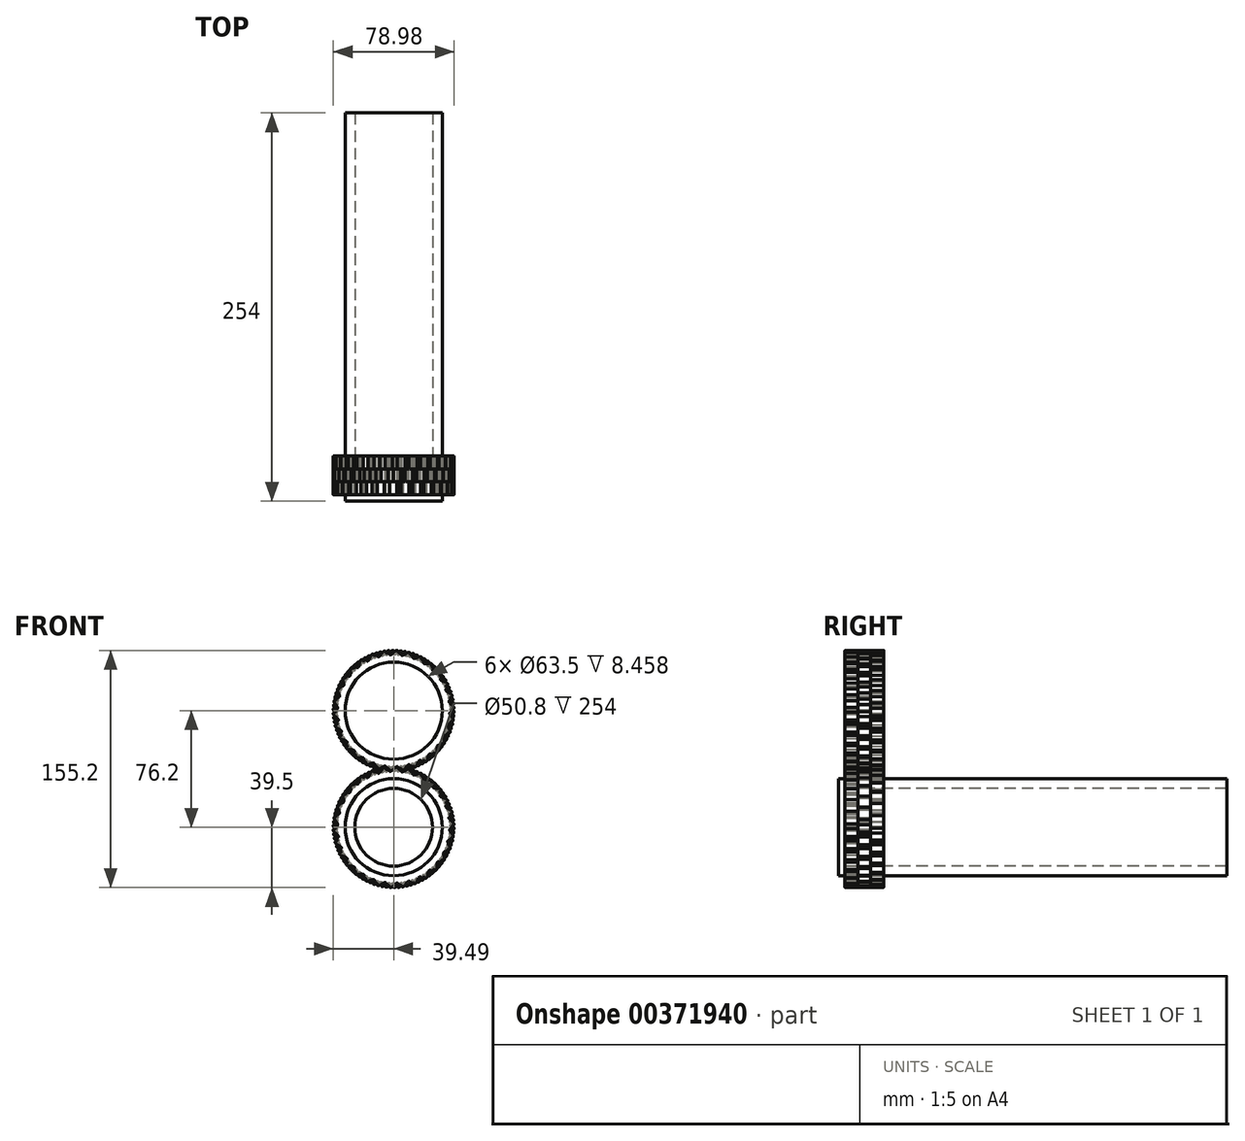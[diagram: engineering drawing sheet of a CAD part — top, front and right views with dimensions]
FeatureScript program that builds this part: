
annotation { "Feature Type Name" : "Feature", "Feature Type Description" : "" }
export const myFeature = defineFeature(function(context is Context, id is Id, definition is map)
    precondition{}
    {
        {
            var Q0;
            Q0=qCreatedBy(makeId("Front.planeOp"),FACE);
            var sketch = newSketch(context, id + "F0", { "sketchPlane" : qUnion([Q0])});
            skCircle(sketch, "E0", {"center": v(0, 0) * mm, "radius": 31.75 * mm});
            skCircle(sketch, "E1", {"center": v(0, 0) * mm, "radius": 25.4 * mm});
            skCircle(sketch, "E2", {"center": v(0, 0) * mm, "radius": 38.1 * mm});
            skPoint(sketch, "E3.middle", {"position": v(0, 38.1) * mm});
            skArc(sketch, "E4", {"start": v(-2.86, 36.42) * mm, "mid": v(-1.27, 36.98) * mm, "end": v(0, 38.1) * mm});
            skLineSegment(sketch, "E5", {"start": v(2.86, 39.78) * mm, "end": v(2.86, 38) * mm});
            skLineSegment(sketch, "E6", {"start": v(-2.86, 36.42) * mm, "end": v(-2.86, 38) * mm});
            skLineSegment(sketch, "E7.1.0", {"start": v(-10.37, 35.03) * mm, "end": v(-10.7, 36.57) * mm});
            skArc(sketch, "E7.1.1", {"start": v(-10.37, 35.03) * mm, "mid": v(-8.93, 35.91) * mm, "end": v(-7.92, 37.27) * mm});
            skArc(sketch, "E7.1.2", {"start": v(-5.48, 39.5) * mm, "mid": v(-6.92, 38.62) * mm, "end": v(-7.92, 37.27) * mm});
            skLineSegment(sketch, "E7.1.3", {"start": v(-5.48, 39.5) * mm, "end": v(-5.1, 37.76) * mm});
            skLineSegment(sketch, "E7.2.0", {"start": v(-17.42, 32.1) * mm, "end": v(-18.06, 33.55) * mm});
            skArc(sketch, "E7.2.1", {"start": v(-17.42, 32.1) * mm, "mid": v(-16.2, 33.27) * mm, "end": v(-15.5, 34.8) * mm});
            skArc(sketch, "E7.2.2", {"start": v(-13.57, 37.5) * mm, "mid": v(-14.8, 36.34) * mm, "end": v(-15.5, 34.8) * mm});
            skLineSegment(sketch, "E7.2.3", {"start": v(-13.57, 37.5) * mm, "end": v(-12.84, 35.87) * mm});
            skLineSegment(sketch, "E7.3.0", {"start": v(-23.72, 27.78) * mm, "end": v(-24.64, 29.06) * mm});
            skArc(sketch, "E7.3.1", {"start": v(-23.72, 27.78) * mm, "mid": v(-22.76, 29.18) * mm, "end": v(-22.4, 30.82) * mm});
            skArc(sketch, "E7.3.2", {"start": v(-21.07, 33.86) * mm, "mid": v(-22.03, 32.47) * mm, "end": v(-22.4, 30.82) * mm});
            skLineSegment(sketch, "E7.3.3", {"start": v(-21.07, 33.86) * mm, "end": v(-20.02, 32.42) * mm});
            skLineSegment(sketch, "E7.4.0", {"start": v(-28.98, 22.24) * mm, "end": v(-30.15, 23.3) * mm});
            skArc(sketch, "E7.4.1", {"start": v(-28.98, 22.24) * mm, "mid": v(-28.33, 23.8) * mm, "end": v(-28.31, 25.5) * mm});
            skArc(sketch, "E7.4.2", {"start": v(-27.65, 28.74) * mm, "mid": v(-28.3, 27.18) * mm, "end": v(-28.31, 25.5) * mm});
            skLineSegment(sketch, "E7.4.3", {"start": v(-27.65, 28.74) * mm, "end": v(-26.32, 27.55) * mm});
            skLineSegment(sketch, "E7.5.0", {"start": v(-32.97, 15.73) * mm, "end": v(-34.33, 16.52) * mm});
            skArc(sketch, "E7.5.1", {"start": v(-32.97, 15.73) * mm, "mid": v(-32.66, 17.4) * mm, "end": v(-33, 19.05) * mm});
            skArc(sketch, "E7.5.2", {"start": v(-33.02, 22.37) * mm, "mid": v(-33.33, 20.7) * mm, "end": v(-33, 19.05) * mm});
            skLineSegment(sketch, "E7.5.3", {"start": v(-33.02, 22.37) * mm, "end": v(-31.47, 21.47) * mm});
            skLineSegment(sketch, "E7.6.0", {"start": v(-35.52, 8.54) * mm, "end": v(-37.02, 9.02) * mm});
            skArc(sketch, "E7.6.1", {"start": v(-35.52, 8.54) * mm, "mid": v(-35.56, 10.22) * mm, "end": v(-36.24, 11.77) * mm});
            skArc(sketch, "E7.6.2", {"start": v(-36.95, 15.01) * mm, "mid": v(-36.9, 13.32) * mm, "end": v(-36.24, 11.77) * mm});
            skLineSegment(sketch, "E7.6.3", {"start": v(-36.95, 15.01) * mm, "end": v(-35.25, 14.46) * mm});
            skLineSegment(sketch, "E7.7.0", {"start": v(-36.52, 0.96) * mm, "end": v(-38.08, 1.13) * mm});
            skArc(sketch, "E7.7.1", {"start": v(-36.52, 0.96) * mm, "mid": v(-36.91, 2.6) * mm, "end": v(-37.9, 3.98) * mm});
            skArc(sketch, "E7.7.2", {"start": v(-39.27, 7) * mm, "mid": v(-38.87, 5.36) * mm, "end": v(-37.9, 3.98) * mm});
            skLineSegment(sketch, "E7.7.3", {"start": v(-39.27, 7) * mm, "end": v(-37.49, 6.81) * mm});
            skLineSegment(sketch, "E7.8.0", {"start": v(-35.92, -6.65) * mm, "end": v(-37.49, -6.81) * mm});
            skArc(sketch, "E7.8.1", {"start": v(-35.92, -6.65) * mm, "mid": v(-36.65, -5.13) * mm, "end": v(-37.9, -3.98) * mm});
            skArc(sketch, "E7.8.2", {"start": v(-39.86, -1.32) * mm, "mid": v(-39.13, -2.84) * mm, "end": v(-37.9, -3.98) * mm});
            skLineSegment(sketch, "E7.8.3", {"start": v(-39.86, -1.32) * mm, "end": v(-38.08, -1.13) * mm});
            skLineSegment(sketch, "E7.9.0", {"start": v(-33.75, -13.97) * mm, "end": v(-35.25, -14.46) * mm});
            skArc(sketch, "E7.9.1", {"start": v(-33.75, -13.97) * mm, "mid": v(-34.78, -12.63) * mm, "end": v(-36.24, -11.77) * mm});
            skArc(sketch, "E7.9.2", {"start": v(-38.72, -9.58) * mm, "mid": v(-37.69, -10.91) * mm, "end": v(-36.24, -11.77) * mm});
            skLineSegment(sketch, "E7.9.3", {"start": v(-38.72, -9.58) * mm, "end": v(-37.02, -9.02) * mm});
            skLineSegment(sketch, "E7.10.0", {"start": v(-30.11, -20.68) * mm, "end": v(-31.47, -21.47) * mm});
            skArc(sketch, "E7.10.1", {"start": v(-30.11, -20.68) * mm, "mid": v(-31.4, -19.59) * mm, "end": v(-33, -19.05) * mm});
            skArc(sketch, "E7.10.2", {"start": v(-35.88, -17.42) * mm, "mid": v(-34.6, -18.51) * mm, "end": v(-33, -19.05) * mm});
            skLineSegment(sketch, "E7.10.3", {"start": v(-35.88, -17.42) * mm, "end": v(-34.33, -16.52) * mm});
            skLineSegment(sketch, "E7.11.0", {"start": v(-25.15, -26.5) * mm, "end": v(-26.32, -27.55) * mm});
            skArc(sketch, "E7.11.1", {"start": v(-25.15, -26.5) * mm, "mid": v(-26.64, -25.69) * mm, "end": v(-28.31, -25.5) * mm});
            skArc(sketch, "E7.11.2", {"start": v(-31.48, -24.5) * mm, "mid": v(-30, -25.3) * mm, "end": v(-28.31, -25.5) * mm});
            skLineSegment(sketch, "E7.11.3", {"start": v(-31.48, -24.5) * mm, "end": v(-30.15, -23.3) * mm});
            skLineSegment(sketch, "E7.12.0", {"start": v(-19.1, -31.14) * mm, "end": v(-20.02, -32.42) * mm});
            skArc(sketch, "E7.12.1", {"start": v(-19.1, -31.14) * mm, "mid": v(-20.71, -30.66) * mm, "end": v(-22.4, -30.82) * mm});
            skArc(sketch, "E7.12.2", {"start": v(-25.7, -30.5) * mm, "mid": v(-24.08, -30.98) * mm, "end": v(-22.4, -30.82) * mm});
            skLineSegment(sketch, "E7.12.3", {"start": v(-25.7, -30.5) * mm, "end": v(-24.64, -29.06) * mm});
            skLineSegment(sketch, "E7.13.0", {"start": v(-12.2, -34.43) * mm, "end": v(-12.84, -35.87) * mm});
            skArc(sketch, "E7.13.1", {"start": v(-12.2, -34.43) * mm, "mid": v(-13.89, -34.3) * mm, "end": v(-15.5, -34.8) * mm});
            skArc(sketch, "E7.13.2", {"start": v(-18.8, -35.18) * mm, "mid": v(-17.1, -35.31) * mm, "end": v(-15.5, -34.8) * mm});
            skLineSegment(sketch, "E7.13.3", {"start": v(-18.8, -35.18) * mm, "end": v(-18.06, -33.55) * mm});
            skLineSegment(sketch, "E7.14.0", {"start": v(-4.78, -36.22) * mm, "end": v(-5.1, -37.76) * mm});
            skArc(sketch, "E7.14.1", {"start": v(-4.78, -36.22) * mm, "mid": v(-6.45, -36.44) * mm, "end": v(-7.92, -37.27) * mm});
            skArc(sketch, "E7.14.2", {"start": v(-11.07, -38.32) * mm, "mid": v(-9.4, -38.1) * mm, "end": v(-7.92, -37.27) * mm});
            skLineSegment(sketch, "E7.14.3", {"start": v(-11.07, -38.32) * mm, "end": v(-10.7, -36.57) * mm});
            skLineSegment(sketch, "E7.15.0", {"start": v(2.86, -36.42) * mm, "end": v(2.86, -38) * mm});
            skArc(sketch, "E7.15.1", {"start": v(2.86, -36.42) * mm, "mid": v(1.27, -36.98) * mm, "end": v(0, -38.1) * mm});
            skArc(sketch, "E7.15.2", {"start": v(-2.86, -39.78) * mm, "mid": v(-1.27, -39.22) * mm, "end": v(0, -38.1) * mm});
            skLineSegment(sketch, "E7.15.3", {"start": v(-2.86, -39.78) * mm, "end": v(-2.86, -38) * mm});
            skLineSegment(sketch, "E7.16.0", {"start": v(10.37, -35.03) * mm, "end": v(10.7, -36.57) * mm});
            skArc(sketch, "E7.16.1", {"start": v(10.37, -35.03) * mm, "mid": v(8.93, -35.91) * mm, "end": v(7.92, -37.27) * mm});
            skArc(sketch, "E7.16.2", {"start": v(5.48, -39.5) * mm, "mid": v(6.92, -38.62) * mm, "end": v(7.92, -37.27) * mm});
            skLineSegment(sketch, "E7.16.3", {"start": v(5.48, -39.5) * mm, "end": v(5.1, -37.76) * mm});
            skLineSegment(sketch, "E7.17.0", {"start": v(17.42, -32.1) * mm, "end": v(18.06, -33.55) * mm});
            skArc(sketch, "E7.17.1", {"start": v(17.42, -32.1) * mm, "mid": v(16.2, -33.27) * mm, "end": v(15.5, -34.8) * mm});
            skArc(sketch, "E7.17.2", {"start": v(13.57, -37.5) * mm, "mid": v(14.8, -36.34) * mm, "end": v(15.5, -34.8) * mm});
            skLineSegment(sketch, "E7.17.3", {"start": v(13.57, -37.5) * mm, "end": v(12.84, -35.87) * mm});
            skLineSegment(sketch, "E7.18.0", {"start": v(23.72, -27.78) * mm, "end": v(24.64, -29.06) * mm});
            skArc(sketch, "E7.18.1", {"start": v(23.72, -27.78) * mm, "mid": v(22.76, -29.18) * mm, "end": v(22.4, -30.82) * mm});
            skArc(sketch, "E7.18.2", {"start": v(21.07, -33.86) * mm, "mid": v(22.03, -32.47) * mm, "end": v(22.4, -30.82) * mm});
            skLineSegment(sketch, "E7.18.3", {"start": v(21.07, -33.86) * mm, "end": v(20.02, -32.42) * mm});
            skLineSegment(sketch, "E7.19.0", {"start": v(28.98, -22.24) * mm, "end": v(30.15, -23.3) * mm});
            skArc(sketch, "E7.19.1", {"start": v(28.98, -22.24) * mm, "mid": v(28.33, -23.8) * mm, "end": v(28.31, -25.5) * mm});
            skArc(sketch, "E7.19.2", {"start": v(27.65, -28.74) * mm, "mid": v(28.3, -27.18) * mm, "end": v(28.31, -25.5) * mm});
            skLineSegment(sketch, "E7.19.3", {"start": v(27.65, -28.74) * mm, "end": v(26.32, -27.55) * mm});
            skLineSegment(sketch, "E7.20.0", {"start": v(32.97, -15.73) * mm, "end": v(34.33, -16.52) * mm});
            skArc(sketch, "E7.20.1", {"start": v(32.97, -15.73) * mm, "mid": v(32.66, -17.4) * mm, "end": v(33, -19.05) * mm});
            skArc(sketch, "E7.20.2", {"start": v(33.02, -22.37) * mm, "mid": v(33.33, -20.7) * mm, "end": v(33, -19.05) * mm});
            skLineSegment(sketch, "E7.20.3", {"start": v(33.02, -22.37) * mm, "end": v(31.47, -21.47) * mm});
            skLineSegment(sketch, "E7.21.0", {"start": v(35.52, -8.54) * mm, "end": v(37.02, -9.02) * mm});
            skArc(sketch, "E7.21.1", {"start": v(35.52, -8.54) * mm, "mid": v(35.56, -10.22) * mm, "end": v(36.24, -11.77) * mm});
            skArc(sketch, "E7.21.2", {"start": v(36.95, -15.01) * mm, "mid": v(36.9, -13.32) * mm, "end": v(36.24, -11.77) * mm});
            skLineSegment(sketch, "E7.21.3", {"start": v(36.95, -15.01) * mm, "end": v(35.25, -14.46) * mm});
            skLineSegment(sketch, "E7.22.0", {"start": v(36.52, -0.96) * mm, "end": v(38.08, -1.13) * mm});
            skArc(sketch, "E7.22.1", {"start": v(36.52, -0.96) * mm, "mid": v(36.91, -2.6) * mm, "end": v(37.9, -3.98) * mm});
            skArc(sketch, "E7.22.2", {"start": v(39.27, -7) * mm, "mid": v(38.87, -5.36) * mm, "end": v(37.9, -3.98) * mm});
            skLineSegment(sketch, "E7.22.3", {"start": v(39.27, -7) * mm, "end": v(37.49, -6.81) * mm});
            skLineSegment(sketch, "E7.23.0", {"start": v(35.92, 6.65) * mm, "end": v(37.49, 6.81) * mm});
            skArc(sketch, "E7.23.1", {"start": v(35.92, 6.65) * mm, "mid": v(36.65, 5.13) * mm, "end": v(37.9, 3.98) * mm});
            skArc(sketch, "E7.23.2", {"start": v(39.86, 1.32) * mm, "mid": v(39.13, 2.84) * mm, "end": v(37.9, 3.98) * mm});
            skLineSegment(sketch, "E7.23.3", {"start": v(39.86, 1.32) * mm, "end": v(38.08, 1.13) * mm});
            skLineSegment(sketch, "E7.24.0", {"start": v(33.75, 13.97) * mm, "end": v(35.25, 14.46) * mm});
            skArc(sketch, "E7.24.1", {"start": v(33.75, 13.97) * mm, "mid": v(34.78, 12.63) * mm, "end": v(36.24, 11.77) * mm});
            skArc(sketch, "E7.24.2", {"start": v(38.72, 9.58) * mm, "mid": v(37.69, 10.91) * mm, "end": v(36.24, 11.77) * mm});
            skLineSegment(sketch, "E7.24.3", {"start": v(38.72, 9.58) * mm, "end": v(37.02, 9.02) * mm});
            skLineSegment(sketch, "E7.25.0", {"start": v(30.11, 20.68) * mm, "end": v(31.47, 21.47) * mm});
            skArc(sketch, "E7.25.1", {"start": v(30.11, 20.68) * mm, "mid": v(31.4, 19.59) * mm, "end": v(33, 19.05) * mm});
            skArc(sketch, "E7.25.2", {"start": v(35.88, 17.42) * mm, "mid": v(34.6, 18.51) * mm, "end": v(33, 19.05) * mm});
            skLineSegment(sketch, "E7.25.3", {"start": v(35.88, 17.42) * mm, "end": v(34.33, 16.52) * mm});
            skLineSegment(sketch, "E7.26.0", {"start": v(25.15, 26.5) * mm, "end": v(26.32, 27.55) * mm});
            skArc(sketch, "E7.26.1", {"start": v(25.15, 26.5) * mm, "mid": v(26.64, 25.69) * mm, "end": v(28.31, 25.5) * mm});
            skArc(sketch, "E7.26.2", {"start": v(31.48, 24.5) * mm, "mid": v(30, 25.3) * mm, "end": v(28.31, 25.5) * mm});
            skLineSegment(sketch, "E7.26.3", {"start": v(31.48, 24.5) * mm, "end": v(30.15, 23.3) * mm});
            skLineSegment(sketch, "E7.27.0", {"start": v(19.1, 31.14) * mm, "end": v(20.02, 32.42) * mm});
            skArc(sketch, "E7.27.1", {"start": v(19.1, 31.14) * mm, "mid": v(20.71, 30.66) * mm, "end": v(22.4, 30.82) * mm});
            skArc(sketch, "E7.27.2", {"start": v(25.7, 30.5) * mm, "mid": v(24.08, 30.98) * mm, "end": v(22.4, 30.82) * mm});
            skLineSegment(sketch, "E7.27.3", {"start": v(25.7, 30.5) * mm, "end": v(24.64, 29.06) * mm});
            skLineSegment(sketch, "E7.28.0", {"start": v(12.2, 34.43) * mm, "end": v(12.84, 35.87) * mm});
            skArc(sketch, "E7.28.1", {"start": v(12.2, 34.43) * mm, "mid": v(13.89, 34.3) * mm, "end": v(15.5, 34.8) * mm});
            skArc(sketch, "E7.28.2", {"start": v(18.8, 35.18) * mm, "mid": v(17.1, 35.31) * mm, "end": v(15.5, 34.8) * mm});
            skLineSegment(sketch, "E7.28.3", {"start": v(18.8, 35.18) * mm, "end": v(18.06, 33.55) * mm});
            skLineSegment(sketch, "E7.29.0", {"start": v(4.78, 36.22) * mm, "end": v(5.1, 37.76) * mm});
            skArc(sketch, "E7.29.1", {"start": v(4.78, 36.22) * mm, "mid": v(6.45, 36.44) * mm, "end": v(7.92, 37.27) * mm});
            skArc(sketch, "E7.29.2", {"start": v(11.07, 38.32) * mm, "mid": v(9.4, 38.1) * mm, "end": v(7.92, 37.27) * mm});
            skLineSegment(sketch, "E7.29.3", {"start": v(11.07, 38.32) * mm, "end": v(10.7, 36.57) * mm});
            skArc(sketch, "E8", {"start": v(1.88, 39.36) * mm, "mid": v(1.43, 39.2) * mm, "end": v(1, 38.97) * mm});
            skArc(sketch, "E9", {"start": v(2.86, 39.43) * mm, "mid": v(2.36, 39.46) * mm, "end": v(1.88, 39.36) * mm});
            skArc(sketch, "E10", {"start": v(1, 38.97) * mm, "mid": v(0.46, 38.58) * mm, "end": v(0, 38.1) * mm});
            skArc(sketch, "E11.1.0", {"start": v(-5.4, 39.17) * mm, "mid": v(-5.9, 39.1) * mm, "end": v(-6.34, 38.9) * mm});
            skArc(sketch, "E11.1.1", {"start": v(-6.34, 38.9) * mm, "mid": v(-6.75, 38.63) * mm, "end": v(-7.13, 38.33) * mm});
            skArc(sketch, "E11.1.2", {"start": v(-7.13, 38.33) * mm, "mid": v(-7.58, 37.84) * mm, "end": v(-7.92, 37.27) * mm});
            skArc(sketch, "E11.2.0", {"start": v(-13.43, 37.19) * mm, "mid": v(-13.9, 37.01) * mm, "end": v(-14.29, 36.72) * mm});
            skArc(sketch, "E11.2.1", {"start": v(-14.29, 36.72) * mm, "mid": v(-14.64, 36.39) * mm, "end": v(-14.94, 36.01) * mm});
            skArc(sketch, "E11.2.2", {"start": v(-14.94, 36.01) * mm, "mid": v(-15.28, 35.43) * mm, "end": v(-15.5, 34.8) * mm});
            skArc(sketch, "E11.3.0", {"start": v(-20.87, 33.58) * mm, "mid": v(-21.28, 33.32) * mm, "end": v(-21.61, 32.95) * mm});
            skArc(sketch, "E11.3.1", {"start": v(-21.61, 32.95) * mm, "mid": v(-21.88, 32.55) * mm, "end": v(-22.1, 32.12) * mm});
            skArc(sketch, "E11.3.2", {"start": v(-22.1, 32.12) * mm, "mid": v(-22.3, 31.48) * mm, "end": v(-22.4, 30.82) * mm});
            skArc(sketch, "E11.4.0", {"start": v(-27.4, 28.51) * mm, "mid": v(-27.74, 28.16) * mm, "end": v(-28, 27.74) * mm});
            skArc(sketch, "E11.4.1", {"start": v(-28, 27.74) * mm, "mid": v(-28.17, 27.29) * mm, "end": v(-28.3, 26.82) * mm});
            skArc(sketch, "E11.4.2", {"start": v(-28.3, 26.82) * mm, "mid": v(-28.37, 26.16) * mm, "end": v(-28.31, 25.5) * mm});
            skArc(sketch, "E11.5.0", {"start": v(-32.72, 22.2) * mm, "mid": v(-33, 21.78) * mm, "end": v(-33.15, 21.3) * mm});
            skArc(sketch, "E11.5.1", {"start": v(-33.15, 21.3) * mm, "mid": v(-33.23, 20.83) * mm, "end": v(-33.25, 20.35) * mm});
            skArc(sketch, "E11.5.2", {"start": v(-33.25, 20.35) * mm, "mid": v(-33.19, 19.69) * mm, "end": v(-33, 19.05) * mm});
            skArc(sketch, "E11.6.0", {"start": v(-36.62, 14.9) * mm, "mid": v(-36.8, 14.44) * mm, "end": v(-36.85, 13.95) * mm});
            skArc(sketch, "E11.6.1", {"start": v(-36.85, 13.95) * mm, "mid": v(-36.84, 13.47) * mm, "end": v(-36.76, 13) * mm});
            skArc(sketch, "E11.6.2", {"start": v(-36.76, 13) * mm, "mid": v(-36.55, 12.36) * mm, "end": v(-36.24, 11.77) * mm});
            skArc(sketch, "E11.7.0", {"start": v(-38.92, 6.96) * mm, "mid": v(-39, 6.48) * mm, "end": v(-38.95, 5.99) * mm});
            skArc(sketch, "E11.7.1", {"start": v(-38.95, 5.99) * mm, "mid": v(-38.83, 5.52) * mm, "end": v(-38.66, 5.06) * mm});
            skArc(sketch, "E11.7.2", {"start": v(-38.66, 5.06) * mm, "mid": v(-38.33, 4.49) * mm, "end": v(-37.9, 3.98) * mm});
            skArc(sketch, "E11.8.0", {"start": v(-39.52, -1.28) * mm, "mid": v(-39.5, -1.77) * mm, "end": v(-39.34, -2.24) * mm});
            skArc(sketch, "E11.8.1", {"start": v(-39.34, -2.24) * mm, "mid": v(-39.13, -2.68) * mm, "end": v(-38.87, -3.08) * mm});
            skArc(sketch, "E11.8.2", {"start": v(-38.87, -3.08) * mm, "mid": v(-38.42, -3.58) * mm, "end": v(-37.9, -3.98) * mm});
            skArc(sketch, "E11.9.0", {"start": v(-38.39, -9.47) * mm, "mid": v(-38.26, -9.95) * mm, "end": v(-38.01, -10.37) * mm});
            skArc(sketch, "E11.9.1", {"start": v(-38.01, -10.37) * mm, "mid": v(-37.72, -10.75) * mm, "end": v(-37.37, -11.1) * mm});
            skArc(sketch, "E11.9.2", {"start": v(-37.37, -11.1) * mm, "mid": v(-36.84, -11.49) * mm, "end": v(-36.24, -11.77) * mm});
            skArc(sketch, "E11.10.0", {"start": v(-35.58, -17.24) * mm, "mid": v(-35.36, -17.68) * mm, "end": v(-35.03, -18.05) * mm});
            skArc(sketch, "E11.10.1", {"start": v(-35.03, -18.05) * mm, "mid": v(-34.66, -18.36) * mm, "end": v(-34.25, -18.62) * mm});
            skArc(sketch, "E11.10.2", {"start": v(-34.25, -18.62) * mm, "mid": v(-33.64, -18.9) * mm, "end": v(-33, -19.05) * mm});
            skArc(sketch, "E11.11.0", {"start": v(-31.22, -24.26) * mm, "mid": v(-30.9, -24.65) * mm, "end": v(-30.5, -24.94) * mm});
            skArc(sketch, "E11.11.1", {"start": v(-30.5, -24.94) * mm, "mid": v(-30.08, -25.17) * mm, "end": v(-29.63, -25.34) * mm});
            skArc(sketch, "E11.11.2", {"start": v(-29.63, -25.34) * mm, "mid": v(-28.98, -25.48) * mm, "end": v(-28.31, -25.5) * mm});
            skArc(sketch, "E11.12.0", {"start": v(-25.5, -30.22) * mm, "mid": v(-25.1, -30.54) * mm, "end": v(-24.66, -30.74) * mm});
            skArc(sketch, "E11.12.1", {"start": v(-24.66, -30.74) * mm, "mid": v(-24.2, -30.87) * mm, "end": v(-23.71, -30.95) * mm});
            skArc(sketch, "E11.12.2", {"start": v(-23.71, -30.95) * mm, "mid": v(-23.05, -30.95) * mm, "end": v(-22.4, -30.82) * mm});
            skArc(sketch, "E11.13.0", {"start": v(-18.65, -34.86) * mm, "mid": v(-18.21, -35.09) * mm, "end": v(-17.73, -35.2) * mm});
            skArc(sketch, "E11.13.1", {"start": v(-17.73, -35.2) * mm, "mid": v(-17.25, -35.23) * mm, "end": v(-16.76, -35.2) * mm});
            skArc(sketch, "E11.13.2", {"start": v(-16.76, -35.2) * mm, "mid": v(-16.11, -35.06) * mm, "end": v(-15.5, -34.8) * mm});
            skArc(sketch, "E11.14.0", {"start": v(-11, -37.98) * mm, "mid": v(-10.52, -38.1) * mm, "end": v(-10.02, -38.1) * mm});
            skArc(sketch, "E11.14.1", {"start": v(-10.02, -38.1) * mm, "mid": v(-9.55, -38.04) * mm, "end": v(-9.08, -37.92) * mm});
            skArc(sketch, "E11.14.2", {"start": v(-9.08, -37.92) * mm, "mid": v(-8.47, -37.65) * mm, "end": v(-7.92, -37.27) * mm});
            skArc(sketch, "E11.15.0", {"start": v(-2.86, -39.43) * mm, "mid": v(-2.36, -39.46) * mm, "end": v(-1.88, -39.36) * mm});
            skArc(sketch, "E11.15.1", {"start": v(-1.88, -39.36) * mm, "mid": v(-1.43, -39.2) * mm, "end": v(-1, -38.97) * mm});
            skArc(sketch, "E11.15.2", {"start": v(-1, -38.97) * mm, "mid": v(-0.46, -38.58) * mm, "end": v(0, -38.1) * mm});
            skArc(sketch, "E11.16.0", {"start": v(5.4, -39.17) * mm, "mid": v(5.9, -39.1) * mm, "end": v(6.34, -38.9) * mm});
            skArc(sketch, "E11.16.1", {"start": v(6.34, -38.9) * mm, "mid": v(6.75, -38.63) * mm, "end": v(7.13, -38.33) * mm});
            skArc(sketch, "E11.16.2", {"start": v(7.13, -38.33) * mm, "mid": v(7.58, -37.84) * mm, "end": v(7.92, -37.27) * mm});
            skArc(sketch, "E11.17.0", {"start": v(13.43, -37.19) * mm, "mid": v(13.9, -37.01) * mm, "end": v(14.29, -36.72) * mm});
            skArc(sketch, "E11.17.1", {"start": v(14.29, -36.72) * mm, "mid": v(14.64, -36.39) * mm, "end": v(14.94, -36.01) * mm});
            skArc(sketch, "E11.17.2", {"start": v(14.94, -36.01) * mm, "mid": v(15.28, -35.43) * mm, "end": v(15.5, -34.8) * mm});
            skArc(sketch, "E11.18.0", {"start": v(20.87, -33.58) * mm, "mid": v(21.28, -33.32) * mm, "end": v(21.61, -32.95) * mm});
            skArc(sketch, "E11.18.1", {"start": v(21.61, -32.95) * mm, "mid": v(21.88, -32.55) * mm, "end": v(22.1, -32.12) * mm});
            skArc(sketch, "E11.18.2", {"start": v(22.1, -32.12) * mm, "mid": v(22.3, -31.48) * mm, "end": v(22.4, -30.82) * mm});
            skArc(sketch, "E11.19.0", {"start": v(27.4, -28.51) * mm, "mid": v(27.74, -28.16) * mm, "end": v(28, -27.74) * mm});
            skArc(sketch, "E11.19.1", {"start": v(28, -27.74) * mm, "mid": v(28.17, -27.29) * mm, "end": v(28.3, -26.82) * mm});
            skArc(sketch, "E11.19.2", {"start": v(28.3, -26.82) * mm, "mid": v(28.37, -26.16) * mm, "end": v(28.31, -25.5) * mm});
            skArc(sketch, "E11.20.0", {"start": v(32.72, -22.2) * mm, "mid": v(33, -21.78) * mm, "end": v(33.15, -21.3) * mm});
            skArc(sketch, "E11.20.1", {"start": v(33.15, -21.3) * mm, "mid": v(33.23, -20.83) * mm, "end": v(33.25, -20.35) * mm});
            skArc(sketch, "E11.20.2", {"start": v(33.25, -20.35) * mm, "mid": v(33.19, -19.69) * mm, "end": v(33, -19.05) * mm});
            skArc(sketch, "E11.21.0", {"start": v(36.62, -14.9) * mm, "mid": v(36.8, -14.44) * mm, "end": v(36.85, -13.95) * mm});
            skArc(sketch, "E11.21.1", {"start": v(36.85, -13.95) * mm, "mid": v(36.84, -13.47) * mm, "end": v(36.76, -13) * mm});
            skArc(sketch, "E11.21.2", {"start": v(36.76, -13) * mm, "mid": v(36.55, -12.36) * mm, "end": v(36.24, -11.77) * mm});
            skArc(sketch, "E11.22.0", {"start": v(38.92, -6.96) * mm, "mid": v(39, -6.48) * mm, "end": v(38.95, -5.99) * mm});
            skArc(sketch, "E11.22.1", {"start": v(38.95, -5.99) * mm, "mid": v(38.83, -5.52) * mm, "end": v(38.66, -5.06) * mm});
            skArc(sketch, "E11.22.2", {"start": v(38.66, -5.06) * mm, "mid": v(38.33, -4.49) * mm, "end": v(37.9, -3.98) * mm});
            skArc(sketch, "E11.23.0", {"start": v(39.52, 1.28) * mm, "mid": v(39.5, 1.77) * mm, "end": v(39.34, 2.24) * mm});
            skArc(sketch, "E11.23.1", {"start": v(39.34, 2.24) * mm, "mid": v(39.13, 2.68) * mm, "end": v(38.87, 3.08) * mm});
            skArc(sketch, "E11.23.2", {"start": v(38.87, 3.08) * mm, "mid": v(38.42, 3.58) * mm, "end": v(37.9, 3.98) * mm});
            skArc(sketch, "E11.24.0", {"start": v(38.39, 9.47) * mm, "mid": v(38.26, 9.95) * mm, "end": v(38.01, 10.37) * mm});
            skArc(sketch, "E11.24.1", {"start": v(38.01, 10.37) * mm, "mid": v(37.72, 10.75) * mm, "end": v(37.37, 11.1) * mm});
            skArc(sketch, "E11.24.2", {"start": v(37.37, 11.1) * mm, "mid": v(36.84, 11.49) * mm, "end": v(36.24, 11.77) * mm});
            skArc(sketch, "E11.25.0", {"start": v(35.58, 17.24) * mm, "mid": v(35.36, 17.68) * mm, "end": v(35.03, 18.05) * mm});
            skArc(sketch, "E11.25.1", {"start": v(35.03, 18.05) * mm, "mid": v(34.66, 18.36) * mm, "end": v(34.25, 18.62) * mm});
            skArc(sketch, "E11.25.2", {"start": v(34.25, 18.62) * mm, "mid": v(33.64, 18.9) * mm, "end": v(33, 19.05) * mm});
            skArc(sketch, "E11.26.0", {"start": v(31.22, 24.26) * mm, "mid": v(30.9, 24.65) * mm, "end": v(30.5, 24.94) * mm});
            skArc(sketch, "E11.26.1", {"start": v(30.5, 24.94) * mm, "mid": v(30.08, 25.17) * mm, "end": v(29.63, 25.34) * mm});
            skArc(sketch, "E11.26.2", {"start": v(29.63, 25.34) * mm, "mid": v(28.98, 25.48) * mm, "end": v(28.31, 25.5) * mm});
            skArc(sketch, "E11.27.0", {"start": v(25.5, 30.22) * mm, "mid": v(25.1, 30.54) * mm, "end": v(24.66, 30.74) * mm});
            skArc(sketch, "E11.27.1", {"start": v(24.66, 30.74) * mm, "mid": v(24.2, 30.87) * mm, "end": v(23.71, 30.95) * mm});
            skArc(sketch, "E11.27.2", {"start": v(23.71, 30.95) * mm, "mid": v(23.05, 30.95) * mm, "end": v(22.4, 30.82) * mm});
            skArc(sketch, "E11.28.0", {"start": v(18.65, 34.86) * mm, "mid": v(18.21, 35.09) * mm, "end": v(17.73, 35.2) * mm});
            skArc(sketch, "E11.28.1", {"start": v(17.73, 35.2) * mm, "mid": v(17.25, 35.23) * mm, "end": v(16.76, 35.2) * mm});
            skArc(sketch, "E11.28.2", {"start": v(16.76, 35.2) * mm, "mid": v(16.11, 35.06) * mm, "end": v(15.5, 34.8) * mm});
            skArc(sketch, "E11.29.0", {"start": v(11, 37.98) * mm, "mid": v(10.52, 38.1) * mm, "end": v(10.02, 38.1) * mm});
            skArc(sketch, "E11.29.1", {"start": v(10.02, 38.1) * mm, "mid": v(9.55, 38.04) * mm, "end": v(9.08, 37.92) * mm});
            skArc(sketch, "E11.29.2", {"start": v(9.08, 37.92) * mm, "mid": v(8.47, 37.65) * mm, "end": v(7.92, 37.27) * mm});
            skLineSegment(sketch, "E12", {"start": v(2.79, 39.45) * mm, "end": v(2.86, 38.71) * mm});
            skLineSegment(sketch, "E13.1.0", {"start": v(-5.47, 39.16) * mm, "end": v(-5.25, 38.46) * mm});
            skLineSegment(sketch, "E13.2.0", {"start": v(-13.5, 37.17) * mm, "end": v(-13.14, 36.53) * mm});
            skLineSegment(sketch, "E13.3.0", {"start": v(-20.93, 33.55) * mm, "end": v(-20.44, 33) * mm});
            skLineSegment(sketch, "E13.4.0", {"start": v(-27.45, 28.47) * mm, "end": v(-26.86, 28.03) * mm});
            skLineSegment(sketch, "E13.5.0", {"start": v(-32.77, 22.14) * mm, "end": v(-32.1, 21.83) * mm});
            skLineSegment(sketch, "E13.6.0", {"start": v(-36.65, 14.84) * mm, "end": v(-35.94, 14.68) * mm});
            skLineSegment(sketch, "E13.7.0", {"start": v(-38.94, 6.9) * mm, "end": v(-38.2, 6.89) * mm});
            skLineSegment(sketch, "E13.8.0", {"start": v(-39.52, -1.35) * mm, "end": v(-38.8, -1.2) * mm});
            skLineSegment(sketch, "E13.9.0", {"start": v(-38.38, -9.54) * mm, "end": v(-37.7, -9.25) * mm});
            skLineSegment(sketch, "E13.10.0", {"start": v(-35.56, -17.3) * mm, "end": v(-34.96, -16.88) * mm});
            skLineSegment(sketch, "E13.11.0", {"start": v(-31.18, -24.32) * mm, "end": v(-30.68, -23.78) * mm});
            skLineSegment(sketch, "E13.12.0", {"start": v(-25.44, -30.27) * mm, "end": v(-25.07, -29.64) * mm});
            skLineSegment(sketch, "E13.13.0", {"start": v(-18.6, -34.9) * mm, "end": v(-18.36, -34.2) * mm});
            skLineSegment(sketch, "E13.14.0", {"start": v(-10.93, -38) * mm, "end": v(-10.84, -37.27) * mm});
            skLineSegment(sketch, "E13.15.0", {"start": v(-2.79, -39.45) * mm, "end": v(-2.86, -38.71) * mm});
            skLineSegment(sketch, "E13.16.0", {"start": v(5.47, -39.16) * mm, "end": v(5.25, -38.46) * mm});
            skLineSegment(sketch, "E13.17.0", {"start": v(13.5, -37.17) * mm, "end": v(13.14, -36.53) * mm});
            skLineSegment(sketch, "E13.18.0", {"start": v(20.93, -33.55) * mm, "end": v(20.44, -33) * mm});
            skLineSegment(sketch, "E13.19.0", {"start": v(27.45, -28.47) * mm, "end": v(26.86, -28.03) * mm});
            skLineSegment(sketch, "E13.20.0", {"start": v(32.77, -22.14) * mm, "end": v(32.1, -21.83) * mm});
            skLineSegment(sketch, "E13.21.0", {"start": v(36.65, -14.84) * mm, "end": v(35.94, -14.68) * mm});
            skLineSegment(sketch, "E13.22.0", {"start": v(38.94, -6.9) * mm, "end": v(38.2, -6.89) * mm});
            skLineSegment(sketch, "E13.23.0", {"start": v(39.52, 1.35) * mm, "end": v(38.8, 1.2) * mm});
            skLineSegment(sketch, "E13.24.0", {"start": v(38.38, 9.54) * mm, "end": v(37.7, 9.25) * mm});
            skLineSegment(sketch, "E13.25.0", {"start": v(35.56, 17.3) * mm, "end": v(34.96, 16.88) * mm});
            skLineSegment(sketch, "E13.26.0", {"start": v(31.18, 24.32) * mm, "end": v(30.68, 23.78) * mm});
            skLineSegment(sketch, "E13.27.0", {"start": v(25.44, 30.27) * mm, "end": v(25.07, 29.64) * mm});
            skLineSegment(sketch, "E13.28.0", {"start": v(18.6, 34.9) * mm, "end": v(18.36, 34.2) * mm});
            skLineSegment(sketch, "E13.29.0", {"start": v(10.93, 38) * mm, "end": v(10.84, 37.27) * mm});
            skLineSegment(sketch, "E14", {"start": v(2.92, -37.99) * mm, "end": v(2.86, -37.2) * mm});
            skLineSegment(sketch, "E15.1.0", {"start": v(10.75, -36.55) * mm, "end": v(10.53, -35.8) * mm});
            skLineSegment(sketch, "E15.2.0", {"start": v(18.11, -33.52) * mm, "end": v(17.74, -32.83) * mm});
            skLineSegment(sketch, "E15.3.0", {"start": v(24.69, -29.02) * mm, "end": v(24.18, -28.42) * mm});
            skLineSegment(sketch, "E15.4.0", {"start": v(30.18, -23.25) * mm, "end": v(29.56, -22.77) * mm});
            skLineSegment(sketch, "E15.5.0", {"start": v(34.36, -16.47) * mm, "end": v(33.65, -16.13) * mm});
            skLineSegment(sketch, "E15.6.0", {"start": v(37.03, -8.97) * mm, "end": v(36.27, -8.78) * mm});
            skLineSegment(sketch, "E15.7.0", {"start": v(38.08, -1.07) * mm, "end": v(37.3, -1.05) * mm});
            skLineSegment(sketch, "E15.8.0", {"start": v(37.48, 6.87) * mm, "end": v(36.7, 6.73) * mm});
            skLineSegment(sketch, "E15.9.0", {"start": v(35.23, 14.51) * mm, "end": v(34.5, 14.21) * mm});
            skLineSegment(sketch, "E15.10.0", {"start": v(31.44, 21.52) * mm, "end": v(30.8, 21.08) * mm});
            skLineSegment(sketch, "E15.11.0", {"start": v(26.28, 27.59) * mm, "end": v(25.74, 27.02) * mm});
            skLineSegment(sketch, "E15.12.0", {"start": v(19.97, 32.45) * mm, "end": v(19.56, 31.78) * mm});
            skLineSegment(sketch, "E15.13.0", {"start": v(12.79, 35.89) * mm, "end": v(12.52, 35.15) * mm});
            skLineSegment(sketch, "E15.14.0", {"start": v(5.05, 37.76) * mm, "end": v(4.94, 36.99) * mm});
            skLineSegment(sketch, "E15.15.0", {"start": v(-2.92, 37.99) * mm, "end": v(-2.86, 37.2) * mm});
            skLineSegment(sketch, "E15.16.0", {"start": v(-10.75, 36.55) * mm, "end": v(-10.53, 35.8) * mm});
            skLineSegment(sketch, "E15.17.0", {"start": v(-18.11, 33.52) * mm, "end": v(-17.74, 32.83) * mm});
            skLineSegment(sketch, "E15.18.0", {"start": v(-24.69, 29.02) * mm, "end": v(-24.18, 28.42) * mm});
            skLineSegment(sketch, "E15.19.0", {"start": v(-30.18, 23.25) * mm, "end": v(-29.56, 22.77) * mm});
            skLineSegment(sketch, "E15.20.0", {"start": v(-34.36, 16.47) * mm, "end": v(-33.65, 16.13) * mm});
            skLineSegment(sketch, "E15.21.0", {"start": v(-37.03, 8.97) * mm, "end": v(-36.27, 8.78) * mm});
            skLineSegment(sketch, "E15.22.0", {"start": v(-38.08, 1.07) * mm, "end": v(-37.3, 1.05) * mm});
            skLineSegment(sketch, "E15.23.0", {"start": v(-37.48, -6.87) * mm, "end": v(-36.7, -6.73) * mm});
            skLineSegment(sketch, "E15.24.0", {"start": v(-35.23, -14.51) * mm, "end": v(-34.5, -14.21) * mm});
            skLineSegment(sketch, "E15.25.0", {"start": v(-31.44, -21.52) * mm, "end": v(-30.8, -21.08) * mm});
            skLineSegment(sketch, "E15.26.0", {"start": v(-26.28, -27.59) * mm, "end": v(-25.74, -27.02) * mm});
            skLineSegment(sketch, "E15.27.0", {"start": v(-19.97, -32.45) * mm, "end": v(-19.56, -31.78) * mm});
            skLineSegment(sketch, "E15.28.0", {"start": v(-12.79, -35.89) * mm, "end": v(-12.52, -35.15) * mm});
            skLineSegment(sketch, "E15.29.0", {"start": v(-5.05, -37.76) * mm, "end": v(-4.94, -36.99) * mm});
            skSolve(sketch);
        }
        {
            var Q0;
            Q0=makeQuery(id+"F0.imprint","IMPRINT",FACE,{"disambiguationData":[TD([[makeQuery(id+"F0.imprint","IMPRINT",EDGE,{"derivedFrom":sQuery(id+"F0.wireOp",EDGE,"E1")}),-1.0]])]});
            var Q1;
            {var subQ5=sQuery(id+"F0.wireOp",EDGE,"tDs8YB60-yQlt-PKr4-otda-xZHUuOfOvjSU.bottom");Q1=makeQuery(id+"F0.imprint","IMPRINT",FACE,{"disambiguationData":[TD([[makeQuery(id+"F0.imprint","IMPRINT",EDGE,{"derivedFrom":subQ5}),-1.0]])]});}
            extrude(context, id + "F1", {"entities" : qUnion([Q0, Q1]), "oppositeDirection" : true, "depth" : 254 * mm, "offsetDistance" : 25.4 * mm});
        }
        {
            var Q0;
            Q0=makeQuery(id+"F0.imprint","IMPRINT",FACE,{"disambiguationData":[TD([[makeQuery(id+"F0.imprint","IMPRINT",EDGE,{"derivedFrom":sQuery(id+"F0.wireOp",EDGE,"E0")}),-1.0]])]});
            var Q1;
            {var subQ3=sQuery(id+"F0.wireOp",EDGE,"F4ccViw4-8VKt-mRFL-Yw9l-lTW1q2JbDtwq");Q1=makeQuery(id+"F0.imprint","IMPRINT",FACE,{"disambiguationData":[TD([[makeQuery(id+"F0.imprint","IMPRINT",EDGE,{"derivedFrom":subQ3}),-1.0]])]});}
            var Q2;
            {var subQ1=sQuery(id+"F0.wireOp",EDGE,"E2");var subQ3=sQuery(id+"F0.wireOp",EDGE,"E5");var subQ4=makeQuery(id+"F0.imprint","INTERSECT",VERTEX,{"derivedFrom":[subQ1,subQ3]});Q2=makeQuery(id+"F0.imprint","IMPRINT",FACE,{"disambiguationData":[TD([[makeQuery(id+"F0.imprint","IMPRINT",EDGE,{"disambiguationData":[TD([[subQ4,-1.0]])],"derivedFrom":subQ1}),-1.0]])]});}
            var Q3;
            {var subQ4=sQuery(id+"F0.wireOp",EDGE,"E11.29.0");Q3=makeQuery(id+"F0.imprint","IMPRINT",FACE,{"disambiguationData":[TD([[makeQuery(id+"F0.imprint","IMPRINT",EDGE,{"derivedFrom":subQ4}),1.0]])]});}
            var Q4;
            {var subQ4=sQuery(id+"F0.wireOp",EDGE,"E11.28.0");Q4=makeQuery(id+"F0.imprint","IMPRINT",FACE,{"disambiguationData":[TD([[makeQuery(id+"F0.imprint","IMPRINT",EDGE,{"derivedFrom":subQ4}),1.0]])]});}
            var Q5;
            {var subQ4=sQuery(id+"F0.wireOp",EDGE,"E11.27.0");Q5=makeQuery(id+"F0.imprint","IMPRINT",FACE,{"disambiguationData":[TD([[makeQuery(id+"F0.imprint","IMPRINT",EDGE,{"derivedFrom":subQ4}),1.0]])]});}
            var Q6;
            {var subQ0=sQuery(id+"F0.wireOp",EDGE,"E11.26.0");Q6=makeQuery(id+"F0.imprint","IMPRINT",FACE,{"disambiguationData":[TD([[makeQuery(id+"F0.imprint","IMPRINT",EDGE,{"derivedFrom":subQ0}),1.0]])]});}
            var Q7;
            {var subQ0=sQuery(id+"F0.wireOp",EDGE,"E11.1.0");Q7=makeQuery(id+"F0.imprint","IMPRINT",FACE,{"disambiguationData":[TD([[makeQuery(id+"F0.imprint","IMPRINT",EDGE,{"derivedFrom":subQ0}),1.0]])]});}
            var Q8;
            {var subQ3=sQuery(id+"F0.wireOp",EDGE,"E11.2.0");Q8=makeQuery(id+"F0.imprint","IMPRINT",FACE,{"disambiguationData":[TD([[makeQuery(id+"F0.imprint","IMPRINT",EDGE,{"derivedFrom":subQ3}),1.0]])]});}
            var Q9;
            {var subQ0=sQuery(id+"F0.wireOp",EDGE,"E11.3.0");Q9=makeQuery(id+"F0.imprint","IMPRINT",FACE,{"disambiguationData":[TD([[makeQuery(id+"F0.imprint","IMPRINT",EDGE,{"derivedFrom":subQ0}),1.0]])]});}
            var Q10;
            {var subQ0=sQuery(id+"F0.wireOp",EDGE,"E11.4.0");Q10=makeQuery(id+"F0.imprint","IMPRINT",FACE,{"disambiguationData":[TD([[makeQuery(id+"F0.imprint","IMPRINT",EDGE,{"derivedFrom":subQ0}),1.0]])]});}
            var Q11;
            {var subQ0=sQuery(id+"F0.wireOp",EDGE,"E11.5.0");Q11=makeQuery(id+"F0.imprint","IMPRINT",FACE,{"disambiguationData":[TD([[makeQuery(id+"F0.imprint","IMPRINT",EDGE,{"derivedFrom":subQ0}),1.0]])]});}
            var Q12;
            {var subQ0=sQuery(id+"F0.wireOp",EDGE,"E11.6.0");Q12=makeQuery(id+"F0.imprint","IMPRINT",FACE,{"disambiguationData":[TD([[makeQuery(id+"F0.imprint","IMPRINT",EDGE,{"derivedFrom":subQ0}),1.0]])]});}
            var Q13;
            {var subQ0=sQuery(id+"F0.wireOp",EDGE,"E11.7.0");Q13=makeQuery(id+"F0.imprint","IMPRINT",FACE,{"disambiguationData":[TD([[makeQuery(id+"F0.imprint","IMPRINT",EDGE,{"derivedFrom":subQ0}),1.0]])]});}
            var Q14;
            {var subQ0=sQuery(id+"F0.wireOp",EDGE,"E11.8.0");Q14=makeQuery(id+"F0.imprint","IMPRINT",FACE,{"disambiguationData":[TD([[makeQuery(id+"F0.imprint","IMPRINT",EDGE,{"derivedFrom":subQ0}),1.0]])]});}
            var Q15;
            {var subQ4=sQuery(id+"F0.wireOp",EDGE,"E11.25.0");Q15=makeQuery(id+"F0.imprint","IMPRINT",FACE,{"disambiguationData":[TD([[makeQuery(id+"F0.imprint","IMPRINT",EDGE,{"derivedFrom":subQ4}),1.0]])]});}
            var Q16;
            {var subQ3=sQuery(id+"F0.wireOp",EDGE,"E11.24.0");Q16=makeQuery(id+"F0.imprint","IMPRINT",FACE,{"disambiguationData":[TD([[makeQuery(id+"F0.imprint","IMPRINT",EDGE,{"derivedFrom":subQ3}),1.0]])]});}
            var Q17;
            {var subQ4=sQuery(id+"F0.wireOp",EDGE,"E11.23.0");Q17=makeQuery(id+"F0.imprint","IMPRINT",FACE,{"disambiguationData":[TD([[makeQuery(id+"F0.imprint","IMPRINT",EDGE,{"derivedFrom":subQ4}),1.0]])]});}
            var Q18;
            {var subQ0=sQuery(id+"F0.wireOp",EDGE,"E11.22.0");Q18=makeQuery(id+"F0.imprint","IMPRINT",FACE,{"disambiguationData":[TD([[makeQuery(id+"F0.imprint","IMPRINT",EDGE,{"derivedFrom":subQ0}),1.0]])]});}
            var Q19;
            {var subQ0=sQuery(id+"F0.wireOp",EDGE,"E11.21.0");Q19=makeQuery(id+"F0.imprint","IMPRINT",FACE,{"disambiguationData":[TD([[makeQuery(id+"F0.imprint","IMPRINT",EDGE,{"derivedFrom":subQ0}),1.0]])]});}
            var Q20;
            {var subQ0=sQuery(id+"F0.wireOp",EDGE,"E11.20.0");Q20=makeQuery(id+"F0.imprint","IMPRINT",FACE,{"disambiguationData":[TD([[makeQuery(id+"F0.imprint","IMPRINT",EDGE,{"derivedFrom":subQ0}),1.0]])]});}
            var Q21;
            {var subQ0=sQuery(id+"F0.wireOp",EDGE,"E11.18.0");Q21=makeQuery(id+"F0.imprint","IMPRINT",FACE,{"disambiguationData":[TD([[makeQuery(id+"F0.imprint","IMPRINT",EDGE,{"derivedFrom":subQ0}),1.0]])]});}
            var Q22;
            {var subQ0=sQuery(id+"F0.wireOp",EDGE,"E11.17.0");Q22=makeQuery(id+"F0.imprint","IMPRINT",FACE,{"disambiguationData":[TD([[makeQuery(id+"F0.imprint","IMPRINT",EDGE,{"derivedFrom":subQ0}),1.0]])]});}
            var Q23;
            {var subQ0=sQuery(id+"F0.wireOp",EDGE,"E11.16.0");Q23=makeQuery(id+"F0.imprint","IMPRINT",FACE,{"disambiguationData":[TD([[makeQuery(id+"F0.imprint","IMPRINT",EDGE,{"derivedFrom":subQ0}),1.0]])]});}
            var Q24;
            {var subQ0=sQuery(id+"F0.wireOp",EDGE,"E11.15.0");Q24=makeQuery(id+"F0.imprint","IMPRINT",FACE,{"disambiguationData":[TD([[makeQuery(id+"F0.imprint","IMPRINT",EDGE,{"derivedFrom":subQ0}),1.0]])]});}
            var Q25;
            {var subQ0=sQuery(id+"F0.wireOp",EDGE,"E11.14.0");Q25=makeQuery(id+"F0.imprint","IMPRINT",FACE,{"disambiguationData":[TD([[makeQuery(id+"F0.imprint","IMPRINT",EDGE,{"derivedFrom":subQ0}),1.0]])]});}
            var Q26;
            {var subQ3=sQuery(id+"F0.wireOp",EDGE,"E11.13.0");Q26=makeQuery(id+"F0.imprint","IMPRINT",FACE,{"disambiguationData":[TD([[makeQuery(id+"F0.imprint","IMPRINT",EDGE,{"derivedFrom":subQ3}),1.0]])]});}
            var Q27;
            {var subQ0=sQuery(id+"F0.wireOp",EDGE,"E11.12.0");Q27=makeQuery(id+"F0.imprint","IMPRINT",FACE,{"disambiguationData":[TD([[makeQuery(id+"F0.imprint","IMPRINT",EDGE,{"derivedFrom":subQ0}),1.0]])]});}
            var Q28;
            {var subQ0=sQuery(id+"F0.wireOp",EDGE,"E11.11.0");Q28=makeQuery(id+"F0.imprint","IMPRINT",FACE,{"disambiguationData":[TD([[makeQuery(id+"F0.imprint","IMPRINT",EDGE,{"derivedFrom":subQ0}),1.0]])]});}
            var Q29;
            {var subQ0=sQuery(id+"F0.wireOp",EDGE,"E11.10.0");Q29=makeQuery(id+"F0.imprint","IMPRINT",FACE,{"disambiguationData":[TD([[makeQuery(id+"F0.imprint","IMPRINT",EDGE,{"derivedFrom":subQ0}),1.0]])]});}
            var Q30;
            {var subQ0=sQuery(id+"F0.wireOp",EDGE,"E11.9.0");Q30=makeQuery(id+"F0.imprint","IMPRINT",FACE,{"disambiguationData":[TD([[makeQuery(id+"F0.imprint","IMPRINT",EDGE,{"derivedFrom":subQ0}),1.0]])]});}
            var Q31;
            {var subQ0=sQuery(id+"F0.wireOp",EDGE,"E11.19.0");Q31=makeQuery(id+"F0.imprint","IMPRINT",FACE,{"disambiguationData":[TD([[makeQuery(id+"F0.imprint","IMPRINT",EDGE,{"derivedFrom":subQ0}),1.0]])]});}
            var Q32;
            {var subQ0=sQuery(id+"F0.wireOp",EDGE,"E11.1.1");Q32=makeQuery(id+"F0.imprint","IMPRINT",FACE,{"disambiguationData":[TD([[makeQuery(id+"F0.imprint","IMPRINT",EDGE,{"derivedFrom":subQ0}),1.0]])]});}
            var Q33;
            {var subQ0=sQuery(id+"F0.wireOp",EDGE,"E11.2.1");Q33=makeQuery(id+"F0.imprint","IMPRINT",FACE,{"disambiguationData":[TD([[makeQuery(id+"F0.imprint","IMPRINT",EDGE,{"derivedFrom":subQ0}),1.0]])]});}
            var Q34;
            {var subQ0=sQuery(id+"F0.wireOp",EDGE,"E11.3.1");Q34=makeQuery(id+"F0.imprint","IMPRINT",FACE,{"disambiguationData":[TD([[makeQuery(id+"F0.imprint","IMPRINT",EDGE,{"derivedFrom":subQ0}),1.0]])]});}
            var Q35;
            {var subQ0=sQuery(id+"F0.wireOp",EDGE,"E11.4.1");Q35=makeQuery(id+"F0.imprint","IMPRINT",FACE,{"disambiguationData":[TD([[makeQuery(id+"F0.imprint","IMPRINT",EDGE,{"derivedFrom":subQ0}),1.0]])]});}
            var Q36;
            {var subQ0=sQuery(id+"F0.wireOp",EDGE,"E11.5.1");Q36=makeQuery(id+"F0.imprint","IMPRINT",FACE,{"disambiguationData":[TD([[makeQuery(id+"F0.imprint","IMPRINT",EDGE,{"derivedFrom":subQ0}),1.0]])]});}
            var Q37;
            {var subQ0=sQuery(id+"F0.wireOp",EDGE,"E11.6.1");Q37=makeQuery(id+"F0.imprint","IMPRINT",FACE,{"disambiguationData":[TD([[makeQuery(id+"F0.imprint","IMPRINT",EDGE,{"derivedFrom":subQ0}),1.0]])]});}
            var Q38;
            {var subQ0=sQuery(id+"F0.wireOp",EDGE,"E11.7.1");Q38=makeQuery(id+"F0.imprint","IMPRINT",FACE,{"disambiguationData":[TD([[makeQuery(id+"F0.imprint","IMPRINT",EDGE,{"derivedFrom":subQ0}),1.0]])]});}
            var Q39;
            {var subQ0=sQuery(id+"F0.wireOp",EDGE,"E11.8.1");Q39=makeQuery(id+"F0.imprint","IMPRINT",FACE,{"disambiguationData":[TD([[makeQuery(id+"F0.imprint","IMPRINT",EDGE,{"derivedFrom":subQ0}),1.0]])]});}
            var Q40;
            {var subQ0=sQuery(id+"F0.wireOp",EDGE,"E11.9.1");Q40=makeQuery(id+"F0.imprint","IMPRINT",FACE,{"disambiguationData":[TD([[makeQuery(id+"F0.imprint","IMPRINT",EDGE,{"derivedFrom":subQ0}),1.0]])]});}
            var Q41;
            {var subQ0=sQuery(id+"F0.wireOp",EDGE,"E11.10.1");Q41=makeQuery(id+"F0.imprint","IMPRINT",FACE,{"disambiguationData":[TD([[makeQuery(id+"F0.imprint","IMPRINT",EDGE,{"derivedFrom":subQ0}),1.0]])]});}
            var Q42;
            {var subQ0=sQuery(id+"F0.wireOp",EDGE,"E11.11.1");Q42=makeQuery(id+"F0.imprint","IMPRINT",FACE,{"disambiguationData":[TD([[makeQuery(id+"F0.imprint","IMPRINT",EDGE,{"derivedFrom":subQ0}),1.0]])]});}
            var Q43;
            {var subQ0=sQuery(id+"F0.wireOp",EDGE,"E11.12.1");Q43=makeQuery(id+"F0.imprint","IMPRINT",FACE,{"disambiguationData":[TD([[makeQuery(id+"F0.imprint","IMPRINT",EDGE,{"derivedFrom":subQ0}),1.0]])]});}
            var Q44;
            {var subQ0=sQuery(id+"F0.wireOp",EDGE,"E11.13.1");Q44=makeQuery(id+"F0.imprint","IMPRINT",FACE,{"disambiguationData":[TD([[makeQuery(id+"F0.imprint","IMPRINT",EDGE,{"derivedFrom":subQ0}),1.0]])]});}
            var Q45;
            {var subQ0=sQuery(id+"F0.wireOp",EDGE,"E11.14.1");Q45=makeQuery(id+"F0.imprint","IMPRINT",FACE,{"disambiguationData":[TD([[makeQuery(id+"F0.imprint","IMPRINT",EDGE,{"derivedFrom":subQ0}),1.0]])]});}
            var Q46;
            {var subQ0=sQuery(id+"F0.wireOp",EDGE,"E11.15.1");Q46=makeQuery(id+"F0.imprint","IMPRINT",FACE,{"disambiguationData":[TD([[makeQuery(id+"F0.imprint","IMPRINT",EDGE,{"derivedFrom":subQ0}),1.0]])]});}
            var Q47;
            {var subQ0=sQuery(id+"F0.wireOp",EDGE,"E11.16.1");Q47=makeQuery(id+"F0.imprint","IMPRINT",FACE,{"disambiguationData":[TD([[makeQuery(id+"F0.imprint","IMPRINT",EDGE,{"derivedFrom":subQ0}),1.0]])]});}
            var Q48;
            {var subQ0=sQuery(id+"F0.wireOp",EDGE,"E11.17.1");Q48=makeQuery(id+"F0.imprint","IMPRINT",FACE,{"disambiguationData":[TD([[makeQuery(id+"F0.imprint","IMPRINT",EDGE,{"derivedFrom":subQ0}),1.0]])]});}
            var Q49;
            {var subQ0=sQuery(id+"F0.wireOp",EDGE,"E11.18.1");Q49=makeQuery(id+"F0.imprint","IMPRINT",FACE,{"disambiguationData":[TD([[makeQuery(id+"F0.imprint","IMPRINT",EDGE,{"derivedFrom":subQ0}),1.0]])]});}
            var Q50;
            {var subQ0=sQuery(id+"F0.wireOp",EDGE,"E11.19.1");Q50=makeQuery(id+"F0.imprint","IMPRINT",FACE,{"disambiguationData":[TD([[makeQuery(id+"F0.imprint","IMPRINT",EDGE,{"derivedFrom":subQ0}),1.0]])]});}
            var Q51;
            {var subQ0=sQuery(id+"F0.wireOp",EDGE,"E11.20.1");Q51=makeQuery(id+"F0.imprint","IMPRINT",FACE,{"disambiguationData":[TD([[makeQuery(id+"F0.imprint","IMPRINT",EDGE,{"derivedFrom":subQ0}),1.0]])]});}
            var Q52;
            {var subQ0=sQuery(id+"F0.wireOp",EDGE,"E11.21.1");Q52=makeQuery(id+"F0.imprint","IMPRINT",FACE,{"disambiguationData":[TD([[makeQuery(id+"F0.imprint","IMPRINT",EDGE,{"derivedFrom":subQ0}),1.0]])]});}
            var Q53;
            {var subQ0=sQuery(id+"F0.wireOp",EDGE,"E11.22.1");Q53=makeQuery(id+"F0.imprint","IMPRINT",FACE,{"disambiguationData":[TD([[makeQuery(id+"F0.imprint","IMPRINT",EDGE,{"derivedFrom":subQ0}),1.0]])]});}
            var Q54;
            {var subQ0=sQuery(id+"F0.wireOp",EDGE,"E11.23.1");Q54=makeQuery(id+"F0.imprint","IMPRINT",FACE,{"disambiguationData":[TD([[makeQuery(id+"F0.imprint","IMPRINT",EDGE,{"derivedFrom":subQ0}),1.0]])]});}
            var Q55;
            {var subQ0=sQuery(id+"F0.wireOp",EDGE,"E11.24.1");Q55=makeQuery(id+"F0.imprint","IMPRINT",FACE,{"disambiguationData":[TD([[makeQuery(id+"F0.imprint","IMPRINT",EDGE,{"derivedFrom":subQ0}),1.0]])]});}
            var Q56;
            {var subQ0=sQuery(id+"F0.wireOp",EDGE,"E11.25.1");Q56=makeQuery(id+"F0.imprint","IMPRINT",FACE,{"disambiguationData":[TD([[makeQuery(id+"F0.imprint","IMPRINT",EDGE,{"derivedFrom":subQ0}),1.0]])]});}
            var Q57;
            {var subQ0=sQuery(id+"F0.wireOp",EDGE,"E11.26.1");Q57=makeQuery(id+"F0.imprint","IMPRINT",FACE,{"disambiguationData":[TD([[makeQuery(id+"F0.imprint","IMPRINT",EDGE,{"derivedFrom":subQ0}),1.0]])]});}
            var Q58;
            {var subQ0=sQuery(id+"F0.wireOp",EDGE,"E11.27.1");Q58=makeQuery(id+"F0.imprint","IMPRINT",FACE,{"disambiguationData":[TD([[makeQuery(id+"F0.imprint","IMPRINT",EDGE,{"derivedFrom":subQ0}),1.0]])]});}
            var Q59;
            {var subQ0=sQuery(id+"F0.wireOp",EDGE,"E11.28.1");Q59=makeQuery(id+"F0.imprint","IMPRINT",FACE,{"disambiguationData":[TD([[makeQuery(id+"F0.imprint","IMPRINT",EDGE,{"derivedFrom":subQ0}),1.0]])]});}
            var Q60;
            {var subQ0=sQuery(id+"F0.wireOp",EDGE,"E11.29.1");Q60=makeQuery(id+"F0.imprint","IMPRINT",FACE,{"disambiguationData":[TD([[makeQuery(id+"F0.imprint","IMPRINT",EDGE,{"derivedFrom":subQ0}),1.0]])]});}
            extrude(context, id + "F2", {"entities" : qUnion([Q0, Q1, Q2, Q3, Q4, Q5, Q6, Q7, Q8, Q9, Q10, Q11, Q12, Q13, Q14, Q15, Q16, Q17, Q18, Q19, Q20, Q21, Q22, Q23, Q24, Q25, Q26, Q27, Q28, Q29, Q30, Q31, Q32, Q33, Q34, Q35, Q36, Q37, Q38, Q39, Q40, Q41, Q42, Q43, Q44, Q45, Q46, Q47, Q48, Q49, Q50, Q51, Q52, Q53, Q54, Q55, Q56, Q57, Q58, Q59, Q60]), "depth" : 8.46 * mm, "offsetDistance" : 25.4 * mm});
        }
        {
            var Q0;
            Q0=makeQuery(id+"F2.opExtrude","SWEPT_BODY",BODY,{"disambiguationData":[OSD([sQuery(id+"F0.wireOp",EDGE,"E0"),sQuery(id+"F0.wireOp",EDGE,"E2"),sQuery(id+"F0.wireOp",EDGE,"kblbpXZE-b2Sg-FZdv-FlMF-ZwbeqijesS82"),sQuery(id+"F0.wireOp",EDGE,"E4"),sQuery(id+"F0.wireOp",EDGE,"E5"),sQuery(id+"F0.wireOp",EDGE,"E6"),sQuery(id+"F0.wireOp",EDGE,"E7.1.0"),sQuery(id+"F0.wireOp",EDGE,"E7.1.1"),sQuery(id+"F0.wireOp",EDGE,"E7.1.2"),sQuery(id+"F0.wireOp",EDGE,"E7.1.3"),sQuery(id+"F0.wireOp",EDGE,"E7.2.0"),sQuery(id+"F0.wireOp",EDGE,"E7.2.1"),sQuery(id+"F0.wireOp",EDGE,"E7.2.2"),sQuery(id+"F0.wireOp",EDGE,"E7.2.3"),sQuery(id+"F0.wireOp",EDGE,"E7.3.0"),sQuery(id+"F0.wireOp",EDGE,"E7.3.1"),sQuery(id+"F0.wireOp",EDGE,"E7.3.2"),sQuery(id+"F0.wireOp",EDGE,"E7.3.3"),sQuery(id+"F0.wireOp",EDGE,"E7.4.0"),sQuery(id+"F0.wireOp",EDGE,"E7.4.1"),sQuery(id+"F0.wireOp",EDGE,"E7.4.2"),sQuery(id+"F0.wireOp",EDGE,"E7.4.3"),sQuery(id+"F0.wireOp",EDGE,"E7.5.0"),sQuery(id+"F0.wireOp",EDGE,"E7.5.1"),sQuery(id+"F0.wireOp",EDGE,"E7.5.2"),sQuery(id+"F0.wireOp",EDGE,"E7.5.3"),sQuery(id+"F0.wireOp",EDGE,"E7.6.0"),sQuery(id+"F0.wireOp",EDGE,"E7.6.1"),sQuery(id+"F0.wireOp",EDGE,"E7.6.2"),sQuery(id+"F0.wireOp",EDGE,"E7.6.3"),sQuery(id+"F0.wireOp",EDGE,"E7.7.0"),sQuery(id+"F0.wireOp",EDGE,"E7.7.1"),sQuery(id+"F0.wireOp",EDGE,"E7.7.2"),sQuery(id+"F0.wireOp",EDGE,"E7.7.3"),sQuery(id+"F0.wireOp",EDGE,"E7.8.0"),sQuery(id+"F0.wireOp",EDGE,"E7.8.1"),sQuery(id+"F0.wireOp",EDGE,"E7.8.2"),sQuery(id+"F0.wireOp",EDGE,"E7.8.3"),sQuery(id+"F0.wireOp",EDGE,"E7.9.0"),sQuery(id+"F0.wireOp",EDGE,"E7.9.1"),sQuery(id+"F0.wireOp",EDGE,"E7.9.2"),sQuery(id+"F0.wireOp",EDGE,"E7.9.3"),sQuery(id+"F0.wireOp",EDGE,"E7.10.0"),sQuery(id+"F0.wireOp",EDGE,"E7.10.1"),sQuery(id+"F0.wireOp",EDGE,"E7.10.2"),sQuery(id+"F0.wireOp",EDGE,"E7.10.3"),sQuery(id+"F0.wireOp",EDGE,"E7.11.0"),sQuery(id+"F0.wireOp",EDGE,"E7.11.1"),sQuery(id+"F0.wireOp",EDGE,"E7.11.2"),sQuery(id+"F0.wireOp",EDGE,"E7.11.3"),sQuery(id+"F0.wireOp",EDGE,"E7.12.0"),sQuery(id+"F0.wireOp",EDGE,"E7.12.1"),sQuery(id+"F0.wireOp",EDGE,"E7.12.2"),sQuery(id+"F0.wireOp",EDGE,"E7.12.3"),sQuery(id+"F0.wireOp",EDGE,"E7.13.0"),sQuery(id+"F0.wireOp",EDGE,"E7.13.1"),sQuery(id+"F0.wireOp",EDGE,"E7.13.2"),sQuery(id+"F0.wireOp",EDGE,"E7.13.3"),sQuery(id+"F0.wireOp",EDGE,"E7.14.0"),sQuery(id+"F0.wireOp",EDGE,"E7.14.1"),sQuery(id+"F0.wireOp",EDGE,"E7.14.2"),sQuery(id+"F0.wireOp",EDGE,"E7.14.3"),sQuery(id+"F0.wireOp",EDGE,"E7.15.0"),sQuery(id+"F0.wireOp",EDGE,"E7.15.1"),sQuery(id+"F0.wireOp",EDGE,"E7.15.2"),sQuery(id+"F0.wireOp",EDGE,"E7.15.3"),sQuery(id+"F0.wireOp",EDGE,"E7.16.0"),sQuery(id+"F0.wireOp",EDGE,"E7.16.1"),sQuery(id+"F0.wireOp",EDGE,"E7.16.2"),sQuery(id+"F0.wireOp",EDGE,"E7.16.3"),sQuery(id+"F0.wireOp",EDGE,"E7.17.0"),sQuery(id+"F0.wireOp",EDGE,"E7.17.1"),sQuery(id+"F0.wireOp",EDGE,"E7.17.2"),sQuery(id+"F0.wireOp",EDGE,"E7.17.3"),sQuery(id+"F0.wireOp",EDGE,"E7.18.0"),sQuery(id+"F0.wireOp",EDGE,"E7.18.1"),sQuery(id+"F0.wireOp",EDGE,"E7.18.2"),sQuery(id+"F0.wireOp",EDGE,"E7.18.3"),sQuery(id+"F0.wireOp",EDGE,"E7.19.0"),sQuery(id+"F0.wireOp",EDGE,"E7.19.1"),sQuery(id+"F0.wireOp",EDGE,"E7.19.2"),sQuery(id+"F0.wireOp",EDGE,"E7.19.3"),sQuery(id+"F0.wireOp",EDGE,"E7.20.0"),sQuery(id+"F0.wireOp",EDGE,"E7.20.1"),sQuery(id+"F0.wireOp",EDGE,"E7.20.2"),sQuery(id+"F0.wireOp",EDGE,"E7.20.3"),sQuery(id+"F0.wireOp",EDGE,"E7.21.0"),sQuery(id+"F0.wireOp",EDGE,"E7.21.1"),sQuery(id+"F0.wireOp",EDGE,"E7.21.2"),sQuery(id+"F0.wireOp",EDGE,"E7.21.3"),sQuery(id+"F0.wireOp",EDGE,"E7.22.0"),sQuery(id+"F0.wireOp",EDGE,"E7.22.1"),sQuery(id+"F0.wireOp",EDGE,"E7.22.2"),sQuery(id+"F0.wireOp",EDGE,"E7.22.3"),sQuery(id+"F0.wireOp",EDGE,"E7.23.0"),sQuery(id+"F0.wireOp",EDGE,"E7.23.1"),sQuery(id+"F0.wireOp",EDGE,"E7.23.2"),sQuery(id+"F0.wireOp",EDGE,"E7.23.3"),sQuery(id+"F0.wireOp",EDGE,"E7.24.0"),sQuery(id+"F0.wireOp",EDGE,"E7.24.1"),sQuery(id+"F0.wireOp",EDGE,"E7.24.2"),sQuery(id+"F0.wireOp",EDGE,"E7.24.3"),sQuery(id+"F0.wireOp",EDGE,"E7.25.0"),sQuery(id+"F0.wireOp",EDGE,"E7.25.1"),sQuery(id+"F0.wireOp",EDGE,"E7.25.2"),sQuery(id+"F0.wireOp",EDGE,"E7.25.3"),sQuery(id+"F0.wireOp",EDGE,"E7.26.0"),sQuery(id+"F0.wireOp",EDGE,"E7.26.1"),sQuery(id+"F0.wireOp",EDGE,"E7.26.2"),sQuery(id+"F0.wireOp",EDGE,"E7.26.3"),sQuery(id+"F0.wireOp",EDGE,"E7.27.0"),sQuery(id+"F0.wireOp",EDGE,"E7.27.1"),sQuery(id+"F0.wireOp",EDGE,"E7.27.2"),sQuery(id+"F0.wireOp",EDGE,"E7.27.3"),sQuery(id+"F0.wireOp",EDGE,"E7.28.0"),sQuery(id+"F0.wireOp",EDGE,"E7.28.1"),sQuery(id+"F0.wireOp",EDGE,"E7.28.2"),sQuery(id+"F0.wireOp",EDGE,"E7.28.3"),sQuery(id+"F0.wireOp",EDGE,"E7.29.0"),sQuery(id+"F0.wireOp",EDGE,"E7.29.1"),sQuery(id+"F0.wireOp",EDGE,"E7.29.2"),sQuery(id+"F0.wireOp",EDGE,"E7.29.3")])]});
            transform(context, id + "F3", {"entities" : qUnion([Q0]), "transformType" : TransformType.TRANSLATION_3D, "dx" : 0 * mm, "dy" : 12.7 * mm, "dz" : 0 * mm, "makeCopy" : false});
        }
        {
            var Q0;
            Q0=makeQuery(id+"F2.opExtrude","SWEPT_BODY",BODY,{"disambiguationData":[OSD([sQuery(id+"F0.wireOp",EDGE,"E0"),sQuery(id+"F0.wireOp",EDGE,"E2"),sQuery(id+"F0.wireOp",EDGE,"kblbpXZE-b2Sg-FZdv-FlMF-ZwbeqijesS82"),sQuery(id+"F0.wireOp",EDGE,"E4"),sQuery(id+"F0.wireOp",EDGE,"E5"),sQuery(id+"F0.wireOp",EDGE,"E6"),sQuery(id+"F0.wireOp",EDGE,"E7.1.0"),sQuery(id+"F0.wireOp",EDGE,"E7.1.1"),sQuery(id+"F0.wireOp",EDGE,"E7.1.2"),sQuery(id+"F0.wireOp",EDGE,"E7.1.3"),sQuery(id+"F0.wireOp",EDGE,"E7.2.0"),sQuery(id+"F0.wireOp",EDGE,"E7.2.1"),sQuery(id+"F0.wireOp",EDGE,"E7.2.2"),sQuery(id+"F0.wireOp",EDGE,"E7.2.3"),sQuery(id+"F0.wireOp",EDGE,"E7.3.0"),sQuery(id+"F0.wireOp",EDGE,"E7.3.1"),sQuery(id+"F0.wireOp",EDGE,"E7.3.2"),sQuery(id+"F0.wireOp",EDGE,"E7.3.3"),sQuery(id+"F0.wireOp",EDGE,"E7.4.0"),sQuery(id+"F0.wireOp",EDGE,"E7.4.1"),sQuery(id+"F0.wireOp",EDGE,"E7.4.2"),sQuery(id+"F0.wireOp",EDGE,"E7.4.3"),sQuery(id+"F0.wireOp",EDGE,"E7.5.0"),sQuery(id+"F0.wireOp",EDGE,"E7.5.1"),sQuery(id+"F0.wireOp",EDGE,"E7.5.2"),sQuery(id+"F0.wireOp",EDGE,"E7.5.3"),sQuery(id+"F0.wireOp",EDGE,"E7.6.0"),sQuery(id+"F0.wireOp",EDGE,"E7.6.1"),sQuery(id+"F0.wireOp",EDGE,"E7.6.2"),sQuery(id+"F0.wireOp",EDGE,"E7.6.3"),sQuery(id+"F0.wireOp",EDGE,"E7.7.0"),sQuery(id+"F0.wireOp",EDGE,"E7.7.1"),sQuery(id+"F0.wireOp",EDGE,"E7.7.2"),sQuery(id+"F0.wireOp",EDGE,"E7.7.3"),sQuery(id+"F0.wireOp",EDGE,"E7.8.0"),sQuery(id+"F0.wireOp",EDGE,"E7.8.1"),sQuery(id+"F0.wireOp",EDGE,"E7.8.2"),sQuery(id+"F0.wireOp",EDGE,"E7.8.3"),sQuery(id+"F0.wireOp",EDGE,"E7.9.0"),sQuery(id+"F0.wireOp",EDGE,"E7.9.1"),sQuery(id+"F0.wireOp",EDGE,"E7.9.2"),sQuery(id+"F0.wireOp",EDGE,"E7.9.3"),sQuery(id+"F0.wireOp",EDGE,"E7.10.0"),sQuery(id+"F0.wireOp",EDGE,"E7.10.1"),sQuery(id+"F0.wireOp",EDGE,"E7.10.2"),sQuery(id+"F0.wireOp",EDGE,"E7.10.3"),sQuery(id+"F0.wireOp",EDGE,"E7.11.0"),sQuery(id+"F0.wireOp",EDGE,"E7.11.1"),sQuery(id+"F0.wireOp",EDGE,"E7.11.2"),sQuery(id+"F0.wireOp",EDGE,"E7.11.3"),sQuery(id+"F0.wireOp",EDGE,"E7.12.0"),sQuery(id+"F0.wireOp",EDGE,"E7.12.1"),sQuery(id+"F0.wireOp",EDGE,"E7.12.2"),sQuery(id+"F0.wireOp",EDGE,"E7.12.3"),sQuery(id+"F0.wireOp",EDGE,"E7.13.0"),sQuery(id+"F0.wireOp",EDGE,"E7.13.1"),sQuery(id+"F0.wireOp",EDGE,"E7.13.2"),sQuery(id+"F0.wireOp",EDGE,"E7.13.3"),sQuery(id+"F0.wireOp",EDGE,"E7.14.0"),sQuery(id+"F0.wireOp",EDGE,"E7.14.1"),sQuery(id+"F0.wireOp",EDGE,"E7.14.2"),sQuery(id+"F0.wireOp",EDGE,"E7.14.3"),sQuery(id+"F0.wireOp",EDGE,"E7.15.0"),sQuery(id+"F0.wireOp",EDGE,"E7.15.1"),sQuery(id+"F0.wireOp",EDGE,"E7.15.2"),sQuery(id+"F0.wireOp",EDGE,"E7.15.3"),sQuery(id+"F0.wireOp",EDGE,"E7.16.0"),sQuery(id+"F0.wireOp",EDGE,"E7.16.1"),sQuery(id+"F0.wireOp",EDGE,"E7.16.2"),sQuery(id+"F0.wireOp",EDGE,"E7.16.3"),sQuery(id+"F0.wireOp",EDGE,"E7.17.0"),sQuery(id+"F0.wireOp",EDGE,"E7.17.1"),sQuery(id+"F0.wireOp",EDGE,"E7.17.2"),sQuery(id+"F0.wireOp",EDGE,"E7.17.3"),sQuery(id+"F0.wireOp",EDGE,"E7.18.0"),sQuery(id+"F0.wireOp",EDGE,"E7.18.1"),sQuery(id+"F0.wireOp",EDGE,"E7.18.2"),sQuery(id+"F0.wireOp",EDGE,"E7.18.3"),sQuery(id+"F0.wireOp",EDGE,"E7.19.0"),sQuery(id+"F0.wireOp",EDGE,"E7.19.1"),sQuery(id+"F0.wireOp",EDGE,"E7.19.2"),sQuery(id+"F0.wireOp",EDGE,"E7.19.3"),sQuery(id+"F0.wireOp",EDGE,"E7.20.0"),sQuery(id+"F0.wireOp",EDGE,"E7.20.1"),sQuery(id+"F0.wireOp",EDGE,"E7.20.2"),sQuery(id+"F0.wireOp",EDGE,"E7.20.3"),sQuery(id+"F0.wireOp",EDGE,"E7.21.0"),sQuery(id+"F0.wireOp",EDGE,"E7.21.1"),sQuery(id+"F0.wireOp",EDGE,"E7.21.2"),sQuery(id+"F0.wireOp",EDGE,"E7.21.3"),sQuery(id+"F0.wireOp",EDGE,"E7.22.0"),sQuery(id+"F0.wireOp",EDGE,"E7.22.1"),sQuery(id+"F0.wireOp",EDGE,"E7.22.2"),sQuery(id+"F0.wireOp",EDGE,"E7.22.3"),sQuery(id+"F0.wireOp",EDGE,"E7.23.0"),sQuery(id+"F0.wireOp",EDGE,"E7.23.1"),sQuery(id+"F0.wireOp",EDGE,"E7.23.2"),sQuery(id+"F0.wireOp",EDGE,"E7.23.3"),sQuery(id+"F0.wireOp",EDGE,"E7.24.0"),sQuery(id+"F0.wireOp",EDGE,"E7.24.1"),sQuery(id+"F0.wireOp",EDGE,"E7.24.2"),sQuery(id+"F0.wireOp",EDGE,"E7.24.3"),sQuery(id+"F0.wireOp",EDGE,"E7.25.0"),sQuery(id+"F0.wireOp",EDGE,"E7.25.1"),sQuery(id+"F0.wireOp",EDGE,"E7.25.2"),sQuery(id+"F0.wireOp",EDGE,"E7.25.3"),sQuery(id+"F0.wireOp",EDGE,"E7.26.0"),sQuery(id+"F0.wireOp",EDGE,"E7.26.1"),sQuery(id+"F0.wireOp",EDGE,"E7.26.2"),sQuery(id+"F0.wireOp",EDGE,"E7.26.3"),sQuery(id+"F0.wireOp",EDGE,"E7.27.0"),sQuery(id+"F0.wireOp",EDGE,"E7.27.1"),sQuery(id+"F0.wireOp",EDGE,"E7.27.2"),sQuery(id+"F0.wireOp",EDGE,"E7.27.3"),sQuery(id+"F0.wireOp",EDGE,"E7.28.0"),sQuery(id+"F0.wireOp",EDGE,"E7.28.1"),sQuery(id+"F0.wireOp",EDGE,"E7.28.2"),sQuery(id+"F0.wireOp",EDGE,"E7.28.3"),sQuery(id+"F0.wireOp",EDGE,"E7.29.0"),sQuery(id+"F0.wireOp",EDGE,"E7.29.1"),sQuery(id+"F0.wireOp",EDGE,"E7.29.2"),sQuery(id+"F0.wireOp",EDGE,"E7.29.3")])]});
            transform(context, id + "F4", {"entities" : qUnion([Q0]), "transformType" : TransformType.TRANSLATION_3D, "dx" : 0 * mm, "dy" : 0 * mm, "dz" : 76.2 * mm, "makeCopy" : true});
        }
        {
            var Q0;
            Q0=makeQuery(id+"F4.opPattern","COPY",EDGE,{"derivedFrom":makeQuery(id+"F2.opExtrude","SWEPT_EDGE",EDGE,{"disambiguationData":[OSD([sQuery(id+"F0.wireOp",EDGE,"E7.1.2"),sQuery(id+"F0.wireOp",EDGE,"E7.1.3")])]}),"instanceName":"1"});
            var Q1;
            Q1=makeQuery(id+"F4.opPattern","COPY",EDGE,{"derivedFrom":makeQuery(id+"F2.opExtrude","SWEPT_EDGE",EDGE,{"disambiguationData":[OSD([sQuery(id+"F0.wireOp",EDGE,"E7.2.2"),sQuery(id+"F0.wireOp",EDGE,"E7.2.3")])]}),"instanceName":"1"});
            var Q2;
            Q2=makeQuery(id+"F4.opPattern","COPY",EDGE,{"derivedFrom":makeQuery(id+"F2.opExtrude","SWEPT_EDGE",EDGE,{"disambiguationData":[OSD([sQuery(id+"F0.wireOp",EDGE,"E7.3.2"),sQuery(id+"F0.wireOp",EDGE,"E7.3.3")])]}),"instanceName":"1"});
            var Q3;
            Q3=makeQuery(id+"F4.opPattern","COPY",EDGE,{"derivedFrom":makeQuery(id+"F2.opExtrude","SWEPT_EDGE",EDGE,{"disambiguationData":[OSD([sQuery(id+"F0.wireOp",EDGE,"E7.4.2"),sQuery(id+"F0.wireOp",EDGE,"E7.4.3")])]}),"instanceName":"1"});
            var Q4;
            Q4=makeQuery(id+"F4.opPattern","COPY",EDGE,{"derivedFrom":makeQuery(id+"F2.opExtrude","SWEPT_EDGE",EDGE,{"disambiguationData":[OSD([sQuery(id+"F0.wireOp",EDGE,"kblbpXZE-b2Sg-FZdv-FlMF-ZwbeqijesS82"),sQuery(id+"F0.wireOp",EDGE,"E5")])]}),"instanceName":"1"});
            var Q5;
            Q5=makeQuery(id+"F4.opPattern","COPY",EDGE,{"derivedFrom":makeQuery(id+"F2.opExtrude","SWEPT_EDGE",EDGE,{"disambiguationData":[OSD([sQuery(id+"F0.wireOp",EDGE,"E7.29.2"),sQuery(id+"F0.wireOp",EDGE,"E7.29.3")])]}),"instanceName":"1"});
            var Q6;
            Q6=makeQuery(id+"F4.opPattern","COPY",EDGE,{"derivedFrom":makeQuery(id+"F2.opExtrude","SWEPT_EDGE",EDGE,{"disambiguationData":[OSD([sQuery(id+"F0.wireOp",EDGE,"E7.28.2"),sQuery(id+"F0.wireOp",EDGE,"E7.28.3")])]}),"instanceName":"1"});
            var Q7;
            Q7=makeQuery(id+"F4.opPattern","COPY",EDGE,{"derivedFrom":makeQuery(id+"F2.opExtrude","SWEPT_EDGE",EDGE,{"disambiguationData":[OSD([sQuery(id+"F0.wireOp",EDGE,"E7.27.2"),sQuery(id+"F0.wireOp",EDGE,"E7.27.3")])]}),"instanceName":"1"});
            var Q8;
            Q8=makeQuery(id+"F4.opPattern","COPY",EDGE,{"derivedFrom":makeQuery(id+"F2.opExtrude","SWEPT_EDGE",EDGE,{"disambiguationData":[OSD([sQuery(id+"F0.wireOp",EDGE,"E7.26.2"),sQuery(id+"F0.wireOp",EDGE,"E7.26.3")])]}),"instanceName":"1"});
            var Q9;
            Q9=makeQuery(id+"F4.opPattern","COPY",EDGE,{"derivedFrom":makeQuery(id+"F2.opExtrude","SWEPT_EDGE",EDGE,{"disambiguationData":[OSD([sQuery(id+"F0.wireOp",EDGE,"E7.5.2"),sQuery(id+"F0.wireOp",EDGE,"E7.5.3")])]}),"instanceName":"1"});
            var Q10;
            Q10=makeQuery(id+"F4.opPattern","COPY",EDGE,{"derivedFrom":makeQuery(id+"F2.opExtrude","SWEPT_EDGE",EDGE,{"disambiguationData":[OSD([sQuery(id+"F0.wireOp",EDGE,"E7.6.2"),sQuery(id+"F0.wireOp",EDGE,"E7.6.3")])]}),"instanceName":"1"});
            var Q11;
            Q11=makeQuery(id+"F4.opPattern","COPY",EDGE,{"derivedFrom":makeQuery(id+"F2.opExtrude","SWEPT_EDGE",EDGE,{"disambiguationData":[OSD([sQuery(id+"F0.wireOp",EDGE,"E7.7.2"),sQuery(id+"F0.wireOp",EDGE,"E7.7.3")])]}),"instanceName":"1"});
            var Q12;
            Q12=makeQuery(id+"F4.opPattern","COPY",EDGE,{"derivedFrom":makeQuery(id+"F2.opExtrude","SWEPT_EDGE",EDGE,{"disambiguationData":[OSD([sQuery(id+"F0.wireOp",EDGE,"E7.25.2"),sQuery(id+"F0.wireOp",EDGE,"E7.25.3")])]}),"instanceName":"1"});
            var Q13;
            Q13=makeQuery(id+"F4.opPattern","COPY",EDGE,{"derivedFrom":makeQuery(id+"F2.opExtrude","SWEPT_EDGE",EDGE,{"disambiguationData":[OSD([sQuery(id+"F0.wireOp",EDGE,"E7.24.2"),sQuery(id+"F0.wireOp",EDGE,"E7.24.3")])]}),"instanceName":"1"});
            var Q14;
            Q14=makeQuery(id+"F4.opPattern","COPY",EDGE,{"derivedFrom":makeQuery(id+"F2.opExtrude","SWEPT_EDGE",EDGE,{"disambiguationData":[OSD([sQuery(id+"F0.wireOp",EDGE,"E7.23.2"),sQuery(id+"F0.wireOp",EDGE,"E7.23.3")])]}),"instanceName":"1"});
            var Q15;
            Q15=makeQuery(id+"F4.opPattern","COPY",EDGE,{"derivedFrom":makeQuery(id+"F2.opExtrude","SWEPT_EDGE",EDGE,{"disambiguationData":[OSD([sQuery(id+"F0.wireOp",EDGE,"E7.8.2"),sQuery(id+"F0.wireOp",EDGE,"E7.8.3")])]}),"instanceName":"1"});
            var Q16;
            Q16=makeQuery(id+"F4.opPattern","COPY",EDGE,{"derivedFrom":makeQuery(id+"F2.opExtrude","SWEPT_EDGE",EDGE,{"disambiguationData":[OSD([sQuery(id+"F0.wireOp",EDGE,"E7.22.2"),sQuery(id+"F0.wireOp",EDGE,"E7.22.3")])]}),"instanceName":"1"});
            var Q17;
            Q17=makeQuery(id+"F4.opPattern","COPY",EDGE,{"derivedFrom":makeQuery(id+"F2.opExtrude","SWEPT_EDGE",EDGE,{"disambiguationData":[OSD([sQuery(id+"F0.wireOp",EDGE,"E7.21.2"),sQuery(id+"F0.wireOp",EDGE,"E7.21.3")])]}),"instanceName":"1"});
            var Q18;
            Q18=makeQuery(id+"F4.opPattern","COPY",EDGE,{"derivedFrom":makeQuery(id+"F2.opExtrude","SWEPT_EDGE",EDGE,{"disambiguationData":[OSD([sQuery(id+"F0.wireOp",EDGE,"E7.9.2"),sQuery(id+"F0.wireOp",EDGE,"E7.9.3")])]}),"instanceName":"1"});
            var Q19;
            Q19=makeQuery(id+"F4.opPattern","COPY",EDGE,{"derivedFrom":makeQuery(id+"F2.opExtrude","SWEPT_EDGE",EDGE,{"disambiguationData":[OSD([sQuery(id+"F0.wireOp",EDGE,"E7.10.2"),sQuery(id+"F0.wireOp",EDGE,"E7.10.3")])]}),"instanceName":"1"});
            var Q20;
            Q20=makeQuery(id+"F4.opPattern","COPY",EDGE,{"derivedFrom":makeQuery(id+"F2.opExtrude","SWEPT_EDGE",EDGE,{"disambiguationData":[OSD([sQuery(id+"F0.wireOp",EDGE,"E7.11.2"),sQuery(id+"F0.wireOp",EDGE,"E7.11.3")])]}),"instanceName":"1"});
            var Q21;
            Q21=makeQuery(id+"F4.opPattern","COPY",EDGE,{"derivedFrom":makeQuery(id+"F2.opExtrude","SWEPT_EDGE",EDGE,{"disambiguationData":[OSD([sQuery(id+"F0.wireOp",EDGE,"E7.12.2"),sQuery(id+"F0.wireOp",EDGE,"E7.12.3")])]}),"instanceName":"1"});
            var Q22;
            Q22=makeQuery(id+"F4.opPattern","COPY",EDGE,{"derivedFrom":makeQuery(id+"F2.opExtrude","SWEPT_EDGE",EDGE,{"disambiguationData":[OSD([sQuery(id+"F0.wireOp",EDGE,"E7.13.2"),sQuery(id+"F0.wireOp",EDGE,"E7.13.3")])]}),"instanceName":"1"});
            var Q23;
            Q23=makeQuery(id+"F4.opPattern","COPY",EDGE,{"derivedFrom":makeQuery(id+"F2.opExtrude","SWEPT_EDGE",EDGE,{"disambiguationData":[OSD([sQuery(id+"F0.wireOp",EDGE,"E7.14.2"),sQuery(id+"F0.wireOp",EDGE,"E7.14.3")])]}),"instanceName":"1"});
            var Q24;
            Q24=makeQuery(id+"F4.opPattern","COPY",EDGE,{"derivedFrom":makeQuery(id+"F2.opExtrude","SWEPT_EDGE",EDGE,{"disambiguationData":[OSD([sQuery(id+"F0.wireOp",EDGE,"E7.15.2"),sQuery(id+"F0.wireOp",EDGE,"E7.15.3")])]}),"instanceName":"1"});
            var Q25;
            Q25=makeQuery(id+"F4.opPattern","COPY",EDGE,{"derivedFrom":makeQuery(id+"F2.opExtrude","SWEPT_EDGE",EDGE,{"disambiguationData":[OSD([sQuery(id+"F0.wireOp",EDGE,"E7.16.2"),sQuery(id+"F0.wireOp",EDGE,"E7.16.3")])]}),"instanceName":"1"});
            var Q26;
            Q26=makeQuery(id+"F4.opPattern","COPY",EDGE,{"derivedFrom":makeQuery(id+"F2.opExtrude","SWEPT_EDGE",EDGE,{"disambiguationData":[OSD([sQuery(id+"F0.wireOp",EDGE,"E7.17.2"),sQuery(id+"F0.wireOp",EDGE,"E7.17.3")])]}),"instanceName":"1"});
            var Q27;
            Q27=makeQuery(id+"F4.opPattern","COPY",EDGE,{"derivedFrom":makeQuery(id+"F2.opExtrude","SWEPT_EDGE",EDGE,{"disambiguationData":[OSD([sQuery(id+"F0.wireOp",EDGE,"E7.18.2"),sQuery(id+"F0.wireOp",EDGE,"E7.18.3")])]}),"instanceName":"1"});
            var Q28;
            Q28=makeQuery(id+"F4.opPattern","COPY",EDGE,{"derivedFrom":makeQuery(id+"F2.opExtrude","SWEPT_EDGE",EDGE,{"disambiguationData":[OSD([sQuery(id+"F0.wireOp",EDGE,"E7.19.2"),sQuery(id+"F0.wireOp",EDGE,"E7.19.3")])]}),"instanceName":"1"});
            var Q29;
            Q29=makeQuery(id+"F4.opPattern","COPY",EDGE,{"derivedFrom":makeQuery(id+"F2.opExtrude","SWEPT_EDGE",EDGE,{"disambiguationData":[OSD([sQuery(id+"F0.wireOp",EDGE,"E7.20.2"),sQuery(id+"F0.wireOp",EDGE,"E7.20.3")])]}),"instanceName":"1"});
            var Q30;
            Q30=makeQuery(id+"F4.opPattern","COPY",EDGE,{"derivedFrom":makeQuery(id+"F2.opExtrude","SWEPT_EDGE",EDGE,{"disambiguationData":[OSD([sQuery(id+"F0.wireOp",EDGE,"E9"),sQuery(id+"F0.wireOp",EDGE,"E12")])]}),"instanceName":"1"});
            fillet(context, id + "F5", {"entities" : qUnion([Q0, Q1, Q2, Q3, Q4, Q5, Q6, Q7, Q8, Q9, Q10, Q11, Q12, Q13, Q14, Q15, Q16, Q17, Q18, Q19, Q20, Q21, Q22, Q23, Q24, Q25, Q26, Q27, Q28, Q29, Q30]), "radius" : 0.64 * mm, "tangentPropagation" : true, "allowEdgeOverflow" : false});
        }
        {
            var Q0;
            Q0=makeQuery(id+"F2.opExtrude","SWEPT_EDGE",EDGE,{"disambiguationData":[OSD([sQuery(id+"F0.wireOp",EDGE,"E7.16.0"),sQuery(id+"F0.wireOp",EDGE,"E7.16.1")])]});
            var Q1;
            Q1=makeQuery(id+"F2.opExtrude","SWEPT_EDGE",EDGE,{"disambiguationData":[OSD([sQuery(id+"F0.wireOp",EDGE,"E7.17.0"),sQuery(id+"F0.wireOp",EDGE,"E7.17.1")])]});
            var Q2;
            Q2=makeQuery(id+"F2.opExtrude","SWEPT_EDGE",EDGE,{"disambiguationData":[OSD([sQuery(id+"F0.wireOp",EDGE,"E7.18.0"),sQuery(id+"F0.wireOp",EDGE,"E7.18.1")])]});
            var Q3;
            Q3=makeQuery(id+"F2.opExtrude","SWEPT_EDGE",EDGE,{"disambiguationData":[OSD([sQuery(id+"F0.wireOp",EDGE,"E7.19.0"),sQuery(id+"F0.wireOp",EDGE,"E7.19.1")])]});
            var Q4;
            Q4=makeQuery(id+"F2.opExtrude","SWEPT_EDGE",EDGE,{"disambiguationData":[OSD([sQuery(id+"F0.wireOp",EDGE,"E7.20.0"),sQuery(id+"F0.wireOp",EDGE,"E7.20.1")])]});
            var Q5;
            Q5=makeQuery(id+"F2.opExtrude","SWEPT_EDGE",EDGE,{"disambiguationData":[OSD([sQuery(id+"F0.wireOp",EDGE,"E7.14.0"),sQuery(id+"F0.wireOp",EDGE,"E7.14.1")])]});
            var Q6;
            Q6=makeQuery(id+"F2.opExtrude","SWEPT_EDGE",EDGE,{"disambiguationData":[OSD([sQuery(id+"F0.wireOp",EDGE,"E7.13.0"),sQuery(id+"F0.wireOp",EDGE,"E7.13.1")])]});
            var Q7;
            Q7=makeQuery(id+"F2.opExtrude","SWEPT_EDGE",EDGE,{"disambiguationData":[OSD([sQuery(id+"F0.wireOp",EDGE,"E7.12.0"),sQuery(id+"F0.wireOp",EDGE,"E7.12.1")])]});
            var Q8;
            Q8=makeQuery(id+"F2.opExtrude","SWEPT_EDGE",EDGE,{"disambiguationData":[OSD([sQuery(id+"F0.wireOp",EDGE,"E7.11.0"),sQuery(id+"F0.wireOp",EDGE,"E7.11.1")])]});
            var Q9;
            Q9=makeQuery(id+"F2.opExtrude","SWEPT_EDGE",EDGE,{"disambiguationData":[OSD([sQuery(id+"F0.wireOp",EDGE,"E7.10.0"),sQuery(id+"F0.wireOp",EDGE,"E7.10.1")])]});
            var Q10;
            Q10=makeQuery(id+"F2.opExtrude","SWEPT_EDGE",EDGE,{"disambiguationData":[OSD([sQuery(id+"F0.wireOp",EDGE,"E7.9.0"),sQuery(id+"F0.wireOp",EDGE,"E7.9.1")])]});
            var Q11;
            Q11=makeQuery(id+"F2.opExtrude","SWEPT_EDGE",EDGE,{"disambiguationData":[OSD([sQuery(id+"F0.wireOp",EDGE,"E7.8.0"),sQuery(id+"F0.wireOp",EDGE,"E7.8.1")])]});
            var Q12;
            Q12=makeQuery(id+"F2.opExtrude","SWEPT_EDGE",EDGE,{"disambiguationData":[OSD([sQuery(id+"F0.wireOp",EDGE,"E7.15.0"),sQuery(id+"F0.wireOp",EDGE,"E7.15.1")])]});
            var Q13;
            Q13=makeQuery(id+"F2.opExtrude","SWEPT_EDGE",EDGE,{"disambiguationData":[OSD([sQuery(id+"F0.wireOp",EDGE,"E7.21.0"),sQuery(id+"F0.wireOp",EDGE,"E7.21.1")])]});
            var Q14;
            Q14=makeQuery(id+"F2.opExtrude","SWEPT_EDGE",EDGE,{"disambiguationData":[OSD([sQuery(id+"F0.wireOp",EDGE,"E7.7.0"),sQuery(id+"F0.wireOp",EDGE,"E7.7.1")])]});
            var Q15;
            Q15=makeQuery(id+"F2.opExtrude","SWEPT_EDGE",EDGE,{"disambiguationData":[OSD([sQuery(id+"F0.wireOp",EDGE,"E7.22.0"),sQuery(id+"F0.wireOp",EDGE,"E7.22.1")])]});
            var Q16;
            Q16=makeQuery(id+"F2.opExtrude","SWEPT_EDGE",EDGE,{"disambiguationData":[OSD([sQuery(id+"F0.wireOp",EDGE,"E7.23.0"),sQuery(id+"F0.wireOp",EDGE,"E7.23.1")])]});
            var Q17;
            Q17=makeQuery(id+"F2.opExtrude","SWEPT_EDGE",EDGE,{"disambiguationData":[OSD([sQuery(id+"F0.wireOp",EDGE,"E7.6.0"),sQuery(id+"F0.wireOp",EDGE,"E7.6.1")])]});
            var Q18;
            Q18=makeQuery(id+"F2.opExtrude","SWEPT_EDGE",EDGE,{"disambiguationData":[OSD([sQuery(id+"F0.wireOp",EDGE,"E7.5.0"),sQuery(id+"F0.wireOp",EDGE,"E7.5.1")])]});
            var Q19;
            Q19=makeQuery(id+"F2.opExtrude","SWEPT_EDGE",EDGE,{"disambiguationData":[OSD([sQuery(id+"F0.wireOp",EDGE,"E7.4.0"),sQuery(id+"F0.wireOp",EDGE,"E7.4.1")])]});
            var Q20;
            Q20=makeQuery(id+"F2.opExtrude","SWEPT_EDGE",EDGE,{"disambiguationData":[OSD([sQuery(id+"F0.wireOp",EDGE,"E7.3.0"),sQuery(id+"F0.wireOp",EDGE,"E7.3.1")])]});
            var Q21;
            Q21=makeQuery(id+"F2.opExtrude","SWEPT_EDGE",EDGE,{"disambiguationData":[OSD([sQuery(id+"F0.wireOp",EDGE,"E7.2.0"),sQuery(id+"F0.wireOp",EDGE,"E7.2.1")])]});
            var Q22;
            Q22=makeQuery(id+"F2.opExtrude","SWEPT_EDGE",EDGE,{"disambiguationData":[OSD([sQuery(id+"F0.wireOp",EDGE,"E7.1.0"),sQuery(id+"F0.wireOp",EDGE,"E7.1.1")])]});
            var Q23;
            Q23=makeQuery(id+"F2.opExtrude","SWEPT_EDGE",EDGE,{"disambiguationData":[OSD([sQuery(id+"F0.wireOp",EDGE,"E7.29.0"),sQuery(id+"F0.wireOp",EDGE,"E7.29.1")])]});
            var Q24;
            Q24=makeQuery(id+"F2.opExtrude","SWEPT_EDGE",EDGE,{"disambiguationData":[OSD([sQuery(id+"F0.wireOp",EDGE,"E7.28.0"),sQuery(id+"F0.wireOp",EDGE,"E7.28.1")])]});
            var Q25;
            Q25=makeQuery(id+"F2.opExtrude","SWEPT_EDGE",EDGE,{"disambiguationData":[OSD([sQuery(id+"F0.wireOp",EDGE,"E7.27.0"),sQuery(id+"F0.wireOp",EDGE,"E7.27.1")])]});
            var Q26;
            Q26=makeQuery(id+"F2.opExtrude","SWEPT_EDGE",EDGE,{"disambiguationData":[OSD([sQuery(id+"F0.wireOp",EDGE,"E7.26.0"),sQuery(id+"F0.wireOp",EDGE,"E7.26.1")])]});
            var Q27;
            Q27=makeQuery(id+"F2.opExtrude","SWEPT_EDGE",EDGE,{"disambiguationData":[OSD([sQuery(id+"F0.wireOp",EDGE,"E2"),sQuery(id+"F0.wireOp",EDGE,"E7.26.3")])]});
            var Q28;
            Q28=makeQuery(id+"F2.opExtrude","SWEPT_EDGE",EDGE,{"disambiguationData":[OSD([sQuery(id+"F0.wireOp",EDGE,"E4"),sQuery(id+"F0.wireOp",EDGE,"E6")])]});
            var Q29;
            Q29=makeQuery(id+"F2.opExtrude","SWEPT_EDGE",EDGE,{"disambiguationData":[OSD([sQuery(id+"F0.wireOp",EDGE,"E7.24.0"),sQuery(id+"F0.wireOp",EDGE,"E7.24.1")])]});
            var Q30;
            Q30=makeQuery(id+"F2.opExtrude","SWEPT_EDGE",EDGE,{"disambiguationData":[OSD([sQuery(id+"F0.wireOp",EDGE,"E7.25.0"),sQuery(id+"F0.wireOp",EDGE,"E7.25.1")])]});
            fillet(context, id + "F6", {"entities" : qUnion([Q0, Q1, Q2, Q3, Q4, Q5, Q6, Q7, Q8, Q9, Q10, Q11, Q12, Q13, Q14, Q15, Q16, Q17, Q18, Q19, Q20, Q21, Q22, Q23, Q24, Q25, Q26, Q27, Q28, Q29, Q30]), "radius" : 0.5 * mm, "tangentPropagation" : true, "allowEdgeOverflow" : false});
        }
        {
            var Q0;
            Q0=makeQuery(id+"F4.opPattern","COPY",EDGE,{"derivedFrom":makeQuery(id+"F2.opExtrude","SWEPT_EDGE",EDGE,{"disambiguationData":[OSD([sQuery(id+"F0.wireOp",EDGE,"E7.1.0"),sQuery(id+"F0.wireOp",EDGE,"E7.1.1")])]}),"instanceName":"1"});
            var Q1;
            Q1=makeQuery(id+"F4.opPattern","COPY",EDGE,{"derivedFrom":makeQuery(id+"F2.opExtrude","SWEPT_EDGE",EDGE,{"disambiguationData":[OSD([sQuery(id+"F0.wireOp",EDGE,"E7.2.0"),sQuery(id+"F0.wireOp",EDGE,"E7.2.1")])]}),"instanceName":"1"});
            var Q2;
            Q2=makeQuery(id+"F4.opPattern","COPY",EDGE,{"derivedFrom":makeQuery(id+"F2.opExtrude","SWEPT_EDGE",EDGE,{"disambiguationData":[OSD([sQuery(id+"F0.wireOp",EDGE,"E7.3.0"),sQuery(id+"F0.wireOp",EDGE,"E7.3.1")])]}),"instanceName":"1"});
            var Q3;
            Q3=makeQuery(id+"F4.opPattern","COPY",EDGE,{"derivedFrom":makeQuery(id+"F2.opExtrude","SWEPT_EDGE",EDGE,{"disambiguationData":[OSD([sQuery(id+"F0.wireOp",EDGE,"E7.4.0"),sQuery(id+"F0.wireOp",EDGE,"E7.4.1")])]}),"instanceName":"1"});
            var Q4;
            Q4=makeQuery(id+"F4.opPattern","COPY",EDGE,{"derivedFrom":makeQuery(id+"F2.opExtrude","SWEPT_EDGE",EDGE,{"disambiguationData":[OSD([sQuery(id+"F0.wireOp",EDGE,"E7.29.0"),sQuery(id+"F0.wireOp",EDGE,"E7.29.1")])]}),"instanceName":"1"});
            var Q5;
            Q5=makeQuery(id+"F4.opPattern","COPY",EDGE,{"derivedFrom":makeQuery(id+"F2.opExtrude","SWEPT_EDGE",EDGE,{"disambiguationData":[OSD([sQuery(id+"F0.wireOp",EDGE,"E7.28.0"),sQuery(id+"F0.wireOp",EDGE,"E7.28.1")])]}),"instanceName":"1"});
            var Q6;
            Q6=makeQuery(id+"F4.opPattern","COPY",EDGE,{"derivedFrom":makeQuery(id+"F2.opExtrude","SWEPT_EDGE",EDGE,{"disambiguationData":[OSD([sQuery(id+"F0.wireOp",EDGE,"E4"),sQuery(id+"F0.wireOp",EDGE,"E6")])]}),"instanceName":"1"});
            var Q7;
            Q7=makeQuery(id+"F4.opPattern","COPY",EDGE,{"derivedFrom":makeQuery(id+"F2.opExtrude","SWEPT_EDGE",EDGE,{"disambiguationData":[OSD([sQuery(id+"F0.wireOp",EDGE,"E7.27.0"),sQuery(id+"F0.wireOp",EDGE,"E7.27.1")])]}),"instanceName":"1"});
            var Q8;
            Q8=makeQuery(id+"F4.opPattern","COPY",EDGE,{"derivedFrom":makeQuery(id+"F2.opExtrude","SWEPT_EDGE",EDGE,{"disambiguationData":[OSD([sQuery(id+"F0.wireOp",EDGE,"E7.26.0"),sQuery(id+"F0.wireOp",EDGE,"E7.26.1")])]}),"instanceName":"1"});
            var Q9;
            Q9=makeQuery(id+"F4.opPattern","COPY",EDGE,{"derivedFrom":makeQuery(id+"F2.opExtrude","SWEPT_EDGE",EDGE,{"disambiguationData":[OSD([sQuery(id+"F0.wireOp",EDGE,"E2"),sQuery(id+"F0.wireOp",EDGE,"E7.5.3")])]}),"instanceName":"1"});
            var Q10;
            Q10=makeQuery(id+"F4.opPattern","COPY",EDGE,{"derivedFrom":makeQuery(id+"F2.opExtrude","SWEPT_EDGE",EDGE,{"disambiguationData":[OSD([sQuery(id+"F0.wireOp",EDGE,"E7.5.0"),sQuery(id+"F0.wireOp",EDGE,"E7.5.1")])]}),"instanceName":"1"});
            var Q11;
            Q11=makeQuery(id+"F4.opPattern","COPY",EDGE,{"derivedFrom":makeQuery(id+"F2.opExtrude","SWEPT_EDGE",EDGE,{"disambiguationData":[OSD([sQuery(id+"F0.wireOp",EDGE,"E7.6.0"),sQuery(id+"F0.wireOp",EDGE,"E7.6.1")])]}),"instanceName":"1"});
            var Q12;
            Q12=makeQuery(id+"F4.opPattern","COPY",EDGE,{"derivedFrom":makeQuery(id+"F2.opExtrude","SWEPT_EDGE",EDGE,{"disambiguationData":[OSD([sQuery(id+"F0.wireOp",EDGE,"E7.7.0"),sQuery(id+"F0.wireOp",EDGE,"E7.7.1")])]}),"instanceName":"1"});
            var Q13;
            Q13=makeQuery(id+"F4.opPattern","COPY",EDGE,{"derivedFrom":makeQuery(id+"F2.opExtrude","SWEPT_EDGE",EDGE,{"disambiguationData":[OSD([sQuery(id+"F0.wireOp",EDGE,"E7.8.0"),sQuery(id+"F0.wireOp",EDGE,"E7.8.1")])]}),"instanceName":"1"});
            var Q14;
            Q14=makeQuery(id+"F4.opPattern","COPY",EDGE,{"derivedFrom":makeQuery(id+"F2.opExtrude","SWEPT_EDGE",EDGE,{"disambiguationData":[OSD([sQuery(id+"F0.wireOp",EDGE,"E7.9.0"),sQuery(id+"F0.wireOp",EDGE,"E7.9.1")])]}),"instanceName":"1"});
            var Q15;
            Q15=makeQuery(id+"F4.opPattern","COPY",EDGE,{"derivedFrom":makeQuery(id+"F2.opExtrude","SWEPT_EDGE",EDGE,{"disambiguationData":[OSD([sQuery(id+"F0.wireOp",EDGE,"E7.10.0"),sQuery(id+"F0.wireOp",EDGE,"E7.10.1")])]}),"instanceName":"1"});
            var Q16;
            Q16=makeQuery(id+"F4.opPattern","COPY",EDGE,{"derivedFrom":makeQuery(id+"F2.opExtrude","SWEPT_EDGE",EDGE,{"disambiguationData":[OSD([sQuery(id+"F0.wireOp",EDGE,"E7.11.0"),sQuery(id+"F0.wireOp",EDGE,"E7.11.1")])]}),"instanceName":"1"});
            var Q17;
            Q17=makeQuery(id+"F4.opPattern","COPY",EDGE,{"derivedFrom":makeQuery(id+"F2.opExtrude","SWEPT_EDGE",EDGE,{"disambiguationData":[OSD([sQuery(id+"F0.wireOp",EDGE,"E7.12.0"),sQuery(id+"F0.wireOp",EDGE,"E7.12.1")])]}),"instanceName":"1"});
            var Q18;
            Q18=makeQuery(id+"F4.opPattern","COPY",EDGE,{"derivedFrom":makeQuery(id+"F2.opExtrude","SWEPT_EDGE",EDGE,{"disambiguationData":[OSD([sQuery(id+"F0.wireOp",EDGE,"E7.13.0"),sQuery(id+"F0.wireOp",EDGE,"E7.13.1")])]}),"instanceName":"1"});
            var Q19;
            Q19=makeQuery(id+"F4.opPattern","COPY",EDGE,{"derivedFrom":makeQuery(id+"F2.opExtrude","SWEPT_EDGE",EDGE,{"disambiguationData":[OSD([sQuery(id+"F0.wireOp",EDGE,"E7.14.0"),sQuery(id+"F0.wireOp",EDGE,"E7.14.1")])]}),"instanceName":"1"});
            var Q20;
            Q20=makeQuery(id+"F4.opPattern","COPY",EDGE,{"derivedFrom":makeQuery(id+"F2.opExtrude","SWEPT_EDGE",EDGE,{"disambiguationData":[OSD([sQuery(id+"F0.wireOp",EDGE,"E7.15.0"),sQuery(id+"F0.wireOp",EDGE,"E7.15.1")])]}),"instanceName":"1"});
            var Q21;
            Q21=makeQuery(id+"F4.opPattern","COPY",EDGE,{"derivedFrom":makeQuery(id+"F2.opExtrude","SWEPT_EDGE",EDGE,{"disambiguationData":[OSD([sQuery(id+"F0.wireOp",EDGE,"E7.16.0"),sQuery(id+"F0.wireOp",EDGE,"E7.16.1")])]}),"instanceName":"1"});
            var Q22;
            Q22=makeQuery(id+"F4.opPattern","COPY",EDGE,{"derivedFrom":makeQuery(id+"F2.opExtrude","SWEPT_EDGE",EDGE,{"disambiguationData":[OSD([sQuery(id+"F0.wireOp",EDGE,"E7.17.0"),sQuery(id+"F0.wireOp",EDGE,"E7.17.1")])]}),"instanceName":"1"});
            var Q23;
            Q23=makeQuery(id+"F4.opPattern","COPY",EDGE,{"derivedFrom":makeQuery(id+"F2.opExtrude","SWEPT_EDGE",EDGE,{"disambiguationData":[OSD([sQuery(id+"F0.wireOp",EDGE,"E7.18.0"),sQuery(id+"F0.wireOp",EDGE,"E7.18.1")])]}),"instanceName":"1"});
            var Q24;
            Q24=makeQuery(id+"F4.opPattern","COPY",EDGE,{"derivedFrom":makeQuery(id+"F2.opExtrude","SWEPT_EDGE",EDGE,{"disambiguationData":[OSD([sQuery(id+"F0.wireOp",EDGE,"E7.19.0"),sQuery(id+"F0.wireOp",EDGE,"E7.19.1")])]}),"instanceName":"1"});
            var Q25;
            Q25=makeQuery(id+"F4.opPattern","COPY",EDGE,{"derivedFrom":makeQuery(id+"F2.opExtrude","SWEPT_EDGE",EDGE,{"disambiguationData":[OSD([sQuery(id+"F0.wireOp",EDGE,"E7.20.0"),sQuery(id+"F0.wireOp",EDGE,"E7.20.1")])]}),"instanceName":"1"});
            var Q26;
            Q26=makeQuery(id+"F4.opPattern","COPY",EDGE,{"derivedFrom":makeQuery(id+"F2.opExtrude","SWEPT_EDGE",EDGE,{"disambiguationData":[OSD([sQuery(id+"F0.wireOp",EDGE,"E7.21.0"),sQuery(id+"F0.wireOp",EDGE,"E7.21.1")])]}),"instanceName":"1"});
            var Q27;
            Q27=makeQuery(id+"F4.opPattern","COPY",EDGE,{"derivedFrom":makeQuery(id+"F2.opExtrude","SWEPT_EDGE",EDGE,{"disambiguationData":[OSD([sQuery(id+"F0.wireOp",EDGE,"E7.22.0"),sQuery(id+"F0.wireOp",EDGE,"E7.22.1")])]}),"instanceName":"1"});
            var Q28;
            Q28=makeQuery(id+"F4.opPattern","COPY",EDGE,{"derivedFrom":makeQuery(id+"F2.opExtrude","SWEPT_EDGE",EDGE,{"disambiguationData":[OSD([sQuery(id+"F0.wireOp",EDGE,"E7.23.0"),sQuery(id+"F0.wireOp",EDGE,"E7.23.1")])]}),"instanceName":"1"});
            var Q29;
            Q29=makeQuery(id+"F4.opPattern","COPY",EDGE,{"derivedFrom":makeQuery(id+"F2.opExtrude","SWEPT_EDGE",EDGE,{"disambiguationData":[OSD([sQuery(id+"F0.wireOp",EDGE,"E7.24.0"),sQuery(id+"F0.wireOp",EDGE,"E7.24.1")])]}),"instanceName":"1"});
            var Q30;
            Q30=makeQuery(id+"F4.opPattern","COPY",EDGE,{"derivedFrom":makeQuery(id+"F2.opExtrude","SWEPT_EDGE",EDGE,{"disambiguationData":[OSD([sQuery(id+"F0.wireOp",EDGE,"E7.25.0"),sQuery(id+"F0.wireOp",EDGE,"E7.25.1")])]}),"instanceName":"1"});
            fillet(context, id + "F7", {"entities" : qUnion([Q0, Q1, Q2, Q3, Q4, Q5, Q6, Q7, Q8, Q9, Q10, Q11, Q12, Q13, Q14, Q15, Q16, Q17, Q18, Q19, Q20, Q21, Q22, Q23, Q24, Q25, Q26, Q27, Q28, Q29, Q30]), "radius" : 0.64 * mm, "tangentPropagation" : true, "allowEdgeOverflow" : false});
        }
        {
            var Q0;
            Q0=makeQuery(id+"F2.opExtrude","SWEPT_EDGE",EDGE,{"disambiguationData":[OSD([sQuery(id+"F0.wireOp",EDGE,"E2"),sQuery(id+"F0.wireOp",EDGE,"E5")])]});
            var Q1;
            Q1=makeQuery(id+"F2.opExtrude","SWEPT_EDGE",EDGE,{"disambiguationData":[OSD([sQuery(id+"F0.wireOp",EDGE,"E2"),sQuery(id+"F0.wireOp",EDGE,"E7.1.3")])]});
            var Q2;
            Q2=makeQuery(id+"F2.opExtrude","SWEPT_EDGE",EDGE,{"disambiguationData":[OSD([sQuery(id+"F0.wireOp",EDGE,"E7.1.3"),sQuery(id+"F0.wireOp",EDGE,"E11.1.0")])]});
            var Q3;
            Q3=makeQuery(id+"F2.opExtrude","SWEPT_EDGE",EDGE,{"disambiguationData":[OSD([sQuery(id+"F0.wireOp",EDGE,"E2"),sQuery(id+"F0.wireOp",EDGE,"E7.2.3")])]});
            var Q4;
            Q4=makeQuery(id+"F2.opExtrude","SWEPT_EDGE",EDGE,{"disambiguationData":[OSD([sQuery(id+"F0.wireOp",EDGE,"E7.2.3"),sQuery(id+"F0.wireOp",EDGE,"E11.2.0")])]});
            var Q5;
            Q5=makeQuery(id+"F2.opExtrude","SWEPT_EDGE",EDGE,{"disambiguationData":[OSD([sQuery(id+"F0.wireOp",EDGE,"E2"),sQuery(id+"F0.wireOp",EDGE,"E7.3.3")])]});
            var Q6;
            Q6=makeQuery(id+"F2.opExtrude","SWEPT_EDGE",EDGE,{"disambiguationData":[OSD([sQuery(id+"F0.wireOp",EDGE,"E7.3.3"),sQuery(id+"F0.wireOp",EDGE,"E11.3.0")])]});
            var Q7;
            Q7=makeQuery(id+"F2.opExtrude","SWEPT_EDGE",EDGE,{"disambiguationData":[OSD([sQuery(id+"F0.wireOp",EDGE,"E2"),sQuery(id+"F0.wireOp",EDGE,"E7.4.3")])]});
            var Q8;
            Q8=makeQuery(id+"F2.opExtrude","SWEPT_EDGE",EDGE,{"disambiguationData":[OSD([sQuery(id+"F0.wireOp",EDGE,"E7.4.3"),sQuery(id+"F0.wireOp",EDGE,"E11.4.0")])]});
            var Q9;
            Q9=makeQuery(id+"F2.opExtrude","SWEPT_EDGE",EDGE,{"disambiguationData":[OSD([sQuery(id+"F0.wireOp",EDGE,"E2"),sQuery(id+"F0.wireOp",EDGE,"E7.29.3")])]});
            var Q10;
            Q10=makeQuery(id+"F2.opExtrude","SWEPT_EDGE",EDGE,{"disambiguationData":[OSD([sQuery(id+"F0.wireOp",EDGE,"E7.29.3"),sQuery(id+"F0.wireOp",EDGE,"E11.29.0")])]});
            var Q11;
            Q11=makeQuery(id+"F2.opExtrude","SWEPT_EDGE",EDGE,{"disambiguationData":[OSD([sQuery(id+"F0.wireOp",EDGE,"E2"),sQuery(id+"F0.wireOp",EDGE,"E7.28.3")])]});
            var Q12;
            Q12=makeQuery(id+"F2.opExtrude","SWEPT_EDGE",EDGE,{"disambiguationData":[OSD([sQuery(id+"F0.wireOp",EDGE,"E7.28.3"),sQuery(id+"F0.wireOp",EDGE,"E11.28.0")])]});
            var Q13;
            Q13=makeQuery(id+"F2.opExtrude","SWEPT_EDGE",EDGE,{"disambiguationData":[OSD([sQuery(id+"F0.wireOp",EDGE,"E2"),sQuery(id+"F0.wireOp",EDGE,"E7.27.3")])]});
            var Q14;
            Q14=makeQuery(id+"F2.opExtrude","SWEPT_EDGE",EDGE,{"disambiguationData":[OSD([sQuery(id+"F0.wireOp",EDGE,"E7.27.3"),sQuery(id+"F0.wireOp",EDGE,"E11.27.0")])]});
            var Q15;
            Q15=makeQuery(id+"F2.opExtrude","SWEPT_EDGE",EDGE,{"disambiguationData":[OSD([sQuery(id+"F0.wireOp",EDGE,"E7.26.3"),sQuery(id+"F0.wireOp",EDGE,"E11.26.0")])]});
            var Q16;
            Q16=makeQuery(id+"F2.opExtrude","SWEPT_EDGE",EDGE,{"disambiguationData":[OSD([sQuery(id+"F0.wireOp",EDGE,"E2"),sQuery(id+"F0.wireOp",EDGE,"E7.5.3")])]});
            var Q17;
            Q17=makeQuery(id+"F2.opExtrude","SWEPT_EDGE",EDGE,{"disambiguationData":[OSD([sQuery(id+"F0.wireOp",EDGE,"E7.5.3"),sQuery(id+"F0.wireOp",EDGE,"E11.5.0")])]});
            var Q18;
            Q18=makeQuery(id+"F2.opExtrude","SWEPT_EDGE",EDGE,{"disambiguationData":[OSD([sQuery(id+"F0.wireOp",EDGE,"E2"),sQuery(id+"F0.wireOp",EDGE,"E7.25.3")])]});
            var Q19;
            Q19=makeQuery(id+"F2.opExtrude","SWEPT_EDGE",EDGE,{"disambiguationData":[OSD([sQuery(id+"F0.wireOp",EDGE,"E7.25.3"),sQuery(id+"F0.wireOp",EDGE,"E11.25.0")])]});
            var Q20;
            Q20=makeQuery(id+"F2.opExtrude","SWEPT_EDGE",EDGE,{"disambiguationData":[OSD([sQuery(id+"F0.wireOp",EDGE,"E2"),sQuery(id+"F0.wireOp",EDGE,"E7.24.3")])]});
            var Q21;
            Q21=makeQuery(id+"F2.opExtrude","SWEPT_EDGE",EDGE,{"disambiguationData":[OSD([sQuery(id+"F0.wireOp",EDGE,"E7.24.3"),sQuery(id+"F0.wireOp",EDGE,"E11.24.0")])]});
            var Q22;
            Q22=makeQuery(id+"F2.opExtrude","SWEPT_EDGE",EDGE,{"disambiguationData":[OSD([sQuery(id+"F0.wireOp",EDGE,"E2"),sQuery(id+"F0.wireOp",EDGE,"E7.23.3")])]});
            var Q23;
            Q23=makeQuery(id+"F2.opExtrude","SWEPT_EDGE",EDGE,{"disambiguationData":[OSD([sQuery(id+"F0.wireOp",EDGE,"E7.23.3"),sQuery(id+"F0.wireOp",EDGE,"E11.23.0")])]});
            var Q24;
            Q24=makeQuery(id+"F2.opExtrude","SWEPT_EDGE",EDGE,{"disambiguationData":[OSD([sQuery(id+"F0.wireOp",EDGE,"E2"),sQuery(id+"F0.wireOp",EDGE,"E7.22.3")])]});
            var Q25;
            Q25=makeQuery(id+"F2.opExtrude","SWEPT_EDGE",EDGE,{"disambiguationData":[OSD([sQuery(id+"F0.wireOp",EDGE,"E7.22.3"),sQuery(id+"F0.wireOp",EDGE,"E11.22.0")])]});
            var Q26;
            Q26=makeQuery(id+"F2.opExtrude","SWEPT_EDGE",EDGE,{"disambiguationData":[OSD([sQuery(id+"F0.wireOp",EDGE,"E2"),sQuery(id+"F0.wireOp",EDGE,"E7.6.3")])]});
            var Q27;
            Q27=makeQuery(id+"F2.opExtrude","SWEPT_EDGE",EDGE,{"disambiguationData":[OSD([sQuery(id+"F0.wireOp",EDGE,"E7.6.3"),sQuery(id+"F0.wireOp",EDGE,"E11.6.0")])]});
            var Q28;
            Q28=makeQuery(id+"F2.opExtrude","SWEPT_EDGE",EDGE,{"disambiguationData":[OSD([sQuery(id+"F0.wireOp",EDGE,"E2"),sQuery(id+"F0.wireOp",EDGE,"E7.7.3")])]});
            var Q29;
            Q29=makeQuery(id+"F2.opExtrude","SWEPT_EDGE",EDGE,{"disambiguationData":[OSD([sQuery(id+"F0.wireOp",EDGE,"E7.7.3"),sQuery(id+"F0.wireOp",EDGE,"E11.7.0")])]});
            var Q30;
            Q30=makeQuery(id+"F2.opExtrude","SWEPT_EDGE",EDGE,{"disambiguationData":[OSD([sQuery(id+"F0.wireOp",EDGE,"E2"),sQuery(id+"F0.wireOp",EDGE,"E7.8.3")])]});
            var Q31;
            Q31=makeQuery(id+"F2.opExtrude","SWEPT_EDGE",EDGE,{"disambiguationData":[OSD([sQuery(id+"F0.wireOp",EDGE,"E7.8.3"),sQuery(id+"F0.wireOp",EDGE,"E11.8.0")])]});
            var Q32;
            Q32=makeQuery(id+"F2.opExtrude","SWEPT_EDGE",EDGE,{"disambiguationData":[OSD([sQuery(id+"F0.wireOp",EDGE,"E2"),sQuery(id+"F0.wireOp",EDGE,"E7.9.3")])]});
            var Q33;
            Q33=makeQuery(id+"F2.opExtrude","SWEPT_EDGE",EDGE,{"disambiguationData":[OSD([sQuery(id+"F0.wireOp",EDGE,"E7.9.3"),sQuery(id+"F0.wireOp",EDGE,"E11.9.0")])]});
            var Q34;
            Q34=makeQuery(id+"F2.opExtrude","SWEPT_EDGE",EDGE,{"disambiguationData":[OSD([sQuery(id+"F0.wireOp",EDGE,"E2"),sQuery(id+"F0.wireOp",EDGE,"E7.10.3")])]});
            var Q35;
            Q35=makeQuery(id+"F2.opExtrude","SWEPT_EDGE",EDGE,{"disambiguationData":[OSD([sQuery(id+"F0.wireOp",EDGE,"E7.10.3"),sQuery(id+"F0.wireOp",EDGE,"E11.10.0")])]});
            var Q36;
            Q36=makeQuery(id+"F2.opExtrude","SWEPT_EDGE",EDGE,{"disambiguationData":[OSD([sQuery(id+"F0.wireOp",EDGE,"E2"),sQuery(id+"F0.wireOp",EDGE,"E7.11.3")])]});
            var Q37;
            Q37=makeQuery(id+"F2.opExtrude","SWEPT_EDGE",EDGE,{"disambiguationData":[OSD([sQuery(id+"F0.wireOp",EDGE,"E7.11.3"),sQuery(id+"F0.wireOp",EDGE,"E11.11.0")])]});
            var Q38;
            Q38=makeQuery(id+"F2.opExtrude","SWEPT_EDGE",EDGE,{"disambiguationData":[OSD([sQuery(id+"F0.wireOp",EDGE,"E2"),sQuery(id+"F0.wireOp",EDGE,"E7.12.3")])]});
            var Q39;
            Q39=makeQuery(id+"F2.opExtrude","SWEPT_EDGE",EDGE,{"disambiguationData":[OSD([sQuery(id+"F0.wireOp",EDGE,"E7.12.3"),sQuery(id+"F0.wireOp",EDGE,"E11.12.0")])]});
            var Q40;
            Q40=makeQuery(id+"F2.opExtrude","SWEPT_EDGE",EDGE,{"disambiguationData":[OSD([sQuery(id+"F0.wireOp",EDGE,"E2"),sQuery(id+"F0.wireOp",EDGE,"E7.13.3")])]});
            var Q41;
            Q41=makeQuery(id+"F2.opExtrude","SWEPT_EDGE",EDGE,{"disambiguationData":[OSD([sQuery(id+"F0.wireOp",EDGE,"E7.13.3"),sQuery(id+"F0.wireOp",EDGE,"E11.13.0")])]});
            var Q42;
            Q42=makeQuery(id+"F2.opExtrude","SWEPT_EDGE",EDGE,{"disambiguationData":[OSD([sQuery(id+"F0.wireOp",EDGE,"E2"),sQuery(id+"F0.wireOp",EDGE,"E7.14.3")])]});
            var Q43;
            Q43=makeQuery(id+"F2.opExtrude","SWEPT_EDGE",EDGE,{"disambiguationData":[OSD([sQuery(id+"F0.wireOp",EDGE,"E7.14.3"),sQuery(id+"F0.wireOp",EDGE,"E11.14.0")])]});
            var Q44;
            Q44=makeQuery(id+"F2.opExtrude","SWEPT_EDGE",EDGE,{"disambiguationData":[OSD([sQuery(id+"F0.wireOp",EDGE,"E2"),sQuery(id+"F0.wireOp",EDGE,"E7.15.3")])]});
            var Q45;
            Q45=makeQuery(id+"F2.opExtrude","SWEPT_EDGE",EDGE,{"disambiguationData":[OSD([sQuery(id+"F0.wireOp",EDGE,"E7.15.3"),sQuery(id+"F0.wireOp",EDGE,"E11.15.0")])]});
            var Q46;
            Q46=makeQuery(id+"F2.opExtrude","SWEPT_EDGE",EDGE,{"disambiguationData":[OSD([sQuery(id+"F0.wireOp",EDGE,"E2"),sQuery(id+"F0.wireOp",EDGE,"E7.16.3")])]});
            var Q47;
            Q47=makeQuery(id+"F2.opExtrude","SWEPT_EDGE",EDGE,{"disambiguationData":[OSD([sQuery(id+"F0.wireOp",EDGE,"E7.16.3"),sQuery(id+"F0.wireOp",EDGE,"E11.16.0")])]});
            var Q48;
            Q48=makeQuery(id+"F2.opExtrude","SWEPT_EDGE",EDGE,{"disambiguationData":[OSD([sQuery(id+"F0.wireOp",EDGE,"E2"),sQuery(id+"F0.wireOp",EDGE,"E7.17.3")])]});
            var Q49;
            Q49=makeQuery(id+"F2.opExtrude","SWEPT_EDGE",EDGE,{"disambiguationData":[OSD([sQuery(id+"F0.wireOp",EDGE,"E7.17.3"),sQuery(id+"F0.wireOp",EDGE,"E11.17.0")])]});
            var Q50;
            Q50=makeQuery(id+"F2.opExtrude","SWEPT_EDGE",EDGE,{"disambiguationData":[OSD([sQuery(id+"F0.wireOp",EDGE,"E2"),sQuery(id+"F0.wireOp",EDGE,"E7.18.3")])]});
            var Q51;
            Q51=makeQuery(id+"F2.opExtrude","SWEPT_EDGE",EDGE,{"disambiguationData":[OSD([sQuery(id+"F0.wireOp",EDGE,"E7.18.3"),sQuery(id+"F0.wireOp",EDGE,"E11.18.0")])]});
            var Q52;
            Q52=makeQuery(id+"F2.opExtrude","SWEPT_EDGE",EDGE,{"disambiguationData":[OSD([sQuery(id+"F0.wireOp",EDGE,"E2"),sQuery(id+"F0.wireOp",EDGE,"E7.19.3")])]});
            var Q53;
            Q53=makeQuery(id+"F2.opExtrude","SWEPT_EDGE",EDGE,{"disambiguationData":[OSD([sQuery(id+"F0.wireOp",EDGE,"E7.19.3"),sQuery(id+"F0.wireOp",EDGE,"E11.19.0")])]});
            var Q54;
            Q54=makeQuery(id+"F2.opExtrude","SWEPT_EDGE",EDGE,{"disambiguationData":[OSD([sQuery(id+"F0.wireOp",EDGE,"E2"),sQuery(id+"F0.wireOp",EDGE,"E7.20.3")])]});
            var Q55;
            Q55=makeQuery(id+"F2.opExtrude","SWEPT_EDGE",EDGE,{"disambiguationData":[OSD([sQuery(id+"F0.wireOp",EDGE,"E7.20.3"),sQuery(id+"F0.wireOp",EDGE,"E11.20.0")])]});
            var Q56;
            Q56=makeQuery(id+"F2.opExtrude","SWEPT_EDGE",EDGE,{"disambiguationData":[OSD([sQuery(id+"F0.wireOp",EDGE,"E2"),sQuery(id+"F0.wireOp",EDGE,"E7.21.3")])]});
            var Q57;
            Q57=makeQuery(id+"F2.opExtrude","SWEPT_EDGE",EDGE,{"disambiguationData":[OSD([sQuery(id+"F0.wireOp",EDGE,"E7.21.3"),sQuery(id+"F0.wireOp",EDGE,"E11.21.0")])]});
            var Q58;
            Q58=makeQuery(id+"F2.opExtrude","SWEPT_EDGE",EDGE,{"disambiguationData":[OSD([sQuery(id+"F0.wireOp",EDGE,"E9"),sQuery(id+"F0.wireOp",EDGE,"E12")])]});
            fillet(context, id + "F8", {"entities" : qUnion([Q0, Q1, Q2, Q3, Q4, Q5, Q6, Q7, Q8, Q9, Q10, Q11, Q12, Q13, Q14, Q15, Q16, Q17, Q18, Q19, Q20, Q21, Q22, Q23, Q24, Q25, Q26, Q27, Q28, Q29, Q30, Q31, Q32, Q33, Q34, Q35, Q36, Q37, Q38, Q39, Q40, Q41, Q42, Q43, Q44, Q45, Q46, Q47, Q48, Q49, Q50, Q51, Q52, Q53, Q54, Q55, Q56, Q57, Q58]), "radius" : 0.64 * mm, "tangentPropagation" : true, "allowEdgeOverflow" : false});
        }
        {
            var Q0;
            Q0=makeQuery(id+"F4.opPattern","COPY",EDGE,{"derivedFrom":makeQuery(id+"F2.opExtrude","SWEPT_EDGE",EDGE,{"disambiguationData":[OSD([sQuery(id+"F0.wireOp",EDGE,"E2"),sQuery(id+"F0.wireOp",EDGE,"E7.1.3")])]}),"instanceName":"1"});
            var Q1;
            Q1=makeQuery(id+"F4.opPattern","COPY",EDGE,{"derivedFrom":makeQuery(id+"F2.opExtrude","SWEPT_EDGE",EDGE,{"disambiguationData":[OSD([sQuery(id+"F0.wireOp",EDGE,"E2"),sQuery(id+"F0.wireOp",EDGE,"E6")])]}),"instanceName":"1"});
            var Q2;
            Q2=makeQuery(id+"F4.opPattern","COPY",EDGE,{"derivedFrom":makeQuery(id+"F2.opExtrude","SWEPT_EDGE",EDGE,{"disambiguationData":[OSD([sQuery(id+"F0.wireOp",EDGE,"E2"),sQuery(id+"F0.wireOp",EDGE,"E7.14.0")])]}),"instanceName":"1"});
            var Q3;
            Q3=makeQuery(id+"F4.opPattern","COPY",EDGE,{"derivedFrom":makeQuery(id+"F2.opExtrude","SWEPT_EDGE",EDGE,{"disambiguationData":[OSD([sQuery(id+"F0.wireOp",EDGE,"E2"),sQuery(id+"F0.wireOp",EDGE,"E7.15.3")])]}),"instanceName":"1"});
            var Q4;
            Q4=makeQuery(id+"F4.opPattern","COPY",EDGE,{"derivedFrom":makeQuery(id+"F2.opExtrude","SWEPT_EDGE",EDGE,{"disambiguationData":[OSD([sQuery(id+"F0.wireOp",EDGE,"E2"),sQuery(id+"F0.wireOp",EDGE,"E7.16.3")])]}),"instanceName":"1"});
            var Q5;
            Q5=makeQuery(id+"F4.opPattern","COPY",EDGE,{"derivedFrom":makeQuery(id+"F2.opExtrude","SWEPT_EDGE",EDGE,{"disambiguationData":[OSD([sQuery(id+"F0.wireOp",EDGE,"E2"),sQuery(id+"F0.wireOp",EDGE,"E7.15.0")])]}),"instanceName":"1"});
            var Q6;
            Q6=makeQuery(id+"F4.opPattern","COPY",EDGE,{"derivedFrom":makeQuery(id+"F2.opExtrude","SWEPT_EDGE",EDGE,{"disambiguationData":[OSD([sQuery(id+"F0.wireOp",EDGE,"E2"),sQuery(id+"F0.wireOp",EDGE,"E7.14.3")])]}),"instanceName":"1"});
            var Q7;
            Q7=makeQuery(id+"F4.opPattern","COPY",EDGE,{"derivedFrom":makeQuery(id+"F2.opExtrude","SWEPT_EDGE",EDGE,{"disambiguationData":[OSD([sQuery(id+"F0.wireOp",EDGE,"E2"),sQuery(id+"F0.wireOp",EDGE,"E7.13.0")])]}),"instanceName":"1"});
            var Q8;
            Q8=makeQuery(id+"F4.opPattern","COPY",EDGE,{"derivedFrom":makeQuery(id+"F2.opExtrude","SWEPT_EDGE",EDGE,{"disambiguationData":[OSD([sQuery(id+"F0.wireOp",EDGE,"E2"),sQuery(id+"F0.wireOp",EDGE,"E7.16.0")])]}),"instanceName":"1"});
            var Q9;
            Q9=makeQuery(id+"F4.opPattern","COPY",EDGE,{"derivedFrom":makeQuery(id+"F2.opExtrude","SWEPT_EDGE",EDGE,{"disambiguationData":[OSD([sQuery(id+"F0.wireOp",EDGE,"E2"),sQuery(id+"F0.wireOp",EDGE,"E7.17.3")])]}),"instanceName":"1"});
            var Q10;
            Q10=makeQuery(id+"F2.opExtrude","SWEPT_EDGE",EDGE,{"disambiguationData":[OSD([sQuery(id+"F0.wireOp",EDGE,"E2"),sQuery(id+"F0.wireOp",EDGE,"E7.2.3")])]});
            var Q11;
            Q11=makeQuery(id+"F2.opExtrude","SWEPT_EDGE",EDGE,{"disambiguationData":[OSD([sQuery(id+"F0.wireOp",EDGE,"E2"),sQuery(id+"F0.wireOp",EDGE,"E7.1.0")])]});
            var Q12;
            Q12=makeQuery(id+"F2.opExtrude","SWEPT_EDGE",EDGE,{"disambiguationData":[OSD([sQuery(id+"F0.wireOp",EDGE,"E2"),sQuery(id+"F0.wireOp",EDGE,"E6")])]});
            var Q13;
            Q13=makeQuery(id+"F2.opExtrude","SWEPT_EDGE",EDGE,{"disambiguationData":[OSD([sQuery(id+"F0.wireOp",EDGE,"E2"),sQuery(id+"F0.wireOp",EDGE,"E7.1.3")])]});
            var Q14;
            Q14=makeQuery(id+"F2.opExtrude","SWEPT_EDGE",EDGE,{"disambiguationData":[OSD([sQuery(id+"F0.wireOp",EDGE,"E2"),sQuery(id+"F0.wireOp",EDGE,"E5")])]});
            var Q15;
            Q15=makeQuery(id+"F2.opExtrude","SWEPT_EDGE",EDGE,{"disambiguationData":[OSD([sQuery(id+"F0.wireOp",EDGE,"E2"),sQuery(id+"F0.wireOp",EDGE,"E7.29.0")])]});
            var Q16;
            Q16=makeQuery(id+"F2.opExtrude","SWEPT_EDGE",EDGE,{"disambiguationData":[OSD([sQuery(id+"F0.wireOp",EDGE,"E2"),sQuery(id+"F0.wireOp",EDGE,"E7.29.3")])]});
            var Q17;
            Q17=makeQuery(id+"F2.opExtrude","SWEPT_EDGE",EDGE,{"disambiguationData":[OSD([sQuery(id+"F0.wireOp",EDGE,"E2"),sQuery(id+"F0.wireOp",EDGE,"E7.28.0")])]});
            var Q18;
            Q18=makeQuery(id+"F2.opExtrude","SWEPT_EDGE",EDGE,{"disambiguationData":[OSD([sQuery(id+"F0.wireOp",EDGE,"E2"),sQuery(id+"F0.wireOp",EDGE,"E7.26.0")])]});
            var Q19;
            Q19=makeQuery(id+"F2.opExtrude","SWEPT_EDGE",EDGE,{"disambiguationData":[OSD([sQuery(id+"F0.wireOp",EDGE,"E2"),sQuery(id+"F0.wireOp",EDGE,"E7.25.0")])]});
            var Q20;
            Q20=makeQuery(id+"F2.opExtrude","SWEPT_EDGE",EDGE,{"disambiguationData":[OSD([sQuery(id+"F0.wireOp",EDGE,"E2"),sQuery(id+"F0.wireOp",EDGE,"E7.27.0")])]});
            var Q21;
            Q21=makeQuery(id+"F2.opExtrude","SWEPT_EDGE",EDGE,{"disambiguationData":[OSD([sQuery(id+"F0.wireOp",EDGE,"E2"),sQuery(id+"F0.wireOp",EDGE,"E7.24.0")])]});
            var Q22;
            Q22=makeQuery(id+"F2.opExtrude","SWEPT_EDGE",EDGE,{"disambiguationData":[OSD([sQuery(id+"F0.wireOp",EDGE,"E2"),sQuery(id+"F0.wireOp",EDGE,"E7.23.0")])]});
            var Q23;
            Q23=makeQuery(id+"F2.opExtrude","SWEPT_EDGE",EDGE,{"disambiguationData":[OSD([sQuery(id+"F0.wireOp",EDGE,"E2"),sQuery(id+"F0.wireOp",EDGE,"E7.22.0")])]});
            var Q24;
            Q24=makeQuery(id+"F2.opExtrude","SWEPT_EDGE",EDGE,{"disambiguationData":[OSD([sQuery(id+"F0.wireOp",EDGE,"E2"),sQuery(id+"F0.wireOp",EDGE,"E7.21.0")])]});
            var Q25;
            Q25=makeQuery(id+"F2.opExtrude","SWEPT_EDGE",EDGE,{"disambiguationData":[OSD([sQuery(id+"F0.wireOp",EDGE,"E2"),sQuery(id+"F0.wireOp",EDGE,"E7.20.0")])]});
            var Q26;
            Q26=makeQuery(id+"F2.opExtrude","SWEPT_EDGE",EDGE,{"disambiguationData":[OSD([sQuery(id+"F0.wireOp",EDGE,"E2"),sQuery(id+"F0.wireOp",EDGE,"E7.19.0")])]});
            var Q27;
            Q27=makeQuery(id+"F2.opExtrude","SWEPT_EDGE",EDGE,{"disambiguationData":[OSD([sQuery(id+"F0.wireOp",EDGE,"E2"),sQuery(id+"F0.wireOp",EDGE,"E7.18.0")])]});
            var Q28;
            Q28=makeQuery(id+"F2.opExtrude","SWEPT_EDGE",EDGE,{"disambiguationData":[OSD([sQuery(id+"F0.wireOp",EDGE,"E2"),sQuery(id+"F0.wireOp",EDGE,"E7.17.0")])]});
            var Q29;
            Q29=makeQuery(id+"F2.opExtrude","SWEPT_EDGE",EDGE,{"disambiguationData":[OSD([sQuery(id+"F0.wireOp",EDGE,"E2"),sQuery(id+"F0.wireOp",EDGE,"E7.16.0")])]});
            var Q30;
            Q30=makeQuery(id+"F2.opExtrude","SWEPT_EDGE",EDGE,{"disambiguationData":[OSD([sQuery(id+"F0.wireOp",EDGE,"E2"),sQuery(id+"F0.wireOp",EDGE,"E7.15.0")])]});
            var Q31;
            Q31=makeQuery(id+"F2.opExtrude","SWEPT_EDGE",EDGE,{"disambiguationData":[OSD([sQuery(id+"F0.wireOp",EDGE,"E2"),sQuery(id+"F0.wireOp",EDGE,"E7.14.0")])]});
            var Q32;
            Q32=makeQuery(id+"F2.opExtrude","SWEPT_EDGE",EDGE,{"disambiguationData":[OSD([sQuery(id+"F0.wireOp",EDGE,"E2"),sQuery(id+"F0.wireOp",EDGE,"E7.13.0")])]});
            var Q33;
            Q33=makeQuery(id+"F2.opExtrude","SWEPT_EDGE",EDGE,{"disambiguationData":[OSD([sQuery(id+"F0.wireOp",EDGE,"E2"),sQuery(id+"F0.wireOp",EDGE,"E7.12.0")])]});
            var Q34;
            Q34=makeQuery(id+"F2.opExtrude","SWEPT_EDGE",EDGE,{"disambiguationData":[OSD([sQuery(id+"F0.wireOp",EDGE,"E2"),sQuery(id+"F0.wireOp",EDGE,"E7.11.0")])]});
            var Q35;
            Q35=makeQuery(id+"F2.opExtrude","SWEPT_EDGE",EDGE,{"disambiguationData":[OSD([sQuery(id+"F0.wireOp",EDGE,"E2"),sQuery(id+"F0.wireOp",EDGE,"E7.10.0")])]});
            var Q36;
            Q36=makeQuery(id+"F2.opExtrude","SWEPT_EDGE",EDGE,{"disambiguationData":[OSD([sQuery(id+"F0.wireOp",EDGE,"E2"),sQuery(id+"F0.wireOp",EDGE,"E7.9.0")])]});
            var Q37;
            Q37=makeQuery(id+"F2.opExtrude","SWEPT_EDGE",EDGE,{"disambiguationData":[OSD([sQuery(id+"F0.wireOp",EDGE,"E2"),sQuery(id+"F0.wireOp",EDGE,"E7.8.0")])]});
            var Q38;
            Q38=makeQuery(id+"F2.opExtrude","SWEPT_EDGE",EDGE,{"disambiguationData":[OSD([sQuery(id+"F0.wireOp",EDGE,"E2"),sQuery(id+"F0.wireOp",EDGE,"E7.7.0")])]});
            var Q39;
            Q39=makeQuery(id+"F2.opExtrude","SWEPT_EDGE",EDGE,{"disambiguationData":[OSD([sQuery(id+"F0.wireOp",EDGE,"E2"),sQuery(id+"F0.wireOp",EDGE,"E7.6.0")])]});
            var Q40;
            Q40=makeQuery(id+"F2.opExtrude","SWEPT_EDGE",EDGE,{"disambiguationData":[OSD([sQuery(id+"F0.wireOp",EDGE,"E2"),sQuery(id+"F0.wireOp",EDGE,"E7.5.0")])]});
            var Q41;
            Q41=makeQuery(id+"F2.opExtrude","SWEPT_EDGE",EDGE,{"disambiguationData":[OSD([sQuery(id+"F0.wireOp",EDGE,"E2"),sQuery(id+"F0.wireOp",EDGE,"E7.4.0")])]});
            var Q42;
            Q42=makeQuery(id+"F2.opExtrude","SWEPT_EDGE",EDGE,{"disambiguationData":[OSD([sQuery(id+"F0.wireOp",EDGE,"E2"),sQuery(id+"F0.wireOp",EDGE,"E7.3.0")])]});
            var Q43;
            Q43=makeQuery(id+"F2.opExtrude","SWEPT_EDGE",EDGE,{"disambiguationData":[OSD([sQuery(id+"F0.wireOp",EDGE,"E2"),sQuery(id+"F0.wireOp",EDGE,"E7.2.0")])]});
            var Q44;
            Q44=makeQuery(id+"F4.opPattern","COPY",EDGE,{"derivedFrom":makeQuery(id+"F2.opExtrude","SWEPT_EDGE",EDGE,{"disambiguationData":[OSD([sQuery(id+"F0.wireOp",EDGE,"E2"),sQuery(id+"F0.wireOp",EDGE,"E7.29.0")])]}),"instanceName":"1"});
            var Q45;
            Q45=makeQuery(id+"F4.opPattern","COPY",EDGE,{"derivedFrom":makeQuery(id+"F2.opExtrude","SWEPT_EDGE",EDGE,{"disambiguationData":[OSD([sQuery(id+"F0.wireOp",EDGE,"E2"),sQuery(id+"F0.wireOp",EDGE,"E7.28.0")])]}),"instanceName":"1"});
            var Q46;
            Q46=makeQuery(id+"F4.opPattern","COPY",EDGE,{"derivedFrom":makeQuery(id+"F2.opExtrude","SWEPT_EDGE",EDGE,{"disambiguationData":[OSD([sQuery(id+"F0.wireOp",EDGE,"E2"),sQuery(id+"F0.wireOp",EDGE,"E7.27.0")])]}),"instanceName":"1"});
            var Q47;
            Q47=makeQuery(id+"F4.opPattern","COPY",EDGE,{"derivedFrom":makeQuery(id+"F2.opExtrude","SWEPT_EDGE",EDGE,{"disambiguationData":[OSD([sQuery(id+"F0.wireOp",EDGE,"E2"),sQuery(id+"F0.wireOp",EDGE,"E7.26.0")])]}),"instanceName":"1"});
            var Q48;
            Q48=makeQuery(id+"F4.opPattern","COPY",EDGE,{"derivedFrom":makeQuery(id+"F2.opExtrude","SWEPT_EDGE",EDGE,{"disambiguationData":[OSD([sQuery(id+"F0.wireOp",EDGE,"E2"),sQuery(id+"F0.wireOp",EDGE,"E7.25.0")])]}),"instanceName":"1"});
            var Q49;
            Q49=makeQuery(id+"F4.opPattern","COPY",EDGE,{"derivedFrom":makeQuery(id+"F2.opExtrude","SWEPT_EDGE",EDGE,{"disambiguationData":[OSD([sQuery(id+"F0.wireOp",EDGE,"E2"),sQuery(id+"F0.wireOp",EDGE,"E7.24.0")])]}),"instanceName":"1"});
            var Q50;
            Q50=makeQuery(id+"F4.opPattern","COPY",EDGE,{"derivedFrom":makeQuery(id+"F2.opExtrude","SWEPT_EDGE",EDGE,{"disambiguationData":[OSD([sQuery(id+"F0.wireOp",EDGE,"E2"),sQuery(id+"F0.wireOp",EDGE,"E7.23.0")])]}),"instanceName":"1"});
            var Q51;
            Q51=makeQuery(id+"F4.opPattern","COPY",EDGE,{"derivedFrom":makeQuery(id+"F2.opExtrude","SWEPT_EDGE",EDGE,{"disambiguationData":[OSD([sQuery(id+"F0.wireOp",EDGE,"E2"),sQuery(id+"F0.wireOp",EDGE,"E7.22.0")])]}),"instanceName":"1"});
            var Q52;
            Q52=makeQuery(id+"F4.opPattern","COPY",EDGE,{"derivedFrom":makeQuery(id+"F2.opExtrude","SWEPT_EDGE",EDGE,{"disambiguationData":[OSD([sQuery(id+"F0.wireOp",EDGE,"E2"),sQuery(id+"F0.wireOp",EDGE,"E7.21.0")])]}),"instanceName":"1"});
            var Q53;
            Q53=makeQuery(id+"F4.opPattern","COPY",EDGE,{"derivedFrom":makeQuery(id+"F2.opExtrude","SWEPT_EDGE",EDGE,{"disambiguationData":[OSD([sQuery(id+"F0.wireOp",EDGE,"E2"),sQuery(id+"F0.wireOp",EDGE,"E7.20.0")])]}),"instanceName":"1"});
            var Q54;
            Q54=makeQuery(id+"F4.opPattern","COPY",EDGE,{"derivedFrom":makeQuery(id+"F2.opExtrude","SWEPT_EDGE",EDGE,{"disambiguationData":[OSD([sQuery(id+"F0.wireOp",EDGE,"E2"),sQuery(id+"F0.wireOp",EDGE,"E7.1.0")])]}),"instanceName":"1"});
            var Q55;
            Q55=makeQuery(id+"F4.opPattern","COPY",EDGE,{"derivedFrom":makeQuery(id+"F2.opExtrude","SWEPT_EDGE",EDGE,{"disambiguationData":[OSD([sQuery(id+"F0.wireOp",EDGE,"E2"),sQuery(id+"F0.wireOp",EDGE,"E7.2.0")])]}),"instanceName":"1"});
            var Q56;
            Q56=makeQuery(id+"F4.opPattern","COPY",EDGE,{"derivedFrom":makeQuery(id+"F2.opExtrude","SWEPT_EDGE",EDGE,{"disambiguationData":[OSD([sQuery(id+"F0.wireOp",EDGE,"E2"),sQuery(id+"F0.wireOp",EDGE,"E7.3.0")])]}),"instanceName":"1"});
            var Q57;
            Q57=makeQuery(id+"F4.opPattern","COPY",EDGE,{"derivedFrom":makeQuery(id+"F2.opExtrude","SWEPT_EDGE",EDGE,{"disambiguationData":[OSD([sQuery(id+"F0.wireOp",EDGE,"E2"),sQuery(id+"F0.wireOp",EDGE,"E7.4.0")])]}),"instanceName":"1"});
            var Q58;
            Q58=makeQuery(id+"F4.opPattern","COPY",EDGE,{"derivedFrom":makeQuery(id+"F2.opExtrude","SWEPT_EDGE",EDGE,{"disambiguationData":[OSD([sQuery(id+"F0.wireOp",EDGE,"E2"),sQuery(id+"F0.wireOp",EDGE,"E7.5.0")])]}),"instanceName":"1"});
            var Q59;
            Q59=makeQuery(id+"F4.opPattern","COPY",EDGE,{"derivedFrom":makeQuery(id+"F2.opExtrude","SWEPT_EDGE",EDGE,{"disambiguationData":[OSD([sQuery(id+"F0.wireOp",EDGE,"E2"),sQuery(id+"F0.wireOp",EDGE,"E7.6.0")])]}),"instanceName":"1"});
            var Q60;
            Q60=makeQuery(id+"F4.opPattern","COPY",EDGE,{"derivedFrom":makeQuery(id+"F2.opExtrude","SWEPT_EDGE",EDGE,{"disambiguationData":[OSD([sQuery(id+"F0.wireOp",EDGE,"E2"),sQuery(id+"F0.wireOp",EDGE,"E7.7.0")])]}),"instanceName":"1"});
            var Q61;
            Q61=makeQuery(id+"F4.opPattern","COPY",EDGE,{"derivedFrom":makeQuery(id+"F2.opExtrude","SWEPT_EDGE",EDGE,{"disambiguationData":[OSD([sQuery(id+"F0.wireOp",EDGE,"E2"),sQuery(id+"F0.wireOp",EDGE,"E7.8.0")])]}),"instanceName":"1"});
            var Q62;
            Q62=makeQuery(id+"F4.opPattern","COPY",EDGE,{"derivedFrom":makeQuery(id+"F2.opExtrude","SWEPT_EDGE",EDGE,{"disambiguationData":[OSD([sQuery(id+"F0.wireOp",EDGE,"E2"),sQuery(id+"F0.wireOp",EDGE,"E7.9.0")])]}),"instanceName":"1"});
            var Q63;
            Q63=makeQuery(id+"F4.opPattern","COPY",EDGE,{"derivedFrom":makeQuery(id+"F2.opExtrude","SWEPT_EDGE",EDGE,{"disambiguationData":[OSD([sQuery(id+"F0.wireOp",EDGE,"E2"),sQuery(id+"F0.wireOp",EDGE,"E7.10.0")])]}),"instanceName":"1"});
            var Q64;
            Q64=makeQuery(id+"F4.opPattern","COPY",EDGE,{"derivedFrom":makeQuery(id+"F2.opExtrude","SWEPT_EDGE",EDGE,{"disambiguationData":[OSD([sQuery(id+"F0.wireOp",EDGE,"E2"),sQuery(id+"F0.wireOp",EDGE,"E7.11.0")])]}),"instanceName":"1"});
            var Q65;
            Q65=makeQuery(id+"F4.opPattern","COPY",EDGE,{"derivedFrom":makeQuery(id+"F2.opExtrude","SWEPT_EDGE",EDGE,{"disambiguationData":[OSD([sQuery(id+"F0.wireOp",EDGE,"E2"),sQuery(id+"F0.wireOp",EDGE,"E7.12.0")])]}),"instanceName":"1"});
            var Q66;
            Q66=makeQuery(id+"F4.opPattern","COPY",EDGE,{"derivedFrom":makeQuery(id+"F2.opExtrude","SWEPT_EDGE",EDGE,{"disambiguationData":[OSD([sQuery(id+"F0.wireOp",EDGE,"E2"),sQuery(id+"F0.wireOp",EDGE,"E7.17.0")])]}),"instanceName":"1"});
            var Q67;
            Q67=makeQuery(id+"F4.opPattern","COPY",EDGE,{"derivedFrom":makeQuery(id+"F2.opExtrude","SWEPT_EDGE",EDGE,{"disambiguationData":[OSD([sQuery(id+"F0.wireOp",EDGE,"E2"),sQuery(id+"F0.wireOp",EDGE,"E7.18.0")])]}),"instanceName":"1"});
            var Q68;
            Q68=makeQuery(id+"F4.opPattern","COPY",EDGE,{"derivedFrom":makeQuery(id+"F2.opExtrude","SWEPT_EDGE",EDGE,{"disambiguationData":[OSD([sQuery(id+"F0.wireOp",EDGE,"E2"),sQuery(id+"F0.wireOp",EDGE,"E7.19.0")])]}),"instanceName":"1"});
            fillet(context, id + "F9", {"entities" : qUnion([Q0, Q1, Q2, Q3, Q4, Q5, Q6, Q7, Q8, Q9, Q10, Q11, Q12, Q13, Q14, Q15, Q16, Q17, Q18, Q19, Q20, Q21, Q22, Q23, Q24, Q25, Q26, Q27, Q28, Q29, Q30, Q31, Q32, Q33, Q34, Q35, Q36, Q37, Q38, Q39, Q40, Q41, Q42, Q43, Q44, Q45, Q46, Q47, Q48, Q49, Q50, Q51, Q52, Q53, Q54, Q55, Q56, Q57, Q58, Q59, Q60, Q61, Q62, Q63, Q64, Q65, Q66, Q67, Q68]), "radius" : 0.66 * mm, "tangentPropagation" : true, "allowEdgeOverflow" : false});
        }
        {
            var Q0;
            Q0=makeQuery(id+"F2.opExtrude","SWEPT_EDGE",EDGE,{"disambiguationData":[OSD([sQuery(id+"F0.wireOp",EDGE,"E5"),sQuery(id+"F0.wireOp",EDGE,"Irwjhcbc-hKIq-O0h8-zOLC-YVmx8JeJbAoH"),sQuery(id+"F0.wireOp",EDGE,"20ElE90X-Kxff-hiRp-fycd-sdGsmNjob2QY")])]});
            fillet(context, id + "F10", {"entities" : qUnion([Q0]), "radius" : 0.64 * mm, "tangentPropagation" : true, "allowEdgeOverflow" : false});
        }
        {
            var Q0;
            Q0=makeQuery(id+"F2.opExtrude","SWEPT_BODY",BODY,{"disambiguationData":[OSD([sQuery(id+"F0.wireOp",EDGE,"E0"),sQuery(id+"F0.wireOp",EDGE,"E2"),sQuery(id+"F0.wireOp",EDGE,"E4"),sQuery(id+"F0.wireOp",EDGE,"E5"),sQuery(id+"F0.wireOp",EDGE,"E6"),sQuery(id+"F0.wireOp",EDGE,"E7.1.0"),sQuery(id+"F0.wireOp",EDGE,"E7.1.1"),sQuery(id+"F0.wireOp",EDGE,"E7.1.3"),sQuery(id+"F0.wireOp",EDGE,"E7.2.0"),sQuery(id+"F0.wireOp",EDGE,"E7.2.1"),sQuery(id+"F0.wireOp",EDGE,"E7.2.3"),sQuery(id+"F0.wireOp",EDGE,"E7.3.0"),sQuery(id+"F0.wireOp",EDGE,"E7.3.1"),sQuery(id+"F0.wireOp",EDGE,"E7.3.3"),sQuery(id+"F0.wireOp",EDGE,"E7.4.0"),sQuery(id+"F0.wireOp",EDGE,"E7.4.1"),sQuery(id+"F0.wireOp",EDGE,"E7.4.3"),sQuery(id+"F0.wireOp",EDGE,"E7.5.0"),sQuery(id+"F0.wireOp",EDGE,"E7.5.1"),sQuery(id+"F0.wireOp",EDGE,"E7.5.3"),sQuery(id+"F0.wireOp",EDGE,"E7.6.0"),sQuery(id+"F0.wireOp",EDGE,"E7.6.1"),sQuery(id+"F0.wireOp",EDGE,"E7.6.3"),sQuery(id+"F0.wireOp",EDGE,"E7.7.0"),sQuery(id+"F0.wireOp",EDGE,"E7.7.1"),sQuery(id+"F0.wireOp",EDGE,"E7.7.3"),sQuery(id+"F0.wireOp",EDGE,"E7.8.0"),sQuery(id+"F0.wireOp",EDGE,"E7.8.1"),sQuery(id+"F0.wireOp",EDGE,"E7.8.3"),sQuery(id+"F0.wireOp",EDGE,"E7.9.0"),sQuery(id+"F0.wireOp",EDGE,"E7.9.1"),sQuery(id+"F0.wireOp",EDGE,"E7.9.3"),sQuery(id+"F0.wireOp",EDGE,"E7.10.0"),sQuery(id+"F0.wireOp",EDGE,"E7.10.1"),sQuery(id+"F0.wireOp",EDGE,"E7.10.3"),sQuery(id+"F0.wireOp",EDGE,"E7.11.0"),sQuery(id+"F0.wireOp",EDGE,"E7.11.1"),sQuery(id+"F0.wireOp",EDGE,"E7.11.3"),sQuery(id+"F0.wireOp",EDGE,"E7.12.0"),sQuery(id+"F0.wireOp",EDGE,"E7.12.1"),sQuery(id+"F0.wireOp",EDGE,"E7.12.3"),sQuery(id+"F0.wireOp",EDGE,"E7.13.0"),sQuery(id+"F0.wireOp",EDGE,"E7.13.1"),sQuery(id+"F0.wireOp",EDGE,"E7.13.3"),sQuery(id+"F0.wireOp",EDGE,"E7.14.0"),sQuery(id+"F0.wireOp",EDGE,"E7.14.1"),sQuery(id+"F0.wireOp",EDGE,"E7.14.3"),sQuery(id+"F0.wireOp",EDGE,"E7.15.0"),sQuery(id+"F0.wireOp",EDGE,"E7.15.1"),sQuery(id+"F0.wireOp",EDGE,"E7.15.3"),sQuery(id+"F0.wireOp",EDGE,"E7.16.0"),sQuery(id+"F0.wireOp",EDGE,"E7.16.1"),sQuery(id+"F0.wireOp",EDGE,"E7.16.3"),sQuery(id+"F0.wireOp",EDGE,"E7.17.0"),sQuery(id+"F0.wireOp",EDGE,"E7.17.1"),sQuery(id+"F0.wireOp",EDGE,"E7.17.3"),sQuery(id+"F0.wireOp",EDGE,"E7.18.0"),sQuery(id+"F0.wireOp",EDGE,"E7.18.1"),sQuery(id+"F0.wireOp",EDGE,"E7.18.3"),sQuery(id+"F0.wireOp",EDGE,"E7.19.0"),sQuery(id+"F0.wireOp",EDGE,"E7.19.1"),sQuery(id+"F0.wireOp",EDGE,"E7.19.3"),sQuery(id+"F0.wireOp",EDGE,"E7.20.0"),sQuery(id+"F0.wireOp",EDGE,"E7.20.1"),sQuery(id+"F0.wireOp",EDGE,"E7.20.3"),sQuery(id+"F0.wireOp",EDGE,"E7.21.0"),sQuery(id+"F0.wireOp",EDGE,"E7.21.1"),sQuery(id+"F0.wireOp",EDGE,"E7.21.3"),sQuery(id+"F0.wireOp",EDGE,"E7.22.0"),sQuery(id+"F0.wireOp",EDGE,"E7.22.1"),sQuery(id+"F0.wireOp",EDGE,"E7.22.3"),sQuery(id+"F0.wireOp",EDGE,"E7.23.0"),sQuery(id+"F0.wireOp",EDGE,"E7.23.1"),sQuery(id+"F0.wireOp",EDGE,"E7.23.3"),sQuery(id+"F0.wireOp",EDGE,"E7.24.0"),sQuery(id+"F0.wireOp",EDGE,"E7.24.1"),sQuery(id+"F0.wireOp",EDGE,"E7.24.3"),sQuery(id+"F0.wireOp",EDGE,"E7.25.0"),sQuery(id+"F0.wireOp",EDGE,"E7.25.1"),sQuery(id+"F0.wireOp",EDGE,"E7.25.3"),sQuery(id+"F0.wireOp",EDGE,"E7.26.0"),sQuery(id+"F0.wireOp",EDGE,"E7.26.1"),sQuery(id+"F0.wireOp",EDGE,"E7.26.3"),sQuery(id+"F0.wireOp",EDGE,"E7.27.0"),sQuery(id+"F0.wireOp",EDGE,"E7.27.1"),sQuery(id+"F0.wireOp",EDGE,"E7.27.3"),sQuery(id+"F0.wireOp",EDGE,"E7.28.0"),sQuery(id+"F0.wireOp",EDGE,"E7.28.1"),sQuery(id+"F0.wireOp",EDGE,"E7.28.3"),sQuery(id+"F0.wireOp",EDGE,"E7.29.0"),sQuery(id+"F0.wireOp",EDGE,"E7.29.1"),sQuery(id+"F0.wireOp",EDGE,"E7.29.3"),sQuery(id+"F0.wireOp",EDGE,"E8"),sQuery(id+"F0.wireOp",EDGE,"E9"),sQuery(id+"F0.wireOp",EDGE,"E10"),sQuery(id+"F0.wireOp",EDGE,"E11.1.0"),sQuery(id+"F0.wireOp",EDGE,"E11.1.1"),sQuery(id+"F0.wireOp",EDGE,"E11.1.2"),sQuery(id+"F0.wireOp",EDGE,"E11.2.0"),sQuery(id+"F0.wireOp",EDGE,"E11.2.1"),sQuery(id+"F0.wireOp",EDGE,"E11.2.2"),sQuery(id+"F0.wireOp",EDGE,"E11.3.0"),sQuery(id+"F0.wireOp",EDGE,"E11.3.1"),sQuery(id+"F0.wireOp",EDGE,"E11.3.2"),sQuery(id+"F0.wireOp",EDGE,"E11.4.0"),sQuery(id+"F0.wireOp",EDGE,"E11.4.1"),sQuery(id+"F0.wireOp",EDGE,"E11.4.2"),sQuery(id+"F0.wireOp",EDGE,"E11.5.0"),sQuery(id+"F0.wireOp",EDGE,"E11.5.1"),sQuery(id+"F0.wireOp",EDGE,"E11.5.2"),sQuery(id+"F0.wireOp",EDGE,"E11.6.0"),sQuery(id+"F0.wireOp",EDGE,"E11.6.1"),sQuery(id+"F0.wireOp",EDGE,"E11.6.2"),sQuery(id+"F0.wireOp",EDGE,"E11.7.0"),sQuery(id+"F0.wireOp",EDGE,"E11.7.1"),sQuery(id+"F0.wireOp",EDGE,"E11.7.2"),sQuery(id+"F0.wireOp",EDGE,"E11.8.0"),sQuery(id+"F0.wireOp",EDGE,"E11.8.1"),sQuery(id+"F0.wireOp",EDGE,"E11.8.2"),sQuery(id+"F0.wireOp",EDGE,"E11.9.0"),sQuery(id+"F0.wireOp",EDGE,"E11.9.1"),sQuery(id+"F0.wireOp",EDGE,"E11.9.2"),sQuery(id+"F0.wireOp",EDGE,"E11.10.0"),sQuery(id+"F0.wireOp",EDGE,"E11.10.1"),sQuery(id+"F0.wireOp",EDGE,"E11.10.2"),sQuery(id+"F0.wireOp",EDGE,"E11.11.0"),sQuery(id+"F0.wireOp",EDGE,"E11.11.1"),sQuery(id+"F0.wireOp",EDGE,"E11.11.2"),sQuery(id+"F0.wireOp",EDGE,"E11.12.0"),sQuery(id+"F0.wireOp",EDGE,"E11.12.1"),sQuery(id+"F0.wireOp",EDGE,"E11.12.2"),sQuery(id+"F0.wireOp",EDGE,"E11.13.0"),sQuery(id+"F0.wireOp",EDGE,"E11.13.1"),sQuery(id+"F0.wireOp",EDGE,"E11.13.2"),sQuery(id+"F0.wireOp",EDGE,"E11.14.0"),sQuery(id+"F0.wireOp",EDGE,"E11.14.1"),sQuery(id+"F0.wireOp",EDGE,"E11.14.2"),sQuery(id+"F0.wireOp",EDGE,"E11.15.0"),sQuery(id+"F0.wireOp",EDGE,"E11.15.1"),sQuery(id+"F0.wireOp",EDGE,"E11.15.2"),sQuery(id+"F0.wireOp",EDGE,"E11.16.0"),sQuery(id+"F0.wireOp",EDGE,"E11.16.1"),sQuery(id+"F0.wireOp",EDGE,"E11.16.2"),sQuery(id+"F0.wireOp",EDGE,"E11.17.0"),sQuery(id+"F0.wireOp",EDGE,"E11.17.1"),sQuery(id+"F0.wireOp",EDGE,"E11.17.2"),sQuery(id+"F0.wireOp",EDGE,"E11.18.0"),sQuery(id+"F0.wireOp",EDGE,"E11.18.1"),sQuery(id+"F0.wireOp",EDGE,"E11.18.2"),sQuery(id+"F0.wireOp",EDGE,"E11.19.0"),sQuery(id+"F0.wireOp",EDGE,"E11.19.1"),sQuery(id+"F0.wireOp",EDGE,"E11.19.2"),sQuery(id+"F0.wireOp",EDGE,"E11.20.0"),sQuery(id+"F0.wireOp",EDGE,"E11.20.1"),sQuery(id+"F0.wireOp",EDGE,"E11.20.2"),sQuery(id+"F0.wireOp",EDGE,"E11.21.0"),sQuery(id+"F0.wireOp",EDGE,"E11.21.1"),sQuery(id+"F0.wireOp",EDGE,"E11.21.2"),sQuery(id+"F0.wireOp",EDGE,"E11.22.0"),sQuery(id+"F0.wireOp",EDGE,"E11.22.1"),sQuery(id+"F0.wireOp",EDGE,"E11.22.2"),sQuery(id+"F0.wireOp",EDGE,"E11.23.0"),sQuery(id+"F0.wireOp",EDGE,"E11.23.1"),sQuery(id+"F0.wireOp",EDGE,"E11.23.2"),sQuery(id+"F0.wireOp",EDGE,"E11.24.0"),sQuery(id+"F0.wireOp",EDGE,"E11.24.1"),sQuery(id+"F0.wireOp",EDGE,"E11.24.2"),sQuery(id+"F0.wireOp",EDGE,"E11.25.0"),sQuery(id+"F0.wireOp",EDGE,"E11.25.1"),sQuery(id+"F0.wireOp",EDGE,"E11.25.2"),sQuery(id+"F0.wireOp",EDGE,"E11.26.0"),sQuery(id+"F0.wireOp",EDGE,"E11.26.1"),sQuery(id+"F0.wireOp",EDGE,"E11.26.2"),sQuery(id+"F0.wireOp",EDGE,"E11.27.0"),sQuery(id+"F0.wireOp",EDGE,"E11.27.1"),sQuery(id+"F0.wireOp",EDGE,"E11.27.2"),sQuery(id+"F0.wireOp",EDGE,"E11.28.0"),sQuery(id+"F0.wireOp",EDGE,"E11.28.1"),sQuery(id+"F0.wireOp",EDGE,"E11.28.2"),sQuery(id+"F0.wireOp",EDGE,"E11.29.0"),sQuery(id+"F0.wireOp",EDGE,"E11.29.1"),sQuery(id+"F0.wireOp",EDGE,"E11.29.2"),sQuery(id+"F0.wireOp",EDGE,"E12"),sQuery(id+"F0.wireOp",EDGE,"E14"),sQuery(id+"F0.wireOp",EDGE,"E15.1.0"),sQuery(id+"F0.wireOp",EDGE,"E15.2.0"),sQuery(id+"F0.wireOp",EDGE,"E15.3.0"),sQuery(id+"F0.wireOp",EDGE,"E15.4.0"),sQuery(id+"F0.wireOp",EDGE,"E15.5.0"),sQuery(id+"F0.wireOp",EDGE,"E15.6.0"),sQuery(id+"F0.wireOp",EDGE,"E15.7.0"),sQuery(id+"F0.wireOp",EDGE,"E15.8.0"),sQuery(id+"F0.wireOp",EDGE,"E15.9.0"),sQuery(id+"F0.wireOp",EDGE,"E15.10.0"),sQuery(id+"F0.wireOp",EDGE,"E15.11.0"),sQuery(id+"F0.wireOp",EDGE,"E15.12.0"),sQuery(id+"F0.wireOp",EDGE,"E15.13.0"),sQuery(id+"F0.wireOp",EDGE,"E15.14.0"),sQuery(id+"F0.wireOp",EDGE,"E15.15.0"),sQuery(id+"F0.wireOp",EDGE,"E15.16.0"),sQuery(id+"F0.wireOp",EDGE,"E15.17.0"),sQuery(id+"F0.wireOp",EDGE,"E15.18.0"),sQuery(id+"F0.wireOp",EDGE,"E15.19.0"),sQuery(id+"F0.wireOp",EDGE,"E15.20.0"),sQuery(id+"F0.wireOp",EDGE,"E15.21.0"),sQuery(id+"F0.wireOp",EDGE,"E15.22.0"),sQuery(id+"F0.wireOp",EDGE,"E15.23.0"),sQuery(id+"F0.wireOp",EDGE,"E15.24.0"),sQuery(id+"F0.wireOp",EDGE,"E15.25.0"),sQuery(id+"F0.wireOp",EDGE,"E15.26.0"),sQuery(id+"F0.wireOp",EDGE,"E15.27.0"),sQuery(id+"F0.wireOp",EDGE,"E15.28.0"),sQuery(id+"F0.wireOp",EDGE,"E15.29.0")])]});
            transform(context, id + "F11", {"entities" : qUnion([Q0]), "transformType" : TransformType.TRANSLATION_3D, "dx" : 0 * mm, "dy" : 8.46 * mm, "dz" : 0 * mm, "makeCopy" : true});
        }
        {
            var Q0;
            Q0=makeQuery(id+"F11.opPattern","COPY",BODY,{"derivedFrom":makeQuery(id+"F2.opExtrude","SWEPT_BODY",BODY,{"disambiguationData":[OSD([sQuery(id+"F0.wireOp",EDGE,"E0"),sQuery(id+"F0.wireOp",EDGE,"E2"),sQuery(id+"F0.wireOp",EDGE,"E4"),sQuery(id+"F0.wireOp",EDGE,"E5"),sQuery(id+"F0.wireOp",EDGE,"E6"),sQuery(id+"F0.wireOp",EDGE,"E7.1.0"),sQuery(id+"F0.wireOp",EDGE,"E7.1.1"),sQuery(id+"F0.wireOp",EDGE,"E7.1.3"),sQuery(id+"F0.wireOp",EDGE,"E7.2.0"),sQuery(id+"F0.wireOp",EDGE,"E7.2.1"),sQuery(id+"F0.wireOp",EDGE,"E7.2.3"),sQuery(id+"F0.wireOp",EDGE,"E7.3.0"),sQuery(id+"F0.wireOp",EDGE,"E7.3.1"),sQuery(id+"F0.wireOp",EDGE,"E7.3.3"),sQuery(id+"F0.wireOp",EDGE,"E7.4.0"),sQuery(id+"F0.wireOp",EDGE,"E7.4.1"),sQuery(id+"F0.wireOp",EDGE,"E7.4.3"),sQuery(id+"F0.wireOp",EDGE,"E7.5.0"),sQuery(id+"F0.wireOp",EDGE,"E7.5.1"),sQuery(id+"F0.wireOp",EDGE,"E7.5.3"),sQuery(id+"F0.wireOp",EDGE,"E7.6.0"),sQuery(id+"F0.wireOp",EDGE,"E7.6.1"),sQuery(id+"F0.wireOp",EDGE,"E7.6.3"),sQuery(id+"F0.wireOp",EDGE,"E7.7.0"),sQuery(id+"F0.wireOp",EDGE,"E7.7.1"),sQuery(id+"F0.wireOp",EDGE,"E7.7.3"),sQuery(id+"F0.wireOp",EDGE,"E7.8.0"),sQuery(id+"F0.wireOp",EDGE,"E7.8.1"),sQuery(id+"F0.wireOp",EDGE,"E7.8.3"),sQuery(id+"F0.wireOp",EDGE,"E7.9.0"),sQuery(id+"F0.wireOp",EDGE,"E7.9.1"),sQuery(id+"F0.wireOp",EDGE,"E7.9.3"),sQuery(id+"F0.wireOp",EDGE,"E7.10.0"),sQuery(id+"F0.wireOp",EDGE,"E7.10.1"),sQuery(id+"F0.wireOp",EDGE,"E7.10.3"),sQuery(id+"F0.wireOp",EDGE,"E7.11.0"),sQuery(id+"F0.wireOp",EDGE,"E7.11.1"),sQuery(id+"F0.wireOp",EDGE,"E7.11.3"),sQuery(id+"F0.wireOp",EDGE,"E7.12.0"),sQuery(id+"F0.wireOp",EDGE,"E7.12.1"),sQuery(id+"F0.wireOp",EDGE,"E7.12.3"),sQuery(id+"F0.wireOp",EDGE,"E7.13.0"),sQuery(id+"F0.wireOp",EDGE,"E7.13.1"),sQuery(id+"F0.wireOp",EDGE,"E7.13.3"),sQuery(id+"F0.wireOp",EDGE,"E7.14.0"),sQuery(id+"F0.wireOp",EDGE,"E7.14.1"),sQuery(id+"F0.wireOp",EDGE,"E7.14.3"),sQuery(id+"F0.wireOp",EDGE,"E7.15.0"),sQuery(id+"F0.wireOp",EDGE,"E7.15.1"),sQuery(id+"F0.wireOp",EDGE,"E7.15.3"),sQuery(id+"F0.wireOp",EDGE,"E7.16.0"),sQuery(id+"F0.wireOp",EDGE,"E7.16.1"),sQuery(id+"F0.wireOp",EDGE,"E7.16.3"),sQuery(id+"F0.wireOp",EDGE,"E7.17.0"),sQuery(id+"F0.wireOp",EDGE,"E7.17.1"),sQuery(id+"F0.wireOp",EDGE,"E7.17.3"),sQuery(id+"F0.wireOp",EDGE,"E7.18.0"),sQuery(id+"F0.wireOp",EDGE,"E7.18.1"),sQuery(id+"F0.wireOp",EDGE,"E7.18.3"),sQuery(id+"F0.wireOp",EDGE,"E7.19.0"),sQuery(id+"F0.wireOp",EDGE,"E7.19.1"),sQuery(id+"F0.wireOp",EDGE,"E7.19.3"),sQuery(id+"F0.wireOp",EDGE,"E7.20.0"),sQuery(id+"F0.wireOp",EDGE,"E7.20.1"),sQuery(id+"F0.wireOp",EDGE,"E7.20.3"),sQuery(id+"F0.wireOp",EDGE,"E7.21.0"),sQuery(id+"F0.wireOp",EDGE,"E7.21.1"),sQuery(id+"F0.wireOp",EDGE,"E7.21.3"),sQuery(id+"F0.wireOp",EDGE,"E7.22.0"),sQuery(id+"F0.wireOp",EDGE,"E7.22.1"),sQuery(id+"F0.wireOp",EDGE,"E7.22.3"),sQuery(id+"F0.wireOp",EDGE,"E7.23.0"),sQuery(id+"F0.wireOp",EDGE,"E7.23.1"),sQuery(id+"F0.wireOp",EDGE,"E7.23.3"),sQuery(id+"F0.wireOp",EDGE,"E7.24.0"),sQuery(id+"F0.wireOp",EDGE,"E7.24.1"),sQuery(id+"F0.wireOp",EDGE,"E7.24.3"),sQuery(id+"F0.wireOp",EDGE,"E7.25.0"),sQuery(id+"F0.wireOp",EDGE,"E7.25.1"),sQuery(id+"F0.wireOp",EDGE,"E7.25.3"),sQuery(id+"F0.wireOp",EDGE,"E7.26.0"),sQuery(id+"F0.wireOp",EDGE,"E7.26.1"),sQuery(id+"F0.wireOp",EDGE,"E7.26.3"),sQuery(id+"F0.wireOp",EDGE,"E7.27.0"),sQuery(id+"F0.wireOp",EDGE,"E7.27.1"),sQuery(id+"F0.wireOp",EDGE,"E7.27.3"),sQuery(id+"F0.wireOp",EDGE,"E7.28.0"),sQuery(id+"F0.wireOp",EDGE,"E7.28.1"),sQuery(id+"F0.wireOp",EDGE,"E7.28.3"),sQuery(id+"F0.wireOp",EDGE,"E7.29.0"),sQuery(id+"F0.wireOp",EDGE,"E7.29.1"),sQuery(id+"F0.wireOp",EDGE,"E7.29.3"),sQuery(id+"F0.wireOp",EDGE,"E8"),sQuery(id+"F0.wireOp",EDGE,"E9"),sQuery(id+"F0.wireOp",EDGE,"E10"),sQuery(id+"F0.wireOp",EDGE,"E11.1.0"),sQuery(id+"F0.wireOp",EDGE,"E11.1.1"),sQuery(id+"F0.wireOp",EDGE,"E11.1.2"),sQuery(id+"F0.wireOp",EDGE,"E11.2.0"),sQuery(id+"F0.wireOp",EDGE,"E11.2.1"),sQuery(id+"F0.wireOp",EDGE,"E11.2.2"),sQuery(id+"F0.wireOp",EDGE,"E11.3.0"),sQuery(id+"F0.wireOp",EDGE,"E11.3.1"),sQuery(id+"F0.wireOp",EDGE,"E11.3.2"),sQuery(id+"F0.wireOp",EDGE,"E11.4.0"),sQuery(id+"F0.wireOp",EDGE,"E11.4.1"),sQuery(id+"F0.wireOp",EDGE,"E11.4.2"),sQuery(id+"F0.wireOp",EDGE,"E11.5.0"),sQuery(id+"F0.wireOp",EDGE,"E11.5.1"),sQuery(id+"F0.wireOp",EDGE,"E11.5.2"),sQuery(id+"F0.wireOp",EDGE,"E11.6.0"),sQuery(id+"F0.wireOp",EDGE,"E11.6.1"),sQuery(id+"F0.wireOp",EDGE,"E11.6.2"),sQuery(id+"F0.wireOp",EDGE,"E11.7.0"),sQuery(id+"F0.wireOp",EDGE,"E11.7.1"),sQuery(id+"F0.wireOp",EDGE,"E11.7.2"),sQuery(id+"F0.wireOp",EDGE,"E11.8.0"),sQuery(id+"F0.wireOp",EDGE,"E11.8.1"),sQuery(id+"F0.wireOp",EDGE,"E11.8.2"),sQuery(id+"F0.wireOp",EDGE,"E11.9.0"),sQuery(id+"F0.wireOp",EDGE,"E11.9.1"),sQuery(id+"F0.wireOp",EDGE,"E11.9.2"),sQuery(id+"F0.wireOp",EDGE,"E11.10.0"),sQuery(id+"F0.wireOp",EDGE,"E11.10.1"),sQuery(id+"F0.wireOp",EDGE,"E11.10.2"),sQuery(id+"F0.wireOp",EDGE,"E11.11.0"),sQuery(id+"F0.wireOp",EDGE,"E11.11.1"),sQuery(id+"F0.wireOp",EDGE,"E11.11.2"),sQuery(id+"F0.wireOp",EDGE,"E11.12.0"),sQuery(id+"F0.wireOp",EDGE,"E11.12.1"),sQuery(id+"F0.wireOp",EDGE,"E11.12.2"),sQuery(id+"F0.wireOp",EDGE,"E11.13.0"),sQuery(id+"F0.wireOp",EDGE,"E11.13.1"),sQuery(id+"F0.wireOp",EDGE,"E11.13.2"),sQuery(id+"F0.wireOp",EDGE,"E11.14.0"),sQuery(id+"F0.wireOp",EDGE,"E11.14.1"),sQuery(id+"F0.wireOp",EDGE,"E11.14.2"),sQuery(id+"F0.wireOp",EDGE,"E11.15.0"),sQuery(id+"F0.wireOp",EDGE,"E11.15.1"),sQuery(id+"F0.wireOp",EDGE,"E11.15.2"),sQuery(id+"F0.wireOp",EDGE,"E11.16.0"),sQuery(id+"F0.wireOp",EDGE,"E11.16.1"),sQuery(id+"F0.wireOp",EDGE,"E11.16.2"),sQuery(id+"F0.wireOp",EDGE,"E11.17.0"),sQuery(id+"F0.wireOp",EDGE,"E11.17.1"),sQuery(id+"F0.wireOp",EDGE,"E11.17.2"),sQuery(id+"F0.wireOp",EDGE,"E11.18.0"),sQuery(id+"F0.wireOp",EDGE,"E11.18.1"),sQuery(id+"F0.wireOp",EDGE,"E11.18.2"),sQuery(id+"F0.wireOp",EDGE,"E11.19.0"),sQuery(id+"F0.wireOp",EDGE,"E11.19.1"),sQuery(id+"F0.wireOp",EDGE,"E11.19.2"),sQuery(id+"F0.wireOp",EDGE,"E11.20.0"),sQuery(id+"F0.wireOp",EDGE,"E11.20.1"),sQuery(id+"F0.wireOp",EDGE,"E11.20.2"),sQuery(id+"F0.wireOp",EDGE,"E11.21.0"),sQuery(id+"F0.wireOp",EDGE,"E11.21.1"),sQuery(id+"F0.wireOp",EDGE,"E11.21.2"),sQuery(id+"F0.wireOp",EDGE,"E11.22.0"),sQuery(id+"F0.wireOp",EDGE,"E11.22.1"),sQuery(id+"F0.wireOp",EDGE,"E11.22.2"),sQuery(id+"F0.wireOp",EDGE,"E11.23.0"),sQuery(id+"F0.wireOp",EDGE,"E11.23.1"),sQuery(id+"F0.wireOp",EDGE,"E11.23.2"),sQuery(id+"F0.wireOp",EDGE,"E11.24.0"),sQuery(id+"F0.wireOp",EDGE,"E11.24.1"),sQuery(id+"F0.wireOp",EDGE,"E11.24.2"),sQuery(id+"F0.wireOp",EDGE,"E11.25.0"),sQuery(id+"F0.wireOp",EDGE,"E11.25.1"),sQuery(id+"F0.wireOp",EDGE,"E11.25.2"),sQuery(id+"F0.wireOp",EDGE,"E11.26.0"),sQuery(id+"F0.wireOp",EDGE,"E11.26.1"),sQuery(id+"F0.wireOp",EDGE,"E11.26.2"),sQuery(id+"F0.wireOp",EDGE,"E11.27.0"),sQuery(id+"F0.wireOp",EDGE,"E11.27.1"),sQuery(id+"F0.wireOp",EDGE,"E11.27.2"),sQuery(id+"F0.wireOp",EDGE,"E11.28.0"),sQuery(id+"F0.wireOp",EDGE,"E11.28.1"),sQuery(id+"F0.wireOp",EDGE,"E11.28.2"),sQuery(id+"F0.wireOp",EDGE,"E11.29.0"),sQuery(id+"F0.wireOp",EDGE,"E11.29.1"),sQuery(id+"F0.wireOp",EDGE,"E11.29.2"),sQuery(id+"F0.wireOp",EDGE,"E12"),sQuery(id+"F0.wireOp",EDGE,"E14"),sQuery(id+"F0.wireOp",EDGE,"E15.1.0"),sQuery(id+"F0.wireOp",EDGE,"E15.2.0"),sQuery(id+"F0.wireOp",EDGE,"E15.3.0"),sQuery(id+"F0.wireOp",EDGE,"E15.4.0"),sQuery(id+"F0.wireOp",EDGE,"E15.5.0"),sQuery(id+"F0.wireOp",EDGE,"E15.6.0"),sQuery(id+"F0.wireOp",EDGE,"E15.7.0"),sQuery(id+"F0.wireOp",EDGE,"E15.8.0"),sQuery(id+"F0.wireOp",EDGE,"E15.9.0"),sQuery(id+"F0.wireOp",EDGE,"E15.10.0"),sQuery(id+"F0.wireOp",EDGE,"E15.11.0"),sQuery(id+"F0.wireOp",EDGE,"E15.12.0"),sQuery(id+"F0.wireOp",EDGE,"E15.13.0"),sQuery(id+"F0.wireOp",EDGE,"E15.14.0"),sQuery(id+"F0.wireOp",EDGE,"E15.15.0"),sQuery(id+"F0.wireOp",EDGE,"E15.16.0"),sQuery(id+"F0.wireOp",EDGE,"E15.17.0"),sQuery(id+"F0.wireOp",EDGE,"E15.18.0"),sQuery(id+"F0.wireOp",EDGE,"E15.19.0"),sQuery(id+"F0.wireOp",EDGE,"E15.20.0"),sQuery(id+"F0.wireOp",EDGE,"E15.21.0"),sQuery(id+"F0.wireOp",EDGE,"E15.22.0"),sQuery(id+"F0.wireOp",EDGE,"E15.23.0"),sQuery(id+"F0.wireOp",EDGE,"E15.24.0"),sQuery(id+"F0.wireOp",EDGE,"E15.25.0"),sQuery(id+"F0.wireOp",EDGE,"E15.26.0"),sQuery(id+"F0.wireOp",EDGE,"E15.27.0"),sQuery(id+"F0.wireOp",EDGE,"E15.28.0"),sQuery(id+"F0.wireOp",EDGE,"E15.29.0")])]}),"instanceName":"1"});
            var Q1;
            Q1=makeQuery(id+"F2.opExtrude","CAP_EDGE",EDGE,{"disambiguationData":[OSD([sQuery(id+"F0.wireOp",EDGE,"E0")])],"isStart":false});
            transform(context, id + "F12", {"entities" : qUnion([Q0]), "transformType" : TransformType.ROTATION, "transformAxis" : qUnion([Q1]), "angle" : 4 * degree, "makeCopy" : false});
        }
        {
            var Q0;
            Q0=makeQuery(id+"F11.opPattern","COPY",BODY,{"derivedFrom":makeQuery(id+"F2.opExtrude","SWEPT_BODY",BODY,{"disambiguationData":[OSD([sQuery(id+"F0.wireOp",EDGE,"E0"),sQuery(id+"F0.wireOp",EDGE,"E2"),sQuery(id+"F0.wireOp",EDGE,"E4"),sQuery(id+"F0.wireOp",EDGE,"E5"),sQuery(id+"F0.wireOp",EDGE,"E6"),sQuery(id+"F0.wireOp",EDGE,"E7.1.0"),sQuery(id+"F0.wireOp",EDGE,"E7.1.1"),sQuery(id+"F0.wireOp",EDGE,"E7.1.3"),sQuery(id+"F0.wireOp",EDGE,"E7.2.0"),sQuery(id+"F0.wireOp",EDGE,"E7.2.1"),sQuery(id+"F0.wireOp",EDGE,"E7.2.3"),sQuery(id+"F0.wireOp",EDGE,"E7.3.0"),sQuery(id+"F0.wireOp",EDGE,"E7.3.1"),sQuery(id+"F0.wireOp",EDGE,"E7.3.3"),sQuery(id+"F0.wireOp",EDGE,"E7.4.0"),sQuery(id+"F0.wireOp",EDGE,"E7.4.1"),sQuery(id+"F0.wireOp",EDGE,"E7.4.3"),sQuery(id+"F0.wireOp",EDGE,"E7.5.0"),sQuery(id+"F0.wireOp",EDGE,"E7.5.1"),sQuery(id+"F0.wireOp",EDGE,"E7.5.3"),sQuery(id+"F0.wireOp",EDGE,"E7.6.0"),sQuery(id+"F0.wireOp",EDGE,"E7.6.1"),sQuery(id+"F0.wireOp",EDGE,"E7.6.3"),sQuery(id+"F0.wireOp",EDGE,"E7.7.0"),sQuery(id+"F0.wireOp",EDGE,"E7.7.1"),sQuery(id+"F0.wireOp",EDGE,"E7.7.3"),sQuery(id+"F0.wireOp",EDGE,"E7.8.0"),sQuery(id+"F0.wireOp",EDGE,"E7.8.1"),sQuery(id+"F0.wireOp",EDGE,"E7.8.3"),sQuery(id+"F0.wireOp",EDGE,"E7.9.0"),sQuery(id+"F0.wireOp",EDGE,"E7.9.1"),sQuery(id+"F0.wireOp",EDGE,"E7.9.3"),sQuery(id+"F0.wireOp",EDGE,"E7.10.0"),sQuery(id+"F0.wireOp",EDGE,"E7.10.1"),sQuery(id+"F0.wireOp",EDGE,"E7.10.3"),sQuery(id+"F0.wireOp",EDGE,"E7.11.0"),sQuery(id+"F0.wireOp",EDGE,"E7.11.1"),sQuery(id+"F0.wireOp",EDGE,"E7.11.3"),sQuery(id+"F0.wireOp",EDGE,"E7.12.0"),sQuery(id+"F0.wireOp",EDGE,"E7.12.1"),sQuery(id+"F0.wireOp",EDGE,"E7.12.3"),sQuery(id+"F0.wireOp",EDGE,"E7.13.0"),sQuery(id+"F0.wireOp",EDGE,"E7.13.1"),sQuery(id+"F0.wireOp",EDGE,"E7.13.3"),sQuery(id+"F0.wireOp",EDGE,"E7.14.0"),sQuery(id+"F0.wireOp",EDGE,"E7.14.1"),sQuery(id+"F0.wireOp",EDGE,"E7.14.3"),sQuery(id+"F0.wireOp",EDGE,"E7.15.0"),sQuery(id+"F0.wireOp",EDGE,"E7.15.1"),sQuery(id+"F0.wireOp",EDGE,"E7.15.3"),sQuery(id+"F0.wireOp",EDGE,"E7.16.0"),sQuery(id+"F0.wireOp",EDGE,"E7.16.1"),sQuery(id+"F0.wireOp",EDGE,"E7.16.3"),sQuery(id+"F0.wireOp",EDGE,"E7.17.0"),sQuery(id+"F0.wireOp",EDGE,"E7.17.1"),sQuery(id+"F0.wireOp",EDGE,"E7.17.3"),sQuery(id+"F0.wireOp",EDGE,"E7.18.0"),sQuery(id+"F0.wireOp",EDGE,"E7.18.1"),sQuery(id+"F0.wireOp",EDGE,"E7.18.3"),sQuery(id+"F0.wireOp",EDGE,"E7.19.0"),sQuery(id+"F0.wireOp",EDGE,"E7.19.1"),sQuery(id+"F0.wireOp",EDGE,"E7.19.3"),sQuery(id+"F0.wireOp",EDGE,"E7.20.0"),sQuery(id+"F0.wireOp",EDGE,"E7.20.1"),sQuery(id+"F0.wireOp",EDGE,"E7.20.3"),sQuery(id+"F0.wireOp",EDGE,"E7.21.0"),sQuery(id+"F0.wireOp",EDGE,"E7.21.1"),sQuery(id+"F0.wireOp",EDGE,"E7.21.3"),sQuery(id+"F0.wireOp",EDGE,"E7.22.0"),sQuery(id+"F0.wireOp",EDGE,"E7.22.1"),sQuery(id+"F0.wireOp",EDGE,"E7.22.3"),sQuery(id+"F0.wireOp",EDGE,"E7.23.0"),sQuery(id+"F0.wireOp",EDGE,"E7.23.1"),sQuery(id+"F0.wireOp",EDGE,"E7.23.3"),sQuery(id+"F0.wireOp",EDGE,"E7.24.0"),sQuery(id+"F0.wireOp",EDGE,"E7.24.1"),sQuery(id+"F0.wireOp",EDGE,"E7.24.3"),sQuery(id+"F0.wireOp",EDGE,"E7.25.0"),sQuery(id+"F0.wireOp",EDGE,"E7.25.1"),sQuery(id+"F0.wireOp",EDGE,"E7.25.3"),sQuery(id+"F0.wireOp",EDGE,"E7.26.0"),sQuery(id+"F0.wireOp",EDGE,"E7.26.1"),sQuery(id+"F0.wireOp",EDGE,"E7.26.3"),sQuery(id+"F0.wireOp",EDGE,"E7.27.0"),sQuery(id+"F0.wireOp",EDGE,"E7.27.1"),sQuery(id+"F0.wireOp",EDGE,"E7.27.3"),sQuery(id+"F0.wireOp",EDGE,"E7.28.0"),sQuery(id+"F0.wireOp",EDGE,"E7.28.1"),sQuery(id+"F0.wireOp",EDGE,"E7.28.3"),sQuery(id+"F0.wireOp",EDGE,"E7.29.0"),sQuery(id+"F0.wireOp",EDGE,"E7.29.1"),sQuery(id+"F0.wireOp",EDGE,"E7.29.3"),sQuery(id+"F0.wireOp",EDGE,"E8"),sQuery(id+"F0.wireOp",EDGE,"E9"),sQuery(id+"F0.wireOp",EDGE,"E10"),sQuery(id+"F0.wireOp",EDGE,"E11.1.0"),sQuery(id+"F0.wireOp",EDGE,"E11.1.1"),sQuery(id+"F0.wireOp",EDGE,"E11.1.2"),sQuery(id+"F0.wireOp",EDGE,"E11.2.0"),sQuery(id+"F0.wireOp",EDGE,"E11.2.1"),sQuery(id+"F0.wireOp",EDGE,"E11.2.2"),sQuery(id+"F0.wireOp",EDGE,"E11.3.0"),sQuery(id+"F0.wireOp",EDGE,"E11.3.1"),sQuery(id+"F0.wireOp",EDGE,"E11.3.2"),sQuery(id+"F0.wireOp",EDGE,"E11.4.0"),sQuery(id+"F0.wireOp",EDGE,"E11.4.1"),sQuery(id+"F0.wireOp",EDGE,"E11.4.2"),sQuery(id+"F0.wireOp",EDGE,"E11.5.0"),sQuery(id+"F0.wireOp",EDGE,"E11.5.1"),sQuery(id+"F0.wireOp",EDGE,"E11.5.2"),sQuery(id+"F0.wireOp",EDGE,"E11.6.0"),sQuery(id+"F0.wireOp",EDGE,"E11.6.1"),sQuery(id+"F0.wireOp",EDGE,"E11.6.2"),sQuery(id+"F0.wireOp",EDGE,"E11.7.0"),sQuery(id+"F0.wireOp",EDGE,"E11.7.1"),sQuery(id+"F0.wireOp",EDGE,"E11.7.2"),sQuery(id+"F0.wireOp",EDGE,"E11.8.0"),sQuery(id+"F0.wireOp",EDGE,"E11.8.1"),sQuery(id+"F0.wireOp",EDGE,"E11.8.2"),sQuery(id+"F0.wireOp",EDGE,"E11.9.0"),sQuery(id+"F0.wireOp",EDGE,"E11.9.1"),sQuery(id+"F0.wireOp",EDGE,"E11.9.2"),sQuery(id+"F0.wireOp",EDGE,"E11.10.0"),sQuery(id+"F0.wireOp",EDGE,"E11.10.1"),sQuery(id+"F0.wireOp",EDGE,"E11.10.2"),sQuery(id+"F0.wireOp",EDGE,"E11.11.0"),sQuery(id+"F0.wireOp",EDGE,"E11.11.1"),sQuery(id+"F0.wireOp",EDGE,"E11.11.2"),sQuery(id+"F0.wireOp",EDGE,"E11.12.0"),sQuery(id+"F0.wireOp",EDGE,"E11.12.1"),sQuery(id+"F0.wireOp",EDGE,"E11.12.2"),sQuery(id+"F0.wireOp",EDGE,"E11.13.0"),sQuery(id+"F0.wireOp",EDGE,"E11.13.1"),sQuery(id+"F0.wireOp",EDGE,"E11.13.2"),sQuery(id+"F0.wireOp",EDGE,"E11.14.0"),sQuery(id+"F0.wireOp",EDGE,"E11.14.1"),sQuery(id+"F0.wireOp",EDGE,"E11.14.2"),sQuery(id+"F0.wireOp",EDGE,"E11.15.0"),sQuery(id+"F0.wireOp",EDGE,"E11.15.1"),sQuery(id+"F0.wireOp",EDGE,"E11.15.2"),sQuery(id+"F0.wireOp",EDGE,"E11.16.0"),sQuery(id+"F0.wireOp",EDGE,"E11.16.1"),sQuery(id+"F0.wireOp",EDGE,"E11.16.2"),sQuery(id+"F0.wireOp",EDGE,"E11.17.0"),sQuery(id+"F0.wireOp",EDGE,"E11.17.1"),sQuery(id+"F0.wireOp",EDGE,"E11.17.2"),sQuery(id+"F0.wireOp",EDGE,"E11.18.0"),sQuery(id+"F0.wireOp",EDGE,"E11.18.1"),sQuery(id+"F0.wireOp",EDGE,"E11.18.2"),sQuery(id+"F0.wireOp",EDGE,"E11.19.0"),sQuery(id+"F0.wireOp",EDGE,"E11.19.1"),sQuery(id+"F0.wireOp",EDGE,"E11.19.2"),sQuery(id+"F0.wireOp",EDGE,"E11.20.0"),sQuery(id+"F0.wireOp",EDGE,"E11.20.1"),sQuery(id+"F0.wireOp",EDGE,"E11.20.2"),sQuery(id+"F0.wireOp",EDGE,"E11.21.0"),sQuery(id+"F0.wireOp",EDGE,"E11.21.1"),sQuery(id+"F0.wireOp",EDGE,"E11.21.2"),sQuery(id+"F0.wireOp",EDGE,"E11.22.0"),sQuery(id+"F0.wireOp",EDGE,"E11.22.1"),sQuery(id+"F0.wireOp",EDGE,"E11.22.2"),sQuery(id+"F0.wireOp",EDGE,"E11.23.0"),sQuery(id+"F0.wireOp",EDGE,"E11.23.1"),sQuery(id+"F0.wireOp",EDGE,"E11.23.2"),sQuery(id+"F0.wireOp",EDGE,"E11.24.0"),sQuery(id+"F0.wireOp",EDGE,"E11.24.1"),sQuery(id+"F0.wireOp",EDGE,"E11.24.2"),sQuery(id+"F0.wireOp",EDGE,"E11.25.0"),sQuery(id+"F0.wireOp",EDGE,"E11.25.1"),sQuery(id+"F0.wireOp",EDGE,"E11.25.2"),sQuery(id+"F0.wireOp",EDGE,"E11.26.0"),sQuery(id+"F0.wireOp",EDGE,"E11.26.1"),sQuery(id+"F0.wireOp",EDGE,"E11.26.2"),sQuery(id+"F0.wireOp",EDGE,"E11.27.0"),sQuery(id+"F0.wireOp",EDGE,"E11.27.1"),sQuery(id+"F0.wireOp",EDGE,"E11.27.2"),sQuery(id+"F0.wireOp",EDGE,"E11.28.0"),sQuery(id+"F0.wireOp",EDGE,"E11.28.1"),sQuery(id+"F0.wireOp",EDGE,"E11.28.2"),sQuery(id+"F0.wireOp",EDGE,"E11.29.0"),sQuery(id+"F0.wireOp",EDGE,"E11.29.1"),sQuery(id+"F0.wireOp",EDGE,"E11.29.2"),sQuery(id+"F0.wireOp",EDGE,"E12"),sQuery(id+"F0.wireOp",EDGE,"E14"),sQuery(id+"F0.wireOp",EDGE,"E15.1.0"),sQuery(id+"F0.wireOp",EDGE,"E15.2.0"),sQuery(id+"F0.wireOp",EDGE,"E15.3.0"),sQuery(id+"F0.wireOp",EDGE,"E15.4.0"),sQuery(id+"F0.wireOp",EDGE,"E15.5.0"),sQuery(id+"F0.wireOp",EDGE,"E15.6.0"),sQuery(id+"F0.wireOp",EDGE,"E15.7.0"),sQuery(id+"F0.wireOp",EDGE,"E15.8.0"),sQuery(id+"F0.wireOp",EDGE,"E15.9.0"),sQuery(id+"F0.wireOp",EDGE,"E15.10.0"),sQuery(id+"F0.wireOp",EDGE,"E15.11.0"),sQuery(id+"F0.wireOp",EDGE,"E15.12.0"),sQuery(id+"F0.wireOp",EDGE,"E15.13.0"),sQuery(id+"F0.wireOp",EDGE,"E15.14.0"),sQuery(id+"F0.wireOp",EDGE,"E15.15.0"),sQuery(id+"F0.wireOp",EDGE,"E15.16.0"),sQuery(id+"F0.wireOp",EDGE,"E15.17.0"),sQuery(id+"F0.wireOp",EDGE,"E15.18.0"),sQuery(id+"F0.wireOp",EDGE,"E15.19.0"),sQuery(id+"F0.wireOp",EDGE,"E15.20.0"),sQuery(id+"F0.wireOp",EDGE,"E15.21.0"),sQuery(id+"F0.wireOp",EDGE,"E15.22.0"),sQuery(id+"F0.wireOp",EDGE,"E15.23.0"),sQuery(id+"F0.wireOp",EDGE,"E15.24.0"),sQuery(id+"F0.wireOp",EDGE,"E15.25.0"),sQuery(id+"F0.wireOp",EDGE,"E15.26.0"),sQuery(id+"F0.wireOp",EDGE,"E15.27.0"),sQuery(id+"F0.wireOp",EDGE,"E15.28.0"),sQuery(id+"F0.wireOp",EDGE,"E15.29.0")])]}),"instanceName":"1"});
            transform(context, id + "F13", {"entities" : qUnion([Q0]), "transformType" : TransformType.TRANSLATION_3D, "dx" : 0 * mm, "dy" : 8.46 * mm, "dz" : 0 * mm, "makeCopy" : true});
        }
        {
            var Q0;
            Q0=makeQuery(id+"F13.opPattern","COPY",BODY,{"derivedFrom":makeQuery(id+"F11.opPattern","COPY",BODY,{"derivedFrom":makeQuery(id+"F2.opExtrude","SWEPT_BODY",BODY,{"disambiguationData":[OSD([sQuery(id+"F0.wireOp",EDGE,"E0"),sQuery(id+"F0.wireOp",EDGE,"E2"),sQuery(id+"F0.wireOp",EDGE,"E4"),sQuery(id+"F0.wireOp",EDGE,"E5"),sQuery(id+"F0.wireOp",EDGE,"E6"),sQuery(id+"F0.wireOp",EDGE,"E7.1.0"),sQuery(id+"F0.wireOp",EDGE,"E7.1.1"),sQuery(id+"F0.wireOp",EDGE,"E7.1.3"),sQuery(id+"F0.wireOp",EDGE,"E7.2.0"),sQuery(id+"F0.wireOp",EDGE,"E7.2.1"),sQuery(id+"F0.wireOp",EDGE,"E7.2.3"),sQuery(id+"F0.wireOp",EDGE,"E7.3.0"),sQuery(id+"F0.wireOp",EDGE,"E7.3.1"),sQuery(id+"F0.wireOp",EDGE,"E7.3.3"),sQuery(id+"F0.wireOp",EDGE,"E7.4.0"),sQuery(id+"F0.wireOp",EDGE,"E7.4.1"),sQuery(id+"F0.wireOp",EDGE,"E7.4.3"),sQuery(id+"F0.wireOp",EDGE,"E7.5.0"),sQuery(id+"F0.wireOp",EDGE,"E7.5.1"),sQuery(id+"F0.wireOp",EDGE,"E7.5.3"),sQuery(id+"F0.wireOp",EDGE,"E7.6.0"),sQuery(id+"F0.wireOp",EDGE,"E7.6.1"),sQuery(id+"F0.wireOp",EDGE,"E7.6.3"),sQuery(id+"F0.wireOp",EDGE,"E7.7.0"),sQuery(id+"F0.wireOp",EDGE,"E7.7.1"),sQuery(id+"F0.wireOp",EDGE,"E7.7.3"),sQuery(id+"F0.wireOp",EDGE,"E7.8.0"),sQuery(id+"F0.wireOp",EDGE,"E7.8.1"),sQuery(id+"F0.wireOp",EDGE,"E7.8.3"),sQuery(id+"F0.wireOp",EDGE,"E7.9.0"),sQuery(id+"F0.wireOp",EDGE,"E7.9.1"),sQuery(id+"F0.wireOp",EDGE,"E7.9.3"),sQuery(id+"F0.wireOp",EDGE,"E7.10.0"),sQuery(id+"F0.wireOp",EDGE,"E7.10.1"),sQuery(id+"F0.wireOp",EDGE,"E7.10.3"),sQuery(id+"F0.wireOp",EDGE,"E7.11.0"),sQuery(id+"F0.wireOp",EDGE,"E7.11.1"),sQuery(id+"F0.wireOp",EDGE,"E7.11.3"),sQuery(id+"F0.wireOp",EDGE,"E7.12.0"),sQuery(id+"F0.wireOp",EDGE,"E7.12.1"),sQuery(id+"F0.wireOp",EDGE,"E7.12.3"),sQuery(id+"F0.wireOp",EDGE,"E7.13.0"),sQuery(id+"F0.wireOp",EDGE,"E7.13.1"),sQuery(id+"F0.wireOp",EDGE,"E7.13.3"),sQuery(id+"F0.wireOp",EDGE,"E7.14.0"),sQuery(id+"F0.wireOp",EDGE,"E7.14.1"),sQuery(id+"F0.wireOp",EDGE,"E7.14.3"),sQuery(id+"F0.wireOp",EDGE,"E7.15.0"),sQuery(id+"F0.wireOp",EDGE,"E7.15.1"),sQuery(id+"F0.wireOp",EDGE,"E7.15.3"),sQuery(id+"F0.wireOp",EDGE,"E7.16.0"),sQuery(id+"F0.wireOp",EDGE,"E7.16.1"),sQuery(id+"F0.wireOp",EDGE,"E7.16.3"),sQuery(id+"F0.wireOp",EDGE,"E7.17.0"),sQuery(id+"F0.wireOp",EDGE,"E7.17.1"),sQuery(id+"F0.wireOp",EDGE,"E7.17.3"),sQuery(id+"F0.wireOp",EDGE,"E7.18.0"),sQuery(id+"F0.wireOp",EDGE,"E7.18.1"),sQuery(id+"F0.wireOp",EDGE,"E7.18.3"),sQuery(id+"F0.wireOp",EDGE,"E7.19.0"),sQuery(id+"F0.wireOp",EDGE,"E7.19.1"),sQuery(id+"F0.wireOp",EDGE,"E7.19.3"),sQuery(id+"F0.wireOp",EDGE,"E7.20.0"),sQuery(id+"F0.wireOp",EDGE,"E7.20.1"),sQuery(id+"F0.wireOp",EDGE,"E7.20.3"),sQuery(id+"F0.wireOp",EDGE,"E7.21.0"),sQuery(id+"F0.wireOp",EDGE,"E7.21.1"),sQuery(id+"F0.wireOp",EDGE,"E7.21.3"),sQuery(id+"F0.wireOp",EDGE,"E7.22.0"),sQuery(id+"F0.wireOp",EDGE,"E7.22.1"),sQuery(id+"F0.wireOp",EDGE,"E7.22.3"),sQuery(id+"F0.wireOp",EDGE,"E7.23.0"),sQuery(id+"F0.wireOp",EDGE,"E7.23.1"),sQuery(id+"F0.wireOp",EDGE,"E7.23.3"),sQuery(id+"F0.wireOp",EDGE,"E7.24.0"),sQuery(id+"F0.wireOp",EDGE,"E7.24.1"),sQuery(id+"F0.wireOp",EDGE,"E7.24.3"),sQuery(id+"F0.wireOp",EDGE,"E7.25.0"),sQuery(id+"F0.wireOp",EDGE,"E7.25.1"),sQuery(id+"F0.wireOp",EDGE,"E7.25.3"),sQuery(id+"F0.wireOp",EDGE,"E7.26.0"),sQuery(id+"F0.wireOp",EDGE,"E7.26.1"),sQuery(id+"F0.wireOp",EDGE,"E7.26.3"),sQuery(id+"F0.wireOp",EDGE,"E7.27.0"),sQuery(id+"F0.wireOp",EDGE,"E7.27.1"),sQuery(id+"F0.wireOp",EDGE,"E7.27.3"),sQuery(id+"F0.wireOp",EDGE,"E7.28.0"),sQuery(id+"F0.wireOp",EDGE,"E7.28.1"),sQuery(id+"F0.wireOp",EDGE,"E7.28.3"),sQuery(id+"F0.wireOp",EDGE,"E7.29.0"),sQuery(id+"F0.wireOp",EDGE,"E7.29.1"),sQuery(id+"F0.wireOp",EDGE,"E7.29.3"),sQuery(id+"F0.wireOp",EDGE,"E8"),sQuery(id+"F0.wireOp",EDGE,"E9"),sQuery(id+"F0.wireOp",EDGE,"E10"),sQuery(id+"F0.wireOp",EDGE,"E11.1.0"),sQuery(id+"F0.wireOp",EDGE,"E11.1.1"),sQuery(id+"F0.wireOp",EDGE,"E11.1.2"),sQuery(id+"F0.wireOp",EDGE,"E11.2.0"),sQuery(id+"F0.wireOp",EDGE,"E11.2.1"),sQuery(id+"F0.wireOp",EDGE,"E11.2.2"),sQuery(id+"F0.wireOp",EDGE,"E11.3.0"),sQuery(id+"F0.wireOp",EDGE,"E11.3.1"),sQuery(id+"F0.wireOp",EDGE,"E11.3.2"),sQuery(id+"F0.wireOp",EDGE,"E11.4.0"),sQuery(id+"F0.wireOp",EDGE,"E11.4.1"),sQuery(id+"F0.wireOp",EDGE,"E11.4.2"),sQuery(id+"F0.wireOp",EDGE,"E11.5.0"),sQuery(id+"F0.wireOp",EDGE,"E11.5.1"),sQuery(id+"F0.wireOp",EDGE,"E11.5.2"),sQuery(id+"F0.wireOp",EDGE,"E11.6.0"),sQuery(id+"F0.wireOp",EDGE,"E11.6.1"),sQuery(id+"F0.wireOp",EDGE,"E11.6.2"),sQuery(id+"F0.wireOp",EDGE,"E11.7.0"),sQuery(id+"F0.wireOp",EDGE,"E11.7.1"),sQuery(id+"F0.wireOp",EDGE,"E11.7.2"),sQuery(id+"F0.wireOp",EDGE,"E11.8.0"),sQuery(id+"F0.wireOp",EDGE,"E11.8.1"),sQuery(id+"F0.wireOp",EDGE,"E11.8.2"),sQuery(id+"F0.wireOp",EDGE,"E11.9.0"),sQuery(id+"F0.wireOp",EDGE,"E11.9.1"),sQuery(id+"F0.wireOp",EDGE,"E11.9.2"),sQuery(id+"F0.wireOp",EDGE,"E11.10.0"),sQuery(id+"F0.wireOp",EDGE,"E11.10.1"),sQuery(id+"F0.wireOp",EDGE,"E11.10.2"),sQuery(id+"F0.wireOp",EDGE,"E11.11.0"),sQuery(id+"F0.wireOp",EDGE,"E11.11.1"),sQuery(id+"F0.wireOp",EDGE,"E11.11.2"),sQuery(id+"F0.wireOp",EDGE,"E11.12.0"),sQuery(id+"F0.wireOp",EDGE,"E11.12.1"),sQuery(id+"F0.wireOp",EDGE,"E11.12.2"),sQuery(id+"F0.wireOp",EDGE,"E11.13.0"),sQuery(id+"F0.wireOp",EDGE,"E11.13.1"),sQuery(id+"F0.wireOp",EDGE,"E11.13.2"),sQuery(id+"F0.wireOp",EDGE,"E11.14.0"),sQuery(id+"F0.wireOp",EDGE,"E11.14.1"),sQuery(id+"F0.wireOp",EDGE,"E11.14.2"),sQuery(id+"F0.wireOp",EDGE,"E11.15.0"),sQuery(id+"F0.wireOp",EDGE,"E11.15.1"),sQuery(id+"F0.wireOp",EDGE,"E11.15.2"),sQuery(id+"F0.wireOp",EDGE,"E11.16.0"),sQuery(id+"F0.wireOp",EDGE,"E11.16.1"),sQuery(id+"F0.wireOp",EDGE,"E11.16.2"),sQuery(id+"F0.wireOp",EDGE,"E11.17.0"),sQuery(id+"F0.wireOp",EDGE,"E11.17.1"),sQuery(id+"F0.wireOp",EDGE,"E11.17.2"),sQuery(id+"F0.wireOp",EDGE,"E11.18.0"),sQuery(id+"F0.wireOp",EDGE,"E11.18.1"),sQuery(id+"F0.wireOp",EDGE,"E11.18.2"),sQuery(id+"F0.wireOp",EDGE,"E11.19.0"),sQuery(id+"F0.wireOp",EDGE,"E11.19.1"),sQuery(id+"F0.wireOp",EDGE,"E11.19.2"),sQuery(id+"F0.wireOp",EDGE,"E11.20.0"),sQuery(id+"F0.wireOp",EDGE,"E11.20.1"),sQuery(id+"F0.wireOp",EDGE,"E11.20.2"),sQuery(id+"F0.wireOp",EDGE,"E11.21.0"),sQuery(id+"F0.wireOp",EDGE,"E11.21.1"),sQuery(id+"F0.wireOp",EDGE,"E11.21.2"),sQuery(id+"F0.wireOp",EDGE,"E11.22.0"),sQuery(id+"F0.wireOp",EDGE,"E11.22.1"),sQuery(id+"F0.wireOp",EDGE,"E11.22.2"),sQuery(id+"F0.wireOp",EDGE,"E11.23.0"),sQuery(id+"F0.wireOp",EDGE,"E11.23.1"),sQuery(id+"F0.wireOp",EDGE,"E11.23.2"),sQuery(id+"F0.wireOp",EDGE,"E11.24.0"),sQuery(id+"F0.wireOp",EDGE,"E11.24.1"),sQuery(id+"F0.wireOp",EDGE,"E11.24.2"),sQuery(id+"F0.wireOp",EDGE,"E11.25.0"),sQuery(id+"F0.wireOp",EDGE,"E11.25.1"),sQuery(id+"F0.wireOp",EDGE,"E11.25.2"),sQuery(id+"F0.wireOp",EDGE,"E11.26.0"),sQuery(id+"F0.wireOp",EDGE,"E11.26.1"),sQuery(id+"F0.wireOp",EDGE,"E11.26.2"),sQuery(id+"F0.wireOp",EDGE,"E11.27.0"),sQuery(id+"F0.wireOp",EDGE,"E11.27.1"),sQuery(id+"F0.wireOp",EDGE,"E11.27.2"),sQuery(id+"F0.wireOp",EDGE,"E11.28.0"),sQuery(id+"F0.wireOp",EDGE,"E11.28.1"),sQuery(id+"F0.wireOp",EDGE,"E11.28.2"),sQuery(id+"F0.wireOp",EDGE,"E11.29.0"),sQuery(id+"F0.wireOp",EDGE,"E11.29.1"),sQuery(id+"F0.wireOp",EDGE,"E11.29.2"),sQuery(id+"F0.wireOp",EDGE,"E12"),sQuery(id+"F0.wireOp",EDGE,"E14"),sQuery(id+"F0.wireOp",EDGE,"E15.1.0"),sQuery(id+"F0.wireOp",EDGE,"E15.2.0"),sQuery(id+"F0.wireOp",EDGE,"E15.3.0"),sQuery(id+"F0.wireOp",EDGE,"E15.4.0"),sQuery(id+"F0.wireOp",EDGE,"E15.5.0"),sQuery(id+"F0.wireOp",EDGE,"E15.6.0"),sQuery(id+"F0.wireOp",EDGE,"E15.7.0"),sQuery(id+"F0.wireOp",EDGE,"E15.8.0"),sQuery(id+"F0.wireOp",EDGE,"E15.9.0"),sQuery(id+"F0.wireOp",EDGE,"E15.10.0"),sQuery(id+"F0.wireOp",EDGE,"E15.11.0"),sQuery(id+"F0.wireOp",EDGE,"E15.12.0"),sQuery(id+"F0.wireOp",EDGE,"E15.13.0"),sQuery(id+"F0.wireOp",EDGE,"E15.14.0"),sQuery(id+"F0.wireOp",EDGE,"E15.15.0"),sQuery(id+"F0.wireOp",EDGE,"E15.16.0"),sQuery(id+"F0.wireOp",EDGE,"E15.17.0"),sQuery(id+"F0.wireOp",EDGE,"E15.18.0"),sQuery(id+"F0.wireOp",EDGE,"E15.19.0"),sQuery(id+"F0.wireOp",EDGE,"E15.20.0"),sQuery(id+"F0.wireOp",EDGE,"E15.21.0"),sQuery(id+"F0.wireOp",EDGE,"E15.22.0"),sQuery(id+"F0.wireOp",EDGE,"E15.23.0"),sQuery(id+"F0.wireOp",EDGE,"E15.24.0"),sQuery(id+"F0.wireOp",EDGE,"E15.25.0"),sQuery(id+"F0.wireOp",EDGE,"E15.26.0"),sQuery(id+"F0.wireOp",EDGE,"E15.27.0"),sQuery(id+"F0.wireOp",EDGE,"E15.28.0"),sQuery(id+"F0.wireOp",EDGE,"E15.29.0")])]}),"instanceName":"1"}),"instanceName":"1"});
            var Q1;
            Q1=makeQuery(id+"F2.opExtrude","CAP_EDGE",EDGE,{"disambiguationData":[OSD([sQuery(id+"F0.wireOp",EDGE,"E0")])],"isStart":false});
            transform(context, id + "F14", {"entities" : qUnion([Q0]), "transformType" : TransformType.ROTATION, "transformAxis" : qUnion([Q1]), "angle" : 4 * degree, "makeCopy" : false});
        }
        {
            var Q0;
            Q0=makeQuery(id+"F4.opPattern","COPY",BODY,{"derivedFrom":makeQuery(id+"F2.opExtrude","SWEPT_BODY",BODY,{"disambiguationData":[OSD([sQuery(id+"F0.wireOp",EDGE,"E0"),sQuery(id+"F0.wireOp",EDGE,"E2"),sQuery(id+"F0.wireOp",EDGE,"E4"),sQuery(id+"F0.wireOp",EDGE,"E5"),sQuery(id+"F0.wireOp",EDGE,"E6"),sQuery(id+"F0.wireOp",EDGE,"E7.1.0"),sQuery(id+"F0.wireOp",EDGE,"E7.1.1"),sQuery(id+"F0.wireOp",EDGE,"E7.1.3"),sQuery(id+"F0.wireOp",EDGE,"E7.2.0"),sQuery(id+"F0.wireOp",EDGE,"E7.2.1"),sQuery(id+"F0.wireOp",EDGE,"E7.2.3"),sQuery(id+"F0.wireOp",EDGE,"E7.3.0"),sQuery(id+"F0.wireOp",EDGE,"E7.3.1"),sQuery(id+"F0.wireOp",EDGE,"E7.3.3"),sQuery(id+"F0.wireOp",EDGE,"E7.4.0"),sQuery(id+"F0.wireOp",EDGE,"E7.4.1"),sQuery(id+"F0.wireOp",EDGE,"E7.4.3"),sQuery(id+"F0.wireOp",EDGE,"E7.5.0"),sQuery(id+"F0.wireOp",EDGE,"E7.5.1"),sQuery(id+"F0.wireOp",EDGE,"E7.5.3"),sQuery(id+"F0.wireOp",EDGE,"E7.6.0"),sQuery(id+"F0.wireOp",EDGE,"E7.6.1"),sQuery(id+"F0.wireOp",EDGE,"E7.6.3"),sQuery(id+"F0.wireOp",EDGE,"E7.7.0"),sQuery(id+"F0.wireOp",EDGE,"E7.7.1"),sQuery(id+"F0.wireOp",EDGE,"E7.7.3"),sQuery(id+"F0.wireOp",EDGE,"E7.8.0"),sQuery(id+"F0.wireOp",EDGE,"E7.8.1"),sQuery(id+"F0.wireOp",EDGE,"E7.8.3"),sQuery(id+"F0.wireOp",EDGE,"E7.9.0"),sQuery(id+"F0.wireOp",EDGE,"E7.9.1"),sQuery(id+"F0.wireOp",EDGE,"E7.9.3"),sQuery(id+"F0.wireOp",EDGE,"E7.10.0"),sQuery(id+"F0.wireOp",EDGE,"E7.10.1"),sQuery(id+"F0.wireOp",EDGE,"E7.10.3"),sQuery(id+"F0.wireOp",EDGE,"E7.11.0"),sQuery(id+"F0.wireOp",EDGE,"E7.11.1"),sQuery(id+"F0.wireOp",EDGE,"E7.11.3"),sQuery(id+"F0.wireOp",EDGE,"E7.12.0"),sQuery(id+"F0.wireOp",EDGE,"E7.12.1"),sQuery(id+"F0.wireOp",EDGE,"E7.12.3"),sQuery(id+"F0.wireOp",EDGE,"E7.13.0"),sQuery(id+"F0.wireOp",EDGE,"E7.13.1"),sQuery(id+"F0.wireOp",EDGE,"E7.13.3"),sQuery(id+"F0.wireOp",EDGE,"E7.14.0"),sQuery(id+"F0.wireOp",EDGE,"E7.14.1"),sQuery(id+"F0.wireOp",EDGE,"E7.14.3"),sQuery(id+"F0.wireOp",EDGE,"E7.15.0"),sQuery(id+"F0.wireOp",EDGE,"E7.15.1"),sQuery(id+"F0.wireOp",EDGE,"E7.15.3"),sQuery(id+"F0.wireOp",EDGE,"E7.16.0"),sQuery(id+"F0.wireOp",EDGE,"E7.16.1"),sQuery(id+"F0.wireOp",EDGE,"E7.16.3"),sQuery(id+"F0.wireOp",EDGE,"E7.17.0"),sQuery(id+"F0.wireOp",EDGE,"E7.17.1"),sQuery(id+"F0.wireOp",EDGE,"E7.17.3"),sQuery(id+"F0.wireOp",EDGE,"E7.18.0"),sQuery(id+"F0.wireOp",EDGE,"E7.18.1"),sQuery(id+"F0.wireOp",EDGE,"E7.18.3"),sQuery(id+"F0.wireOp",EDGE,"E7.19.0"),sQuery(id+"F0.wireOp",EDGE,"E7.19.1"),sQuery(id+"F0.wireOp",EDGE,"E7.19.3"),sQuery(id+"F0.wireOp",EDGE,"E7.20.0"),sQuery(id+"F0.wireOp",EDGE,"E7.20.1"),sQuery(id+"F0.wireOp",EDGE,"E7.20.3"),sQuery(id+"F0.wireOp",EDGE,"E7.21.0"),sQuery(id+"F0.wireOp",EDGE,"E7.21.1"),sQuery(id+"F0.wireOp",EDGE,"E7.21.3"),sQuery(id+"F0.wireOp",EDGE,"E7.22.0"),sQuery(id+"F0.wireOp",EDGE,"E7.22.1"),sQuery(id+"F0.wireOp",EDGE,"E7.22.3"),sQuery(id+"F0.wireOp",EDGE,"E7.23.0"),sQuery(id+"F0.wireOp",EDGE,"E7.23.1"),sQuery(id+"F0.wireOp",EDGE,"E7.23.3"),sQuery(id+"F0.wireOp",EDGE,"E7.24.0"),sQuery(id+"F0.wireOp",EDGE,"E7.24.1"),sQuery(id+"F0.wireOp",EDGE,"E7.24.3"),sQuery(id+"F0.wireOp",EDGE,"E7.25.0"),sQuery(id+"F0.wireOp",EDGE,"E7.25.1"),sQuery(id+"F0.wireOp",EDGE,"E7.25.3"),sQuery(id+"F0.wireOp",EDGE,"E7.26.0"),sQuery(id+"F0.wireOp",EDGE,"E7.26.1"),sQuery(id+"F0.wireOp",EDGE,"E7.26.3"),sQuery(id+"F0.wireOp",EDGE,"E7.27.0"),sQuery(id+"F0.wireOp",EDGE,"E7.27.1"),sQuery(id+"F0.wireOp",EDGE,"E7.27.3"),sQuery(id+"F0.wireOp",EDGE,"E7.28.0"),sQuery(id+"F0.wireOp",EDGE,"E7.28.1"),sQuery(id+"F0.wireOp",EDGE,"E7.28.3"),sQuery(id+"F0.wireOp",EDGE,"E7.29.0"),sQuery(id+"F0.wireOp",EDGE,"E7.29.1"),sQuery(id+"F0.wireOp",EDGE,"E7.29.3"),sQuery(id+"F0.wireOp",EDGE,"E8"),sQuery(id+"F0.wireOp",EDGE,"E9"),sQuery(id+"F0.wireOp",EDGE,"E10"),sQuery(id+"F0.wireOp",EDGE,"E11.1.0"),sQuery(id+"F0.wireOp",EDGE,"E11.1.1"),sQuery(id+"F0.wireOp",EDGE,"E11.1.2"),sQuery(id+"F0.wireOp",EDGE,"E11.2.0"),sQuery(id+"F0.wireOp",EDGE,"E11.2.1"),sQuery(id+"F0.wireOp",EDGE,"E11.2.2"),sQuery(id+"F0.wireOp",EDGE,"E11.3.0"),sQuery(id+"F0.wireOp",EDGE,"E11.3.1"),sQuery(id+"F0.wireOp",EDGE,"E11.3.2"),sQuery(id+"F0.wireOp",EDGE,"E11.4.0"),sQuery(id+"F0.wireOp",EDGE,"E11.4.1"),sQuery(id+"F0.wireOp",EDGE,"E11.4.2"),sQuery(id+"F0.wireOp",EDGE,"E11.5.0"),sQuery(id+"F0.wireOp",EDGE,"E11.5.1"),sQuery(id+"F0.wireOp",EDGE,"E11.5.2"),sQuery(id+"F0.wireOp",EDGE,"E11.6.0"),sQuery(id+"F0.wireOp",EDGE,"E11.6.1"),sQuery(id+"F0.wireOp",EDGE,"E11.6.2"),sQuery(id+"F0.wireOp",EDGE,"E11.7.0"),sQuery(id+"F0.wireOp",EDGE,"E11.7.1"),sQuery(id+"F0.wireOp",EDGE,"E11.7.2"),sQuery(id+"F0.wireOp",EDGE,"E11.8.0"),sQuery(id+"F0.wireOp",EDGE,"E11.8.1"),sQuery(id+"F0.wireOp",EDGE,"E11.8.2"),sQuery(id+"F0.wireOp",EDGE,"E11.9.0"),sQuery(id+"F0.wireOp",EDGE,"E11.9.1"),sQuery(id+"F0.wireOp",EDGE,"E11.9.2"),sQuery(id+"F0.wireOp",EDGE,"E11.10.0"),sQuery(id+"F0.wireOp",EDGE,"E11.10.1"),sQuery(id+"F0.wireOp",EDGE,"E11.10.2"),sQuery(id+"F0.wireOp",EDGE,"E11.11.0"),sQuery(id+"F0.wireOp",EDGE,"E11.11.1"),sQuery(id+"F0.wireOp",EDGE,"E11.11.2"),sQuery(id+"F0.wireOp",EDGE,"E11.12.0"),sQuery(id+"F0.wireOp",EDGE,"E11.12.1"),sQuery(id+"F0.wireOp",EDGE,"E11.12.2"),sQuery(id+"F0.wireOp",EDGE,"E11.13.0"),sQuery(id+"F0.wireOp",EDGE,"E11.13.1"),sQuery(id+"F0.wireOp",EDGE,"E11.13.2"),sQuery(id+"F0.wireOp",EDGE,"E11.14.0"),sQuery(id+"F0.wireOp",EDGE,"E11.14.1"),sQuery(id+"F0.wireOp",EDGE,"E11.14.2"),sQuery(id+"F0.wireOp",EDGE,"E11.15.0"),sQuery(id+"F0.wireOp",EDGE,"E11.15.1"),sQuery(id+"F0.wireOp",EDGE,"E11.15.2"),sQuery(id+"F0.wireOp",EDGE,"E11.16.0"),sQuery(id+"F0.wireOp",EDGE,"E11.16.1"),sQuery(id+"F0.wireOp",EDGE,"E11.16.2"),sQuery(id+"F0.wireOp",EDGE,"E11.17.0"),sQuery(id+"F0.wireOp",EDGE,"E11.17.1"),sQuery(id+"F0.wireOp",EDGE,"E11.17.2"),sQuery(id+"F0.wireOp",EDGE,"E11.18.0"),sQuery(id+"F0.wireOp",EDGE,"E11.18.1"),sQuery(id+"F0.wireOp",EDGE,"E11.18.2"),sQuery(id+"F0.wireOp",EDGE,"E11.19.0"),sQuery(id+"F0.wireOp",EDGE,"E11.19.1"),sQuery(id+"F0.wireOp",EDGE,"E11.19.2"),sQuery(id+"F0.wireOp",EDGE,"E11.20.0"),sQuery(id+"F0.wireOp",EDGE,"E11.20.1"),sQuery(id+"F0.wireOp",EDGE,"E11.20.2"),sQuery(id+"F0.wireOp",EDGE,"E11.21.0"),sQuery(id+"F0.wireOp",EDGE,"E11.21.1"),sQuery(id+"F0.wireOp",EDGE,"E11.21.2"),sQuery(id+"F0.wireOp",EDGE,"E11.22.0"),sQuery(id+"F0.wireOp",EDGE,"E11.22.1"),sQuery(id+"F0.wireOp",EDGE,"E11.22.2"),sQuery(id+"F0.wireOp",EDGE,"E11.23.0"),sQuery(id+"F0.wireOp",EDGE,"E11.23.1"),sQuery(id+"F0.wireOp",EDGE,"E11.23.2"),sQuery(id+"F0.wireOp",EDGE,"E11.24.0"),sQuery(id+"F0.wireOp",EDGE,"E11.24.1"),sQuery(id+"F0.wireOp",EDGE,"E11.24.2"),sQuery(id+"F0.wireOp",EDGE,"E11.25.0"),sQuery(id+"F0.wireOp",EDGE,"E11.25.1"),sQuery(id+"F0.wireOp",EDGE,"E11.25.2"),sQuery(id+"F0.wireOp",EDGE,"E11.26.0"),sQuery(id+"F0.wireOp",EDGE,"E11.26.1"),sQuery(id+"F0.wireOp",EDGE,"E11.26.2"),sQuery(id+"F0.wireOp",EDGE,"E11.27.0"),sQuery(id+"F0.wireOp",EDGE,"E11.27.1"),sQuery(id+"F0.wireOp",EDGE,"E11.27.2"),sQuery(id+"F0.wireOp",EDGE,"E11.28.0"),sQuery(id+"F0.wireOp",EDGE,"E11.28.1"),sQuery(id+"F0.wireOp",EDGE,"E11.28.2"),sQuery(id+"F0.wireOp",EDGE,"E11.29.0"),sQuery(id+"F0.wireOp",EDGE,"E11.29.1"),sQuery(id+"F0.wireOp",EDGE,"E11.29.2"),sQuery(id+"F0.wireOp",EDGE,"E12"),sQuery(id+"F0.wireOp",EDGE,"E14"),sQuery(id+"F0.wireOp",EDGE,"E15.1.0"),sQuery(id+"F0.wireOp",EDGE,"E15.2.0"),sQuery(id+"F0.wireOp",EDGE,"E15.3.0"),sQuery(id+"F0.wireOp",EDGE,"E15.4.0"),sQuery(id+"F0.wireOp",EDGE,"E15.5.0"),sQuery(id+"F0.wireOp",EDGE,"E15.6.0"),sQuery(id+"F0.wireOp",EDGE,"E15.7.0"),sQuery(id+"F0.wireOp",EDGE,"E15.8.0"),sQuery(id+"F0.wireOp",EDGE,"E15.9.0"),sQuery(id+"F0.wireOp",EDGE,"E15.10.0"),sQuery(id+"F0.wireOp",EDGE,"E15.11.0"),sQuery(id+"F0.wireOp",EDGE,"E15.12.0"),sQuery(id+"F0.wireOp",EDGE,"E15.13.0"),sQuery(id+"F0.wireOp",EDGE,"E15.14.0"),sQuery(id+"F0.wireOp",EDGE,"E15.15.0"),sQuery(id+"F0.wireOp",EDGE,"E15.16.0"),sQuery(id+"F0.wireOp",EDGE,"E15.17.0"),sQuery(id+"F0.wireOp",EDGE,"E15.18.0"),sQuery(id+"F0.wireOp",EDGE,"E15.19.0"),sQuery(id+"F0.wireOp",EDGE,"E15.20.0"),sQuery(id+"F0.wireOp",EDGE,"E15.21.0"),sQuery(id+"F0.wireOp",EDGE,"E15.22.0"),sQuery(id+"F0.wireOp",EDGE,"E15.23.0"),sQuery(id+"F0.wireOp",EDGE,"E15.24.0"),sQuery(id+"F0.wireOp",EDGE,"E15.25.0"),sQuery(id+"F0.wireOp",EDGE,"E15.26.0"),sQuery(id+"F0.wireOp",EDGE,"E15.27.0"),sQuery(id+"F0.wireOp",EDGE,"E15.28.0"),sQuery(id+"F0.wireOp",EDGE,"E15.29.0")])]}),"instanceName":"1"});
            transform(context, id + "F15", {"entities" : qUnion([Q0]), "transformType" : TransformType.TRANSLATION_3D, "dx" : 0 * mm, "dy" : 8.46 * mm, "dz" : 0 * mm, "makeCopy" : true});
        }
        {
            var Q0;
            Q0=makeQuery(id+"F15.opPattern","COPY",BODY,{"derivedFrom":makeQuery(id+"F4.opPattern","COPY",BODY,{"derivedFrom":makeQuery(id+"F2.opExtrude","SWEPT_BODY",BODY,{"disambiguationData":[OSD([sQuery(id+"F0.wireOp",EDGE,"E0"),sQuery(id+"F0.wireOp",EDGE,"E2"),sQuery(id+"F0.wireOp",EDGE,"E4"),sQuery(id+"F0.wireOp",EDGE,"E5"),sQuery(id+"F0.wireOp",EDGE,"E6"),sQuery(id+"F0.wireOp",EDGE,"E7.1.0"),sQuery(id+"F0.wireOp",EDGE,"E7.1.1"),sQuery(id+"F0.wireOp",EDGE,"E7.1.3"),sQuery(id+"F0.wireOp",EDGE,"E7.2.0"),sQuery(id+"F0.wireOp",EDGE,"E7.2.1"),sQuery(id+"F0.wireOp",EDGE,"E7.2.3"),sQuery(id+"F0.wireOp",EDGE,"E7.3.0"),sQuery(id+"F0.wireOp",EDGE,"E7.3.1"),sQuery(id+"F0.wireOp",EDGE,"E7.3.3"),sQuery(id+"F0.wireOp",EDGE,"E7.4.0"),sQuery(id+"F0.wireOp",EDGE,"E7.4.1"),sQuery(id+"F0.wireOp",EDGE,"E7.4.3"),sQuery(id+"F0.wireOp",EDGE,"E7.5.0"),sQuery(id+"F0.wireOp",EDGE,"E7.5.1"),sQuery(id+"F0.wireOp",EDGE,"E7.5.3"),sQuery(id+"F0.wireOp",EDGE,"E7.6.0"),sQuery(id+"F0.wireOp",EDGE,"E7.6.1"),sQuery(id+"F0.wireOp",EDGE,"E7.6.3"),sQuery(id+"F0.wireOp",EDGE,"E7.7.0"),sQuery(id+"F0.wireOp",EDGE,"E7.7.1"),sQuery(id+"F0.wireOp",EDGE,"E7.7.3"),sQuery(id+"F0.wireOp",EDGE,"E7.8.0"),sQuery(id+"F0.wireOp",EDGE,"E7.8.1"),sQuery(id+"F0.wireOp",EDGE,"E7.8.3"),sQuery(id+"F0.wireOp",EDGE,"E7.9.0"),sQuery(id+"F0.wireOp",EDGE,"E7.9.1"),sQuery(id+"F0.wireOp",EDGE,"E7.9.3"),sQuery(id+"F0.wireOp",EDGE,"E7.10.0"),sQuery(id+"F0.wireOp",EDGE,"E7.10.1"),sQuery(id+"F0.wireOp",EDGE,"E7.10.3"),sQuery(id+"F0.wireOp",EDGE,"E7.11.0"),sQuery(id+"F0.wireOp",EDGE,"E7.11.1"),sQuery(id+"F0.wireOp",EDGE,"E7.11.3"),sQuery(id+"F0.wireOp",EDGE,"E7.12.0"),sQuery(id+"F0.wireOp",EDGE,"E7.12.1"),sQuery(id+"F0.wireOp",EDGE,"E7.12.3"),sQuery(id+"F0.wireOp",EDGE,"E7.13.0"),sQuery(id+"F0.wireOp",EDGE,"E7.13.1"),sQuery(id+"F0.wireOp",EDGE,"E7.13.3"),sQuery(id+"F0.wireOp",EDGE,"E7.14.0"),sQuery(id+"F0.wireOp",EDGE,"E7.14.1"),sQuery(id+"F0.wireOp",EDGE,"E7.14.3"),sQuery(id+"F0.wireOp",EDGE,"E7.15.0"),sQuery(id+"F0.wireOp",EDGE,"E7.15.1"),sQuery(id+"F0.wireOp",EDGE,"E7.15.3"),sQuery(id+"F0.wireOp",EDGE,"E7.16.0"),sQuery(id+"F0.wireOp",EDGE,"E7.16.1"),sQuery(id+"F0.wireOp",EDGE,"E7.16.3"),sQuery(id+"F0.wireOp",EDGE,"E7.17.0"),sQuery(id+"F0.wireOp",EDGE,"E7.17.1"),sQuery(id+"F0.wireOp",EDGE,"E7.17.3"),sQuery(id+"F0.wireOp",EDGE,"E7.18.0"),sQuery(id+"F0.wireOp",EDGE,"E7.18.1"),sQuery(id+"F0.wireOp",EDGE,"E7.18.3"),sQuery(id+"F0.wireOp",EDGE,"E7.19.0"),sQuery(id+"F0.wireOp",EDGE,"E7.19.1"),sQuery(id+"F0.wireOp",EDGE,"E7.19.3"),sQuery(id+"F0.wireOp",EDGE,"E7.20.0"),sQuery(id+"F0.wireOp",EDGE,"E7.20.1"),sQuery(id+"F0.wireOp",EDGE,"E7.20.3"),sQuery(id+"F0.wireOp",EDGE,"E7.21.0"),sQuery(id+"F0.wireOp",EDGE,"E7.21.1"),sQuery(id+"F0.wireOp",EDGE,"E7.21.3"),sQuery(id+"F0.wireOp",EDGE,"E7.22.0"),sQuery(id+"F0.wireOp",EDGE,"E7.22.1"),sQuery(id+"F0.wireOp",EDGE,"E7.22.3"),sQuery(id+"F0.wireOp",EDGE,"E7.23.0"),sQuery(id+"F0.wireOp",EDGE,"E7.23.1"),sQuery(id+"F0.wireOp",EDGE,"E7.23.3"),sQuery(id+"F0.wireOp",EDGE,"E7.24.0"),sQuery(id+"F0.wireOp",EDGE,"E7.24.1"),sQuery(id+"F0.wireOp",EDGE,"E7.24.3"),sQuery(id+"F0.wireOp",EDGE,"E7.25.0"),sQuery(id+"F0.wireOp",EDGE,"E7.25.1"),sQuery(id+"F0.wireOp",EDGE,"E7.25.3"),sQuery(id+"F0.wireOp",EDGE,"E7.26.0"),sQuery(id+"F0.wireOp",EDGE,"E7.26.1"),sQuery(id+"F0.wireOp",EDGE,"E7.26.3"),sQuery(id+"F0.wireOp",EDGE,"E7.27.0"),sQuery(id+"F0.wireOp",EDGE,"E7.27.1"),sQuery(id+"F0.wireOp",EDGE,"E7.27.3"),sQuery(id+"F0.wireOp",EDGE,"E7.28.0"),sQuery(id+"F0.wireOp",EDGE,"E7.28.1"),sQuery(id+"F0.wireOp",EDGE,"E7.28.3"),sQuery(id+"F0.wireOp",EDGE,"E7.29.0"),sQuery(id+"F0.wireOp",EDGE,"E7.29.1"),sQuery(id+"F0.wireOp",EDGE,"E7.29.3"),sQuery(id+"F0.wireOp",EDGE,"E8"),sQuery(id+"F0.wireOp",EDGE,"E9"),sQuery(id+"F0.wireOp",EDGE,"E10"),sQuery(id+"F0.wireOp",EDGE,"E11.1.0"),sQuery(id+"F0.wireOp",EDGE,"E11.1.1"),sQuery(id+"F0.wireOp",EDGE,"E11.1.2"),sQuery(id+"F0.wireOp",EDGE,"E11.2.0"),sQuery(id+"F0.wireOp",EDGE,"E11.2.1"),sQuery(id+"F0.wireOp",EDGE,"E11.2.2"),sQuery(id+"F0.wireOp",EDGE,"E11.3.0"),sQuery(id+"F0.wireOp",EDGE,"E11.3.1"),sQuery(id+"F0.wireOp",EDGE,"E11.3.2"),sQuery(id+"F0.wireOp",EDGE,"E11.4.0"),sQuery(id+"F0.wireOp",EDGE,"E11.4.1"),sQuery(id+"F0.wireOp",EDGE,"E11.4.2"),sQuery(id+"F0.wireOp",EDGE,"E11.5.0"),sQuery(id+"F0.wireOp",EDGE,"E11.5.1"),sQuery(id+"F0.wireOp",EDGE,"E11.5.2"),sQuery(id+"F0.wireOp",EDGE,"E11.6.0"),sQuery(id+"F0.wireOp",EDGE,"E11.6.1"),sQuery(id+"F0.wireOp",EDGE,"E11.6.2"),sQuery(id+"F0.wireOp",EDGE,"E11.7.0"),sQuery(id+"F0.wireOp",EDGE,"E11.7.1"),sQuery(id+"F0.wireOp",EDGE,"E11.7.2"),sQuery(id+"F0.wireOp",EDGE,"E11.8.0"),sQuery(id+"F0.wireOp",EDGE,"E11.8.1"),sQuery(id+"F0.wireOp",EDGE,"E11.8.2"),sQuery(id+"F0.wireOp",EDGE,"E11.9.0"),sQuery(id+"F0.wireOp",EDGE,"E11.9.1"),sQuery(id+"F0.wireOp",EDGE,"E11.9.2"),sQuery(id+"F0.wireOp",EDGE,"E11.10.0"),sQuery(id+"F0.wireOp",EDGE,"E11.10.1"),sQuery(id+"F0.wireOp",EDGE,"E11.10.2"),sQuery(id+"F0.wireOp",EDGE,"E11.11.0"),sQuery(id+"F0.wireOp",EDGE,"E11.11.1"),sQuery(id+"F0.wireOp",EDGE,"E11.11.2"),sQuery(id+"F0.wireOp",EDGE,"E11.12.0"),sQuery(id+"F0.wireOp",EDGE,"E11.12.1"),sQuery(id+"F0.wireOp",EDGE,"E11.12.2"),sQuery(id+"F0.wireOp",EDGE,"E11.13.0"),sQuery(id+"F0.wireOp",EDGE,"E11.13.1"),sQuery(id+"F0.wireOp",EDGE,"E11.13.2"),sQuery(id+"F0.wireOp",EDGE,"E11.14.0"),sQuery(id+"F0.wireOp",EDGE,"E11.14.1"),sQuery(id+"F0.wireOp",EDGE,"E11.14.2"),sQuery(id+"F0.wireOp",EDGE,"E11.15.0"),sQuery(id+"F0.wireOp",EDGE,"E11.15.1"),sQuery(id+"F0.wireOp",EDGE,"E11.15.2"),sQuery(id+"F0.wireOp",EDGE,"E11.16.0"),sQuery(id+"F0.wireOp",EDGE,"E11.16.1"),sQuery(id+"F0.wireOp",EDGE,"E11.16.2"),sQuery(id+"F0.wireOp",EDGE,"E11.17.0"),sQuery(id+"F0.wireOp",EDGE,"E11.17.1"),sQuery(id+"F0.wireOp",EDGE,"E11.17.2"),sQuery(id+"F0.wireOp",EDGE,"E11.18.0"),sQuery(id+"F0.wireOp",EDGE,"E11.18.1"),sQuery(id+"F0.wireOp",EDGE,"E11.18.2"),sQuery(id+"F0.wireOp",EDGE,"E11.19.0"),sQuery(id+"F0.wireOp",EDGE,"E11.19.1"),sQuery(id+"F0.wireOp",EDGE,"E11.19.2"),sQuery(id+"F0.wireOp",EDGE,"E11.20.0"),sQuery(id+"F0.wireOp",EDGE,"E11.20.1"),sQuery(id+"F0.wireOp",EDGE,"E11.20.2"),sQuery(id+"F0.wireOp",EDGE,"E11.21.0"),sQuery(id+"F0.wireOp",EDGE,"E11.21.1"),sQuery(id+"F0.wireOp",EDGE,"E11.21.2"),sQuery(id+"F0.wireOp",EDGE,"E11.22.0"),sQuery(id+"F0.wireOp",EDGE,"E11.22.1"),sQuery(id+"F0.wireOp",EDGE,"E11.22.2"),sQuery(id+"F0.wireOp",EDGE,"E11.23.0"),sQuery(id+"F0.wireOp",EDGE,"E11.23.1"),sQuery(id+"F0.wireOp",EDGE,"E11.23.2"),sQuery(id+"F0.wireOp",EDGE,"E11.24.0"),sQuery(id+"F0.wireOp",EDGE,"E11.24.1"),sQuery(id+"F0.wireOp",EDGE,"E11.24.2"),sQuery(id+"F0.wireOp",EDGE,"E11.25.0"),sQuery(id+"F0.wireOp",EDGE,"E11.25.1"),sQuery(id+"F0.wireOp",EDGE,"E11.25.2"),sQuery(id+"F0.wireOp",EDGE,"E11.26.0"),sQuery(id+"F0.wireOp",EDGE,"E11.26.1"),sQuery(id+"F0.wireOp",EDGE,"E11.26.2"),sQuery(id+"F0.wireOp",EDGE,"E11.27.0"),sQuery(id+"F0.wireOp",EDGE,"E11.27.1"),sQuery(id+"F0.wireOp",EDGE,"E11.27.2"),sQuery(id+"F0.wireOp",EDGE,"E11.28.0"),sQuery(id+"F0.wireOp",EDGE,"E11.28.1"),sQuery(id+"F0.wireOp",EDGE,"E11.28.2"),sQuery(id+"F0.wireOp",EDGE,"E11.29.0"),sQuery(id+"F0.wireOp",EDGE,"E11.29.1"),sQuery(id+"F0.wireOp",EDGE,"E11.29.2"),sQuery(id+"F0.wireOp",EDGE,"E12"),sQuery(id+"F0.wireOp",EDGE,"E14"),sQuery(id+"F0.wireOp",EDGE,"E15.1.0"),sQuery(id+"F0.wireOp",EDGE,"E15.2.0"),sQuery(id+"F0.wireOp",EDGE,"E15.3.0"),sQuery(id+"F0.wireOp",EDGE,"E15.4.0"),sQuery(id+"F0.wireOp",EDGE,"E15.5.0"),sQuery(id+"F0.wireOp",EDGE,"E15.6.0"),sQuery(id+"F0.wireOp",EDGE,"E15.7.0"),sQuery(id+"F0.wireOp",EDGE,"E15.8.0"),sQuery(id+"F0.wireOp",EDGE,"E15.9.0"),sQuery(id+"F0.wireOp",EDGE,"E15.10.0"),sQuery(id+"F0.wireOp",EDGE,"E15.11.0"),sQuery(id+"F0.wireOp",EDGE,"E15.12.0"),sQuery(id+"F0.wireOp",EDGE,"E15.13.0"),sQuery(id+"F0.wireOp",EDGE,"E15.14.0"),sQuery(id+"F0.wireOp",EDGE,"E15.15.0"),sQuery(id+"F0.wireOp",EDGE,"E15.16.0"),sQuery(id+"F0.wireOp",EDGE,"E15.17.0"),sQuery(id+"F0.wireOp",EDGE,"E15.18.0"),sQuery(id+"F0.wireOp",EDGE,"E15.19.0"),sQuery(id+"F0.wireOp",EDGE,"E15.20.0"),sQuery(id+"F0.wireOp",EDGE,"E15.21.0"),sQuery(id+"F0.wireOp",EDGE,"E15.22.0"),sQuery(id+"F0.wireOp",EDGE,"E15.23.0"),sQuery(id+"F0.wireOp",EDGE,"E15.24.0"),sQuery(id+"F0.wireOp",EDGE,"E15.25.0"),sQuery(id+"F0.wireOp",EDGE,"E15.26.0"),sQuery(id+"F0.wireOp",EDGE,"E15.27.0"),sQuery(id+"F0.wireOp",EDGE,"E15.28.0"),sQuery(id+"F0.wireOp",EDGE,"E15.29.0")])]}),"instanceName":"1"}),"instanceName":"1"});
            var Q1;
            Q1=makeQuery(id+"F15.opPattern","COPY",EDGE,{"derivedFrom":makeQuery(id+"F4.opPattern","COPY",EDGE,{"derivedFrom":makeQuery(id+"F2.opExtrude","CAP_EDGE",EDGE,{"disambiguationData":[OSD([sQuery(id+"F0.wireOp",EDGE,"E0")])],"isStart":true}),"instanceName":"1"}),"instanceName":"1"});
            transform(context, id + "F16", {"entities" : qUnion([Q0]), "transformType" : TransformType.ROTATION, "transformAxis" : qUnion([Q1]), "angle" : 4 * degree, "oppositeDirection" : true, "makeCopy" : false});
        }
        {
            var Q0;
            Q0=makeQuery(id+"F15.opPattern","COPY",BODY,{"derivedFrom":makeQuery(id+"F4.opPattern","COPY",BODY,{"derivedFrom":makeQuery(id+"F2.opExtrude","SWEPT_BODY",BODY,{"disambiguationData":[OSD([sQuery(id+"F0.wireOp",EDGE,"E0"),sQuery(id+"F0.wireOp",EDGE,"E2"),sQuery(id+"F0.wireOp",EDGE,"E4"),sQuery(id+"F0.wireOp",EDGE,"E5"),sQuery(id+"F0.wireOp",EDGE,"E6"),sQuery(id+"F0.wireOp",EDGE,"E7.1.0"),sQuery(id+"F0.wireOp",EDGE,"E7.1.1"),sQuery(id+"F0.wireOp",EDGE,"E7.1.3"),sQuery(id+"F0.wireOp",EDGE,"E7.2.0"),sQuery(id+"F0.wireOp",EDGE,"E7.2.1"),sQuery(id+"F0.wireOp",EDGE,"E7.2.3"),sQuery(id+"F0.wireOp",EDGE,"E7.3.0"),sQuery(id+"F0.wireOp",EDGE,"E7.3.1"),sQuery(id+"F0.wireOp",EDGE,"E7.3.3"),sQuery(id+"F0.wireOp",EDGE,"E7.4.0"),sQuery(id+"F0.wireOp",EDGE,"E7.4.1"),sQuery(id+"F0.wireOp",EDGE,"E7.4.3"),sQuery(id+"F0.wireOp",EDGE,"E7.5.0"),sQuery(id+"F0.wireOp",EDGE,"E7.5.1"),sQuery(id+"F0.wireOp",EDGE,"E7.5.3"),sQuery(id+"F0.wireOp",EDGE,"E7.6.0"),sQuery(id+"F0.wireOp",EDGE,"E7.6.1"),sQuery(id+"F0.wireOp",EDGE,"E7.6.3"),sQuery(id+"F0.wireOp",EDGE,"E7.7.0"),sQuery(id+"F0.wireOp",EDGE,"E7.7.1"),sQuery(id+"F0.wireOp",EDGE,"E7.7.3"),sQuery(id+"F0.wireOp",EDGE,"E7.8.0"),sQuery(id+"F0.wireOp",EDGE,"E7.8.1"),sQuery(id+"F0.wireOp",EDGE,"E7.8.3"),sQuery(id+"F0.wireOp",EDGE,"E7.9.0"),sQuery(id+"F0.wireOp",EDGE,"E7.9.1"),sQuery(id+"F0.wireOp",EDGE,"E7.9.3"),sQuery(id+"F0.wireOp",EDGE,"E7.10.0"),sQuery(id+"F0.wireOp",EDGE,"E7.10.1"),sQuery(id+"F0.wireOp",EDGE,"E7.10.3"),sQuery(id+"F0.wireOp",EDGE,"E7.11.0"),sQuery(id+"F0.wireOp",EDGE,"E7.11.1"),sQuery(id+"F0.wireOp",EDGE,"E7.11.3"),sQuery(id+"F0.wireOp",EDGE,"E7.12.0"),sQuery(id+"F0.wireOp",EDGE,"E7.12.1"),sQuery(id+"F0.wireOp",EDGE,"E7.12.3"),sQuery(id+"F0.wireOp",EDGE,"E7.13.0"),sQuery(id+"F0.wireOp",EDGE,"E7.13.1"),sQuery(id+"F0.wireOp",EDGE,"E7.13.3"),sQuery(id+"F0.wireOp",EDGE,"E7.14.0"),sQuery(id+"F0.wireOp",EDGE,"E7.14.1"),sQuery(id+"F0.wireOp",EDGE,"E7.14.3"),sQuery(id+"F0.wireOp",EDGE,"E7.15.0"),sQuery(id+"F0.wireOp",EDGE,"E7.15.1"),sQuery(id+"F0.wireOp",EDGE,"E7.15.3"),sQuery(id+"F0.wireOp",EDGE,"E7.16.0"),sQuery(id+"F0.wireOp",EDGE,"E7.16.1"),sQuery(id+"F0.wireOp",EDGE,"E7.16.3"),sQuery(id+"F0.wireOp",EDGE,"E7.17.0"),sQuery(id+"F0.wireOp",EDGE,"E7.17.1"),sQuery(id+"F0.wireOp",EDGE,"E7.17.3"),sQuery(id+"F0.wireOp",EDGE,"E7.18.0"),sQuery(id+"F0.wireOp",EDGE,"E7.18.1"),sQuery(id+"F0.wireOp",EDGE,"E7.18.3"),sQuery(id+"F0.wireOp",EDGE,"E7.19.0"),sQuery(id+"F0.wireOp",EDGE,"E7.19.1"),sQuery(id+"F0.wireOp",EDGE,"E7.19.3"),sQuery(id+"F0.wireOp",EDGE,"E7.20.0"),sQuery(id+"F0.wireOp",EDGE,"E7.20.1"),sQuery(id+"F0.wireOp",EDGE,"E7.20.3"),sQuery(id+"F0.wireOp",EDGE,"E7.21.0"),sQuery(id+"F0.wireOp",EDGE,"E7.21.1"),sQuery(id+"F0.wireOp",EDGE,"E7.21.3"),sQuery(id+"F0.wireOp",EDGE,"E7.22.0"),sQuery(id+"F0.wireOp",EDGE,"E7.22.1"),sQuery(id+"F0.wireOp",EDGE,"E7.22.3"),sQuery(id+"F0.wireOp",EDGE,"E7.23.0"),sQuery(id+"F0.wireOp",EDGE,"E7.23.1"),sQuery(id+"F0.wireOp",EDGE,"E7.23.3"),sQuery(id+"F0.wireOp",EDGE,"E7.24.0"),sQuery(id+"F0.wireOp",EDGE,"E7.24.1"),sQuery(id+"F0.wireOp",EDGE,"E7.24.3"),sQuery(id+"F0.wireOp",EDGE,"E7.25.0"),sQuery(id+"F0.wireOp",EDGE,"E7.25.1"),sQuery(id+"F0.wireOp",EDGE,"E7.25.3"),sQuery(id+"F0.wireOp",EDGE,"E7.26.0"),sQuery(id+"F0.wireOp",EDGE,"E7.26.1"),sQuery(id+"F0.wireOp",EDGE,"E7.26.3"),sQuery(id+"F0.wireOp",EDGE,"E7.27.0"),sQuery(id+"F0.wireOp",EDGE,"E7.27.1"),sQuery(id+"F0.wireOp",EDGE,"E7.27.3"),sQuery(id+"F0.wireOp",EDGE,"E7.28.0"),sQuery(id+"F0.wireOp",EDGE,"E7.28.1"),sQuery(id+"F0.wireOp",EDGE,"E7.28.3"),sQuery(id+"F0.wireOp",EDGE,"E7.29.0"),sQuery(id+"F0.wireOp",EDGE,"E7.29.1"),sQuery(id+"F0.wireOp",EDGE,"E7.29.3"),sQuery(id+"F0.wireOp",EDGE,"E8"),sQuery(id+"F0.wireOp",EDGE,"E9"),sQuery(id+"F0.wireOp",EDGE,"E10"),sQuery(id+"F0.wireOp",EDGE,"E11.1.0"),sQuery(id+"F0.wireOp",EDGE,"E11.1.1"),sQuery(id+"F0.wireOp",EDGE,"E11.1.2"),sQuery(id+"F0.wireOp",EDGE,"E11.2.0"),sQuery(id+"F0.wireOp",EDGE,"E11.2.1"),sQuery(id+"F0.wireOp",EDGE,"E11.2.2"),sQuery(id+"F0.wireOp",EDGE,"E11.3.0"),sQuery(id+"F0.wireOp",EDGE,"E11.3.1"),sQuery(id+"F0.wireOp",EDGE,"E11.3.2"),sQuery(id+"F0.wireOp",EDGE,"E11.4.0"),sQuery(id+"F0.wireOp",EDGE,"E11.4.1"),sQuery(id+"F0.wireOp",EDGE,"E11.4.2"),sQuery(id+"F0.wireOp",EDGE,"E11.5.0"),sQuery(id+"F0.wireOp",EDGE,"E11.5.1"),sQuery(id+"F0.wireOp",EDGE,"E11.5.2"),sQuery(id+"F0.wireOp",EDGE,"E11.6.0"),sQuery(id+"F0.wireOp",EDGE,"E11.6.1"),sQuery(id+"F0.wireOp",EDGE,"E11.6.2"),sQuery(id+"F0.wireOp",EDGE,"E11.7.0"),sQuery(id+"F0.wireOp",EDGE,"E11.7.1"),sQuery(id+"F0.wireOp",EDGE,"E11.7.2"),sQuery(id+"F0.wireOp",EDGE,"E11.8.0"),sQuery(id+"F0.wireOp",EDGE,"E11.8.1"),sQuery(id+"F0.wireOp",EDGE,"E11.8.2"),sQuery(id+"F0.wireOp",EDGE,"E11.9.0"),sQuery(id+"F0.wireOp",EDGE,"E11.9.1"),sQuery(id+"F0.wireOp",EDGE,"E11.9.2"),sQuery(id+"F0.wireOp",EDGE,"E11.10.0"),sQuery(id+"F0.wireOp",EDGE,"E11.10.1"),sQuery(id+"F0.wireOp",EDGE,"E11.10.2"),sQuery(id+"F0.wireOp",EDGE,"E11.11.0"),sQuery(id+"F0.wireOp",EDGE,"E11.11.1"),sQuery(id+"F0.wireOp",EDGE,"E11.11.2"),sQuery(id+"F0.wireOp",EDGE,"E11.12.0"),sQuery(id+"F0.wireOp",EDGE,"E11.12.1"),sQuery(id+"F0.wireOp",EDGE,"E11.12.2"),sQuery(id+"F0.wireOp",EDGE,"E11.13.0"),sQuery(id+"F0.wireOp",EDGE,"E11.13.1"),sQuery(id+"F0.wireOp",EDGE,"E11.13.2"),sQuery(id+"F0.wireOp",EDGE,"E11.14.0"),sQuery(id+"F0.wireOp",EDGE,"E11.14.1"),sQuery(id+"F0.wireOp",EDGE,"E11.14.2"),sQuery(id+"F0.wireOp",EDGE,"E11.15.0"),sQuery(id+"F0.wireOp",EDGE,"E11.15.1"),sQuery(id+"F0.wireOp",EDGE,"E11.15.2"),sQuery(id+"F0.wireOp",EDGE,"E11.16.0"),sQuery(id+"F0.wireOp",EDGE,"E11.16.1"),sQuery(id+"F0.wireOp",EDGE,"E11.16.2"),sQuery(id+"F0.wireOp",EDGE,"E11.17.0"),sQuery(id+"F0.wireOp",EDGE,"E11.17.1"),sQuery(id+"F0.wireOp",EDGE,"E11.17.2"),sQuery(id+"F0.wireOp",EDGE,"E11.18.0"),sQuery(id+"F0.wireOp",EDGE,"E11.18.1"),sQuery(id+"F0.wireOp",EDGE,"E11.18.2"),sQuery(id+"F0.wireOp",EDGE,"E11.19.0"),sQuery(id+"F0.wireOp",EDGE,"E11.19.1"),sQuery(id+"F0.wireOp",EDGE,"E11.19.2"),sQuery(id+"F0.wireOp",EDGE,"E11.20.0"),sQuery(id+"F0.wireOp",EDGE,"E11.20.1"),sQuery(id+"F0.wireOp",EDGE,"E11.20.2"),sQuery(id+"F0.wireOp",EDGE,"E11.21.0"),sQuery(id+"F0.wireOp",EDGE,"E11.21.1"),sQuery(id+"F0.wireOp",EDGE,"E11.21.2"),sQuery(id+"F0.wireOp",EDGE,"E11.22.0"),sQuery(id+"F0.wireOp",EDGE,"E11.22.1"),sQuery(id+"F0.wireOp",EDGE,"E11.22.2"),sQuery(id+"F0.wireOp",EDGE,"E11.23.0"),sQuery(id+"F0.wireOp",EDGE,"E11.23.1"),sQuery(id+"F0.wireOp",EDGE,"E11.23.2"),sQuery(id+"F0.wireOp",EDGE,"E11.24.0"),sQuery(id+"F0.wireOp",EDGE,"E11.24.1"),sQuery(id+"F0.wireOp",EDGE,"E11.24.2"),sQuery(id+"F0.wireOp",EDGE,"E11.25.0"),sQuery(id+"F0.wireOp",EDGE,"E11.25.1"),sQuery(id+"F0.wireOp",EDGE,"E11.25.2"),sQuery(id+"F0.wireOp",EDGE,"E11.26.0"),sQuery(id+"F0.wireOp",EDGE,"E11.26.1"),sQuery(id+"F0.wireOp",EDGE,"E11.26.2"),sQuery(id+"F0.wireOp",EDGE,"E11.27.0"),sQuery(id+"F0.wireOp",EDGE,"E11.27.1"),sQuery(id+"F0.wireOp",EDGE,"E11.27.2"),sQuery(id+"F0.wireOp",EDGE,"E11.28.0"),sQuery(id+"F0.wireOp",EDGE,"E11.28.1"),sQuery(id+"F0.wireOp",EDGE,"E11.28.2"),sQuery(id+"F0.wireOp",EDGE,"E11.29.0"),sQuery(id+"F0.wireOp",EDGE,"E11.29.1"),sQuery(id+"F0.wireOp",EDGE,"E11.29.2"),sQuery(id+"F0.wireOp",EDGE,"E12"),sQuery(id+"F0.wireOp",EDGE,"E14"),sQuery(id+"F0.wireOp",EDGE,"E15.1.0"),sQuery(id+"F0.wireOp",EDGE,"E15.2.0"),sQuery(id+"F0.wireOp",EDGE,"E15.3.0"),sQuery(id+"F0.wireOp",EDGE,"E15.4.0"),sQuery(id+"F0.wireOp",EDGE,"E15.5.0"),sQuery(id+"F0.wireOp",EDGE,"E15.6.0"),sQuery(id+"F0.wireOp",EDGE,"E15.7.0"),sQuery(id+"F0.wireOp",EDGE,"E15.8.0"),sQuery(id+"F0.wireOp",EDGE,"E15.9.0"),sQuery(id+"F0.wireOp",EDGE,"E15.10.0"),sQuery(id+"F0.wireOp",EDGE,"E15.11.0"),sQuery(id+"F0.wireOp",EDGE,"E15.12.0"),sQuery(id+"F0.wireOp",EDGE,"E15.13.0"),sQuery(id+"F0.wireOp",EDGE,"E15.14.0"),sQuery(id+"F0.wireOp",EDGE,"E15.15.0"),sQuery(id+"F0.wireOp",EDGE,"E15.16.0"),sQuery(id+"F0.wireOp",EDGE,"E15.17.0"),sQuery(id+"F0.wireOp",EDGE,"E15.18.0"),sQuery(id+"F0.wireOp",EDGE,"E15.19.0"),sQuery(id+"F0.wireOp",EDGE,"E15.20.0"),sQuery(id+"F0.wireOp",EDGE,"E15.21.0"),sQuery(id+"F0.wireOp",EDGE,"E15.22.0"),sQuery(id+"F0.wireOp",EDGE,"E15.23.0"),sQuery(id+"F0.wireOp",EDGE,"E15.24.0"),sQuery(id+"F0.wireOp",EDGE,"E15.25.0"),sQuery(id+"F0.wireOp",EDGE,"E15.26.0"),sQuery(id+"F0.wireOp",EDGE,"E15.27.0"),sQuery(id+"F0.wireOp",EDGE,"E15.28.0"),sQuery(id+"F0.wireOp",EDGE,"E15.29.0")])]}),"instanceName":"1"}),"instanceName":"1"});
            transform(context, id + "F17", {"entities" : qUnion([Q0]), "transformType" : TransformType.TRANSLATION_3D, "dx" : 0 * mm, "dy" : 8.46 * mm, "dz" : 0 * mm, "makeCopy" : true});
        }
        {
            var Q0;
            Q0=makeQuery(id+"F17.opPattern","COPY",BODY,{"derivedFrom":makeQuery(id+"F15.opPattern","COPY",BODY,{"derivedFrom":makeQuery(id+"F4.opPattern","COPY",BODY,{"derivedFrom":makeQuery(id+"F2.opExtrude","SWEPT_BODY",BODY,{"disambiguationData":[OSD([sQuery(id+"F0.wireOp",EDGE,"E0"),sQuery(id+"F0.wireOp",EDGE,"E2"),sQuery(id+"F0.wireOp",EDGE,"E4"),sQuery(id+"F0.wireOp",EDGE,"E5"),sQuery(id+"F0.wireOp",EDGE,"E6"),sQuery(id+"F0.wireOp",EDGE,"E7.1.0"),sQuery(id+"F0.wireOp",EDGE,"E7.1.1"),sQuery(id+"F0.wireOp",EDGE,"E7.1.3"),sQuery(id+"F0.wireOp",EDGE,"E7.2.0"),sQuery(id+"F0.wireOp",EDGE,"E7.2.1"),sQuery(id+"F0.wireOp",EDGE,"E7.2.3"),sQuery(id+"F0.wireOp",EDGE,"E7.3.0"),sQuery(id+"F0.wireOp",EDGE,"E7.3.1"),sQuery(id+"F0.wireOp",EDGE,"E7.3.3"),sQuery(id+"F0.wireOp",EDGE,"E7.4.0"),sQuery(id+"F0.wireOp",EDGE,"E7.4.1"),sQuery(id+"F0.wireOp",EDGE,"E7.4.3"),sQuery(id+"F0.wireOp",EDGE,"E7.5.0"),sQuery(id+"F0.wireOp",EDGE,"E7.5.1"),sQuery(id+"F0.wireOp",EDGE,"E7.5.3"),sQuery(id+"F0.wireOp",EDGE,"E7.6.0"),sQuery(id+"F0.wireOp",EDGE,"E7.6.1"),sQuery(id+"F0.wireOp",EDGE,"E7.6.3"),sQuery(id+"F0.wireOp",EDGE,"E7.7.0"),sQuery(id+"F0.wireOp",EDGE,"E7.7.1"),sQuery(id+"F0.wireOp",EDGE,"E7.7.3"),sQuery(id+"F0.wireOp",EDGE,"E7.8.0"),sQuery(id+"F0.wireOp",EDGE,"E7.8.1"),sQuery(id+"F0.wireOp",EDGE,"E7.8.3"),sQuery(id+"F0.wireOp",EDGE,"E7.9.0"),sQuery(id+"F0.wireOp",EDGE,"E7.9.1"),sQuery(id+"F0.wireOp",EDGE,"E7.9.3"),sQuery(id+"F0.wireOp",EDGE,"E7.10.0"),sQuery(id+"F0.wireOp",EDGE,"E7.10.1"),sQuery(id+"F0.wireOp",EDGE,"E7.10.3"),sQuery(id+"F0.wireOp",EDGE,"E7.11.0"),sQuery(id+"F0.wireOp",EDGE,"E7.11.1"),sQuery(id+"F0.wireOp",EDGE,"E7.11.3"),sQuery(id+"F0.wireOp",EDGE,"E7.12.0"),sQuery(id+"F0.wireOp",EDGE,"E7.12.1"),sQuery(id+"F0.wireOp",EDGE,"E7.12.3"),sQuery(id+"F0.wireOp",EDGE,"E7.13.0"),sQuery(id+"F0.wireOp",EDGE,"E7.13.1"),sQuery(id+"F0.wireOp",EDGE,"E7.13.3"),sQuery(id+"F0.wireOp",EDGE,"E7.14.0"),sQuery(id+"F0.wireOp",EDGE,"E7.14.1"),sQuery(id+"F0.wireOp",EDGE,"E7.14.3"),sQuery(id+"F0.wireOp",EDGE,"E7.15.0"),sQuery(id+"F0.wireOp",EDGE,"E7.15.1"),sQuery(id+"F0.wireOp",EDGE,"E7.15.3"),sQuery(id+"F0.wireOp",EDGE,"E7.16.0"),sQuery(id+"F0.wireOp",EDGE,"E7.16.1"),sQuery(id+"F0.wireOp",EDGE,"E7.16.3"),sQuery(id+"F0.wireOp",EDGE,"E7.17.0"),sQuery(id+"F0.wireOp",EDGE,"E7.17.1"),sQuery(id+"F0.wireOp",EDGE,"E7.17.3"),sQuery(id+"F0.wireOp",EDGE,"E7.18.0"),sQuery(id+"F0.wireOp",EDGE,"E7.18.1"),sQuery(id+"F0.wireOp",EDGE,"E7.18.3"),sQuery(id+"F0.wireOp",EDGE,"E7.19.0"),sQuery(id+"F0.wireOp",EDGE,"E7.19.1"),sQuery(id+"F0.wireOp",EDGE,"E7.19.3"),sQuery(id+"F0.wireOp",EDGE,"E7.20.0"),sQuery(id+"F0.wireOp",EDGE,"E7.20.1"),sQuery(id+"F0.wireOp",EDGE,"E7.20.3"),sQuery(id+"F0.wireOp",EDGE,"E7.21.0"),sQuery(id+"F0.wireOp",EDGE,"E7.21.1"),sQuery(id+"F0.wireOp",EDGE,"E7.21.3"),sQuery(id+"F0.wireOp",EDGE,"E7.22.0"),sQuery(id+"F0.wireOp",EDGE,"E7.22.1"),sQuery(id+"F0.wireOp",EDGE,"E7.22.3"),sQuery(id+"F0.wireOp",EDGE,"E7.23.0"),sQuery(id+"F0.wireOp",EDGE,"E7.23.1"),sQuery(id+"F0.wireOp",EDGE,"E7.23.3"),sQuery(id+"F0.wireOp",EDGE,"E7.24.0"),sQuery(id+"F0.wireOp",EDGE,"E7.24.1"),sQuery(id+"F0.wireOp",EDGE,"E7.24.3"),sQuery(id+"F0.wireOp",EDGE,"E7.25.0"),sQuery(id+"F0.wireOp",EDGE,"E7.25.1"),sQuery(id+"F0.wireOp",EDGE,"E7.25.3"),sQuery(id+"F0.wireOp",EDGE,"E7.26.0"),sQuery(id+"F0.wireOp",EDGE,"E7.26.1"),sQuery(id+"F0.wireOp",EDGE,"E7.26.3"),sQuery(id+"F0.wireOp",EDGE,"E7.27.0"),sQuery(id+"F0.wireOp",EDGE,"E7.27.1"),sQuery(id+"F0.wireOp",EDGE,"E7.27.3"),sQuery(id+"F0.wireOp",EDGE,"E7.28.0"),sQuery(id+"F0.wireOp",EDGE,"E7.28.1"),sQuery(id+"F0.wireOp",EDGE,"E7.28.3"),sQuery(id+"F0.wireOp",EDGE,"E7.29.0"),sQuery(id+"F0.wireOp",EDGE,"E7.29.1"),sQuery(id+"F0.wireOp",EDGE,"E7.29.3"),sQuery(id+"F0.wireOp",EDGE,"E8"),sQuery(id+"F0.wireOp",EDGE,"E9"),sQuery(id+"F0.wireOp",EDGE,"E10"),sQuery(id+"F0.wireOp",EDGE,"E11.1.0"),sQuery(id+"F0.wireOp",EDGE,"E11.1.1"),sQuery(id+"F0.wireOp",EDGE,"E11.1.2"),sQuery(id+"F0.wireOp",EDGE,"E11.2.0"),sQuery(id+"F0.wireOp",EDGE,"E11.2.1"),sQuery(id+"F0.wireOp",EDGE,"E11.2.2"),sQuery(id+"F0.wireOp",EDGE,"E11.3.0"),sQuery(id+"F0.wireOp",EDGE,"E11.3.1"),sQuery(id+"F0.wireOp",EDGE,"E11.3.2"),sQuery(id+"F0.wireOp",EDGE,"E11.4.0"),sQuery(id+"F0.wireOp",EDGE,"E11.4.1"),sQuery(id+"F0.wireOp",EDGE,"E11.4.2"),sQuery(id+"F0.wireOp",EDGE,"E11.5.0"),sQuery(id+"F0.wireOp",EDGE,"E11.5.1"),sQuery(id+"F0.wireOp",EDGE,"E11.5.2"),sQuery(id+"F0.wireOp",EDGE,"E11.6.0"),sQuery(id+"F0.wireOp",EDGE,"E11.6.1"),sQuery(id+"F0.wireOp",EDGE,"E11.6.2"),sQuery(id+"F0.wireOp",EDGE,"E11.7.0"),sQuery(id+"F0.wireOp",EDGE,"E11.7.1"),sQuery(id+"F0.wireOp",EDGE,"E11.7.2"),sQuery(id+"F0.wireOp",EDGE,"E11.8.0"),sQuery(id+"F0.wireOp",EDGE,"E11.8.1"),sQuery(id+"F0.wireOp",EDGE,"E11.8.2"),sQuery(id+"F0.wireOp",EDGE,"E11.9.0"),sQuery(id+"F0.wireOp",EDGE,"E11.9.1"),sQuery(id+"F0.wireOp",EDGE,"E11.9.2"),sQuery(id+"F0.wireOp",EDGE,"E11.10.0"),sQuery(id+"F0.wireOp",EDGE,"E11.10.1"),sQuery(id+"F0.wireOp",EDGE,"E11.10.2"),sQuery(id+"F0.wireOp",EDGE,"E11.11.0"),sQuery(id+"F0.wireOp",EDGE,"E11.11.1"),sQuery(id+"F0.wireOp",EDGE,"E11.11.2"),sQuery(id+"F0.wireOp",EDGE,"E11.12.0"),sQuery(id+"F0.wireOp",EDGE,"E11.12.1"),sQuery(id+"F0.wireOp",EDGE,"E11.12.2"),sQuery(id+"F0.wireOp",EDGE,"E11.13.0"),sQuery(id+"F0.wireOp",EDGE,"E11.13.1"),sQuery(id+"F0.wireOp",EDGE,"E11.13.2"),sQuery(id+"F0.wireOp",EDGE,"E11.14.0"),sQuery(id+"F0.wireOp",EDGE,"E11.14.1"),sQuery(id+"F0.wireOp",EDGE,"E11.14.2"),sQuery(id+"F0.wireOp",EDGE,"E11.15.0"),sQuery(id+"F0.wireOp",EDGE,"E11.15.1"),sQuery(id+"F0.wireOp",EDGE,"E11.15.2"),sQuery(id+"F0.wireOp",EDGE,"E11.16.0"),sQuery(id+"F0.wireOp",EDGE,"E11.16.1"),sQuery(id+"F0.wireOp",EDGE,"E11.16.2"),sQuery(id+"F0.wireOp",EDGE,"E11.17.0"),sQuery(id+"F0.wireOp",EDGE,"E11.17.1"),sQuery(id+"F0.wireOp",EDGE,"E11.17.2"),sQuery(id+"F0.wireOp",EDGE,"E11.18.0"),sQuery(id+"F0.wireOp",EDGE,"E11.18.1"),sQuery(id+"F0.wireOp",EDGE,"E11.18.2"),sQuery(id+"F0.wireOp",EDGE,"E11.19.0"),sQuery(id+"F0.wireOp",EDGE,"E11.19.1"),sQuery(id+"F0.wireOp",EDGE,"E11.19.2"),sQuery(id+"F0.wireOp",EDGE,"E11.20.0"),sQuery(id+"F0.wireOp",EDGE,"E11.20.1"),sQuery(id+"F0.wireOp",EDGE,"E11.20.2"),sQuery(id+"F0.wireOp",EDGE,"E11.21.0"),sQuery(id+"F0.wireOp",EDGE,"E11.21.1"),sQuery(id+"F0.wireOp",EDGE,"E11.21.2"),sQuery(id+"F0.wireOp",EDGE,"E11.22.0"),sQuery(id+"F0.wireOp",EDGE,"E11.22.1"),sQuery(id+"F0.wireOp",EDGE,"E11.22.2"),sQuery(id+"F0.wireOp",EDGE,"E11.23.0"),sQuery(id+"F0.wireOp",EDGE,"E11.23.1"),sQuery(id+"F0.wireOp",EDGE,"E11.23.2"),sQuery(id+"F0.wireOp",EDGE,"E11.24.0"),sQuery(id+"F0.wireOp",EDGE,"E11.24.1"),sQuery(id+"F0.wireOp",EDGE,"E11.24.2"),sQuery(id+"F0.wireOp",EDGE,"E11.25.0"),sQuery(id+"F0.wireOp",EDGE,"E11.25.1"),sQuery(id+"F0.wireOp",EDGE,"E11.25.2"),sQuery(id+"F0.wireOp",EDGE,"E11.26.0"),sQuery(id+"F0.wireOp",EDGE,"E11.26.1"),sQuery(id+"F0.wireOp",EDGE,"E11.26.2"),sQuery(id+"F0.wireOp",EDGE,"E11.27.0"),sQuery(id+"F0.wireOp",EDGE,"E11.27.1"),sQuery(id+"F0.wireOp",EDGE,"E11.27.2"),sQuery(id+"F0.wireOp",EDGE,"E11.28.0"),sQuery(id+"F0.wireOp",EDGE,"E11.28.1"),sQuery(id+"F0.wireOp",EDGE,"E11.28.2"),sQuery(id+"F0.wireOp",EDGE,"E11.29.0"),sQuery(id+"F0.wireOp",EDGE,"E11.29.1"),sQuery(id+"F0.wireOp",EDGE,"E11.29.2"),sQuery(id+"F0.wireOp",EDGE,"E12"),sQuery(id+"F0.wireOp",EDGE,"E14"),sQuery(id+"F0.wireOp",EDGE,"E15.1.0"),sQuery(id+"F0.wireOp",EDGE,"E15.2.0"),sQuery(id+"F0.wireOp",EDGE,"E15.3.0"),sQuery(id+"F0.wireOp",EDGE,"E15.4.0"),sQuery(id+"F0.wireOp",EDGE,"E15.5.0"),sQuery(id+"F0.wireOp",EDGE,"E15.6.0"),sQuery(id+"F0.wireOp",EDGE,"E15.7.0"),sQuery(id+"F0.wireOp",EDGE,"E15.8.0"),sQuery(id+"F0.wireOp",EDGE,"E15.9.0"),sQuery(id+"F0.wireOp",EDGE,"E15.10.0"),sQuery(id+"F0.wireOp",EDGE,"E15.11.0"),sQuery(id+"F0.wireOp",EDGE,"E15.12.0"),sQuery(id+"F0.wireOp",EDGE,"E15.13.0"),sQuery(id+"F0.wireOp",EDGE,"E15.14.0"),sQuery(id+"F0.wireOp",EDGE,"E15.15.0"),sQuery(id+"F0.wireOp",EDGE,"E15.16.0"),sQuery(id+"F0.wireOp",EDGE,"E15.17.0"),sQuery(id+"F0.wireOp",EDGE,"E15.18.0"),sQuery(id+"F0.wireOp",EDGE,"E15.19.0"),sQuery(id+"F0.wireOp",EDGE,"E15.20.0"),sQuery(id+"F0.wireOp",EDGE,"E15.21.0"),sQuery(id+"F0.wireOp",EDGE,"E15.22.0"),sQuery(id+"F0.wireOp",EDGE,"E15.23.0"),sQuery(id+"F0.wireOp",EDGE,"E15.24.0"),sQuery(id+"F0.wireOp",EDGE,"E15.25.0"),sQuery(id+"F0.wireOp",EDGE,"E15.26.0"),sQuery(id+"F0.wireOp",EDGE,"E15.27.0"),sQuery(id+"F0.wireOp",EDGE,"E15.28.0"),sQuery(id+"F0.wireOp",EDGE,"E15.29.0")])]}),"instanceName":"1"}),"instanceName":"1"}),"instanceName":"1"});
            var Q1;
            Q1=makeQuery(id+"F17.opPattern","COPY",EDGE,{"derivedFrom":makeQuery(id+"F15.opPattern","COPY",EDGE,{"derivedFrom":makeQuery(id+"F4.opPattern","COPY",EDGE,{"derivedFrom":makeQuery(id+"F2.opExtrude","CAP_EDGE",EDGE,{"disambiguationData":[OSD([sQuery(id+"F0.wireOp",EDGE,"E0")])],"isStart":true}),"instanceName":"1"}),"instanceName":"1"}),"instanceName":"1"});
            transform(context, id + "F18", {"entities" : qUnion([Q0]), "transformType" : TransformType.ROTATION, "transformAxis" : qUnion([Q1]), "angle" : 4 * degree, "oppositeDirection" : true, "makeCopy" : false});
        }
    });
